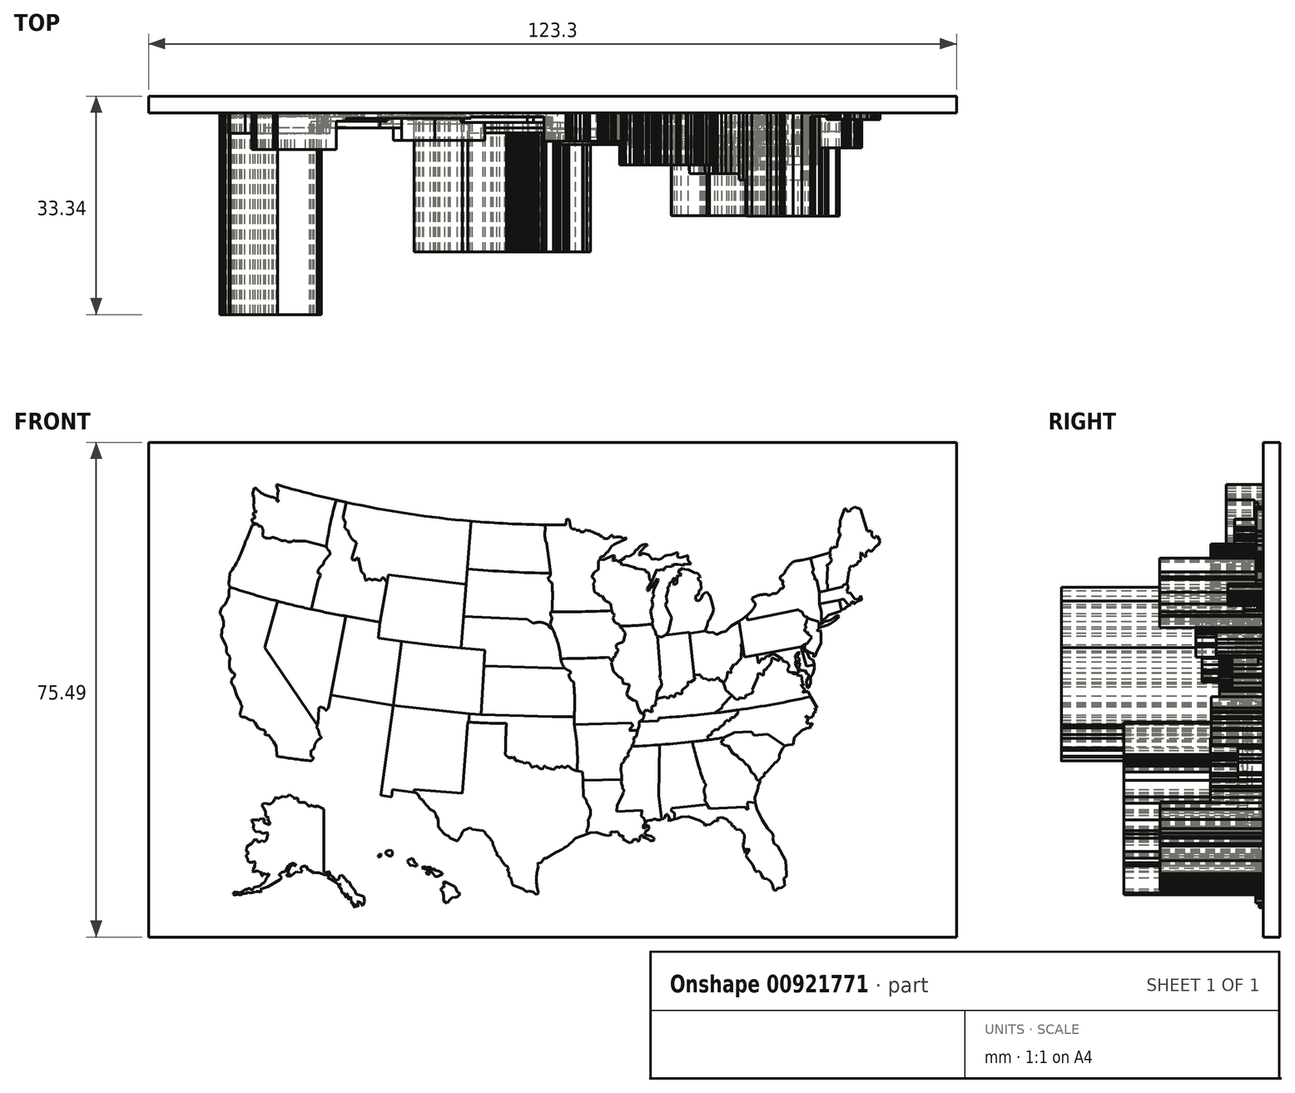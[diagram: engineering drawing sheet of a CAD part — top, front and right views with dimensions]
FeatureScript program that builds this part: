
annotation { "Feature Type Name" : "Feature", "Feature Type Description" : "" }
export const myFeature = defineFeature(function(context is Context, id is Id, definition is map)
    precondition{}
    {
        {
            var Q0;
            Q0=qCreatedBy(makeId("Front.planeOp"),FACE);
            var sketch = newSketch(context, id + "F0", { "sketchPlane" : qUnion([Q0])});
            skLineSegment(sketch, "E0.bottom", {"start": v(-61.56, 41.77) * mm, "end": v(61.74, 41.77) * mm});
            skLineSegment(sketch, "E0.top", {"start": v(-61.56, -33.72) * mm, "end": v(61.74, -33.72) * mm});
            skLineSegment(sketch, "E0.left", {"start": v(-61.56, 41.77) * mm, "end": v(-61.56, -33.72) * mm});
            skLineSegment(sketch, "E0.right", {"start": v(61.74, 41.77) * mm, "end": v(61.74, -33.72) * mm});
            skSolve(sketch);
        }
        {
            var Q0;
            Q0=qSketchRegion(id+"F0",true);
            extrude(context, id + "F1", {"entities" : qUnion([Q0]), "depth" : 2.54 * mm, "offsetDistance" : 25.4 * mm});
        }
        {
            var Q0;
            Q0=makeQuery(id+"F1.opExtrude","CAP_FACE",FACE,{"disambiguationData":[OSD([sQuery(id+"F0.wireOp",EDGE,"E0.bottom"),sQuery(id+"F0.wireOp",EDGE,"E0.top"),sQuery(id+"F0.wireOp",EDGE,"E0.left"),sQuery(id+"F0.wireOp",EDGE,"E0.right")])],"isStart":false});
            var sketch = newSketch(context, id + "F2", { "sketchPlane" : qUnion([Q0])});
            skLineSegment(sketch, "E1", {"start": v(-6.58, -23.8) * mm, "end": v(-6.79, -23.67) * mm});
            skLineSegment(sketch, "E2", {"start": v(-6.79, -23.67) * mm, "end": v(-6.62, -23.2) * mm});
            skLineSegment(sketch, "E3", {"start": v(-6.86, -22.87) * mm, "end": v(-6.62, -23.2) * mm});
            skLineSegment(sketch, "E4", {"start": v(-6.86, -22.87) * mm, "end": v(-7.18, -22.74) * mm});
            skArc(sketch, "E5", {"start": v(-7.96, -21.52) * mm, "mid": v(-7.6, -22.15) * mm, "end": v(-7.18, -22.74) * mm});
            skArc(sketch, "E6", {"start": v(-8.39, -21.24) * mm, "mid": v(-8.17, -21.38) * mm, "end": v(-7.96, -21.52) * mm});
            skArc(sketch, "E7", {"start": v(-8.39, -20.98) * mm, "mid": v(-8.39, -21.1) * mm, "end": v(-8.39, -21.24) * mm});
            skArc(sketch, "E8", {"start": v(-8.98, -19.66) * mm, "mid": v(-8.7, -20.33) * mm, "end": v(-8.39, -20.98) * mm});
            skArc(sketch, "E9", {"start": v(-9.07, -19.19) * mm, "mid": v(-9.17, -19.07) * mm, "end": v(-9.29, -18.98) * mm});
            skArc(sketch, "E10", {"start": v(-9.07, -19.19) * mm, "mid": v(-9.03, -19.42) * mm, "end": v(-8.98, -19.66) * mm});
            skLineSegment(sketch, "E11", {"start": v(-22.96, 11.38) * mm, "end": v(-24.2, 1.61) * mm});
            skLineSegment(sketch, "E12", {"start": v(-10.22, 10.07) * mm, "end": v(-10.37, 7.64) * mm});
            skLineSegment(sketch, "E13", {"start": v(-31.44, 15.25) * mm, "end": v(-26.22, 14.33) * mm});
            skLineSegment(sketch, "E14", {"start": v(-26.22, 14.33) * mm, "end": v(-26.5, 11.9) * mm});
            skLineSegment(sketch, "E15", {"start": v(-26.5, 11.9) * mm, "end": v(-22.96, 11.38) * mm});
            skLineSegment(sketch, "E16", {"start": v(-33.75, 3.22) * mm, "end": v(-31.44, 15.25) * mm});
            skArc(sketch, "E17", {"start": v(-49.13, 19.66) * mm, "mid": v(-40.36, 17.15) * mm, "end": v(-31.44, 15.25) * mm});
            skLineSegment(sketch, "E18", {"start": v(-43.82, 10.48) * mm, "end": v(-41.9, 17.54) * mm});
            skLineSegment(sketch, "E19", {"start": v(-43.82, 10.48) * mm, "end": v(-35.84, -1.39) * mm});
            skLineSegment(sketch, "E20", {"start": v(-26.22, 14.33) * mm, "end": v(-24.95, 21.56) * mm});
            skLineSegment(sketch, "E21", {"start": v(-13.08, 20.1) * mm, "end": v(-24.95, 21.56) * mm});
            skLineSegment(sketch, "E22", {"start": v(-13.67, -11.77) * mm, "end": v(-12.83, -0.9) * mm});
            skLineSegment(sketch, "E23", {"start": v(-12.83, -0.9) * mm, "end": v(-12.71, -0.9) * mm});
            skLineSegment(sketch, "E24", {"start": v(-12.71, -0.9) * mm, "end": v(-12.62, 0.37) * mm});
            skLineSegment(sketch, "E25", {"start": v(-26.15, -12.1) * mm, "end": v(-24.45, -12.34) * mm});
            skLineSegment(sketch, "E26", {"start": v(-24.45, -12.34) * mm, "end": v(-24.33, -11.2) * mm});
            skLineSegment(sketch, "E27", {"start": v(-24.33, -11.2) * mm, "end": v(-21.02, -11.66) * mm});
            skLineSegment(sketch, "E28", {"start": v(-21.02, -11.66) * mm, "end": v(-21.02, -11.2) * mm});
            skLineSegment(sketch, "E29", {"start": v(-21.02, -11.2) * mm, "end": v(-13.67, -11.77) * mm});
            skLineSegment(sketch, "E30", {"start": v(-37.29, -7.31) * mm, "end": v(-30.35, -11.42) * mm});
            skLineSegment(sketch, "E31", {"start": v(-30.35, -11.42) * mm, "end": v(-26.15, -12.1) * mm});
            skArc(sketch, "E32", {"start": v(-12.71, -0.9) * mm, "mid": v(-9.83, -1.07) * mm, "end": v(-6.95, -1.13) * mm});
            skArc(sketch, "E33", {"start": v(-6.95, -1.13) * mm, "mid": v(-7.05, -3.5) * mm, "end": v(-7.1, -5.86) * mm});
            skArc(sketch, "E34", {"start": v(-41.92, 35.31) * mm, "mid": v(-20.1, 30.62) * mm, "end": v(2.16, 29.2) * mm});
            skLineSegment(sketch, "E35", {"start": v(-13.08, 20.1) * mm, "end": v(-12.32, 29.75) * mm});
            skLineSegment(sketch, "E36", {"start": v(-13.46, 15.24) * mm, "end": v(-3.77, 14.75) * mm});
            skLineSegment(sketch, "E37", {"start": v(-10.37, 7.64) * mm, "end": v(2.04, 7.28) * mm});
            skArc(sketch, "E38", {"start": v(-0.2, 15.89) * mm, "mid": v(4.47, 15.94) * mm, "end": v(9.13, 16.1) * mm});
            skArc(sketch, "E39", {"start": v(1.33, 8.76) * mm, "mid": v(4.97, 8.83) * mm, "end": v(8.6, 8.97) * mm});
            skArc(sketch, "E40", {"start": v(10.38, 13.78) * mm, "mid": v(12.85, 13.82) * mm, "end": v(15.3, 14.07) * mm});
            skLineSegment(sketch, "E41", {"start": v(17.33, 12.38) * mm, "end": v(20.97, 12.8) * mm});
            skLineSegment(sketch, "E42", {"start": v(20.97, 12.8) * mm, "end": v(21.7, 6.25) * mm});
            skLineSegment(sketch, "E43", {"start": v(21, 12.63) * mm, "end": v(23.37, 13) * mm});
            skLineSegment(sketch, "E44", {"start": v(29.76, 15.36) * mm, "end": v(29.82, 14.67) * mm});
            skLineSegment(sketch, "E45", {"start": v(29.82, 14.67) * mm, "end": v(37.59, 16.24) * mm});
            skLineSegment(sketch, "E46", {"start": v(3.4, -0.12) * mm, "end": v(3.4, -1.32) * mm});
            skLineSegment(sketch, "E47", {"start": v(3.4, -1.32) * mm, "end": v(12.08, -1.02) * mm});
            skArc(sketch, "E48", {"start": v(3.4, -0.12) * mm, "mid": v(3.46, 2.54) * mm, "end": v(3.32, 5.2) * mm});
            skArc(sketch, "E49", {"start": v(-32.92, 32.97) * mm, "mid": v(-33.8, 29.44) * mm, "end": v(-34.4, 25.85) * mm});
            skArc(sketch, "E50", {"start": v(16.29, -0.29) * mm, "mid": v(27.94, 0.87) * mm, "end": v(39.47, 2.95) * mm});
            skLineSegment(sketch, "E51", {"start": v(13.29, -0.87) * mm, "end": v(16.25, -0.73) * mm});
            skLineSegment(sketch, "E52", {"start": v(16.25, -0.73) * mm, "end": v(16.29, -0.29) * mm});
            skArc(sketch, "E53", {"start": v(12.12, -4.62) * mm, "mid": v(19.15, -4.15) * mm, "end": v(26.15, -3.3) * mm});
            skLineSegment(sketch, "E54", {"start": v(4.75, -9.79) * mm, "end": v(10.62, -9.67) * mm});
            skLineSegment(sketch, "E55", {"start": v(-35.84, -1.39) * mm, "end": v(-35.69, -1.16) * mm});
            skLineSegment(sketch, "E56", {"start": v(-35.69, -1.16) * mm, "end": v(-35.58, 1.24) * mm});
            skArc(sketch, "E57", {"start": v(-35.22, 1.38) * mm, "mid": v(-35.42, 1.34) * mm, "end": v(-35.58, 1.24) * mm});
            skArc(sketch, "E58", {"start": v(-34.96, 1.24) * mm, "mid": v(-35.08, 1.33) * mm, "end": v(-35.22, 1.38) * mm});
            skArc(sketch, "E59", {"start": v(-34.77, 1.24) * mm, "mid": v(-34.86, 1.24) * mm, "end": v(-34.96, 1.24) * mm});
            skArc(sketch, "E60", {"start": v(-34.1, 1.24) * mm, "mid": v(-34.26, 1.1) * mm, "end": v(-34.37, 0.9) * mm});
            skArc(sketch, "E61", {"start": v(-34.61, 0.92) * mm, "mid": v(-34.67, 1.09) * mm, "end": v(-34.77, 1.24) * mm});
            skArc(sketch, "E62", {"start": v(-34.61, 0.92) * mm, "mid": v(-34.5, 0.9) * mm, "end": v(-34.37, 0.9) * mm});
            skLineSegment(sketch, "E63", {"start": v(-34.1, 1.24) * mm, "end": v(-33.75, 3.22) * mm});
            skArc(sketch, "E64", {"start": v(-42, -6.13) * mm, "mid": v(-39.51, -6.5) * mm, "end": v(-37, -6.82) * mm});
            skArc(sketch, "E65", {"start": v(-37, -6.82) * mm, "mid": v(-37.16, -7.06) * mm, "end": v(-37.29, -7.31) * mm});
            skLineSegment(sketch, "E66", {"start": v(-42.06, -4.67) * mm, "end": v(-42, -6.13) * mm});
            skLineSegment(sketch, "E67", {"start": v(-42.06, -4.67) * mm, "end": v(-42.49, -3.88) * mm});
            skLineSegment(sketch, "E68", {"start": v(-42.49, -3.88) * mm, "end": v(-42.72, -3.66) * mm});
            skLineSegment(sketch, "E69", {"start": v(-42.72, -3.66) * mm, "end": v(-43.18, -2.97) * mm});
            skLineSegment(sketch, "E70", {"start": v(-43.18, -2.97) * mm, "end": v(-43.84, -2.85) * mm});
            skLineSegment(sketch, "E71", {"start": v(-43.84, -2.85) * mm, "end": v(-43.84, -2.72) * mm});
            skLineSegment(sketch, "E72", {"start": v(-43.84, -2.72) * mm, "end": v(-43.74, -2.65) * mm});
            skLineSegment(sketch, "E73", {"start": v(-43.74, -2.65) * mm, "end": v(-43.78, -2.32) * mm});
            skLineSegment(sketch, "E74", {"start": v(-43.78, -2.32) * mm, "end": v(-43.93, -2.1) * mm});
            skLineSegment(sketch, "E75", {"start": v(-43.93, -2.1) * mm, "end": v(-44.47, -2) * mm});
            skLineSegment(sketch, "E76", {"start": v(-44.47, -2) * mm, "end": v(-44.88, -1.78) * mm});
            skLineSegment(sketch, "E77", {"start": v(-44.88, -1.78) * mm, "end": v(-45.3, -1.03) * mm});
            skLineSegment(sketch, "E78", {"start": v(-45.3, -1.03) * mm, "end": v(-45.63, -0.64) * mm});
            skLineSegment(sketch, "E79", {"start": v(-45.63, -0.64) * mm, "end": v(-46.03, -0.6) * mm});
            skLineSegment(sketch, "E80", {"start": v(-46.03, -0.6) * mm, "end": v(-46.9, -0.18) * mm});
            skLineSegment(sketch, "E81", {"start": v(-46.9, -0.18) * mm, "end": v(-47.32, -0.12) * mm});
            skLineSegment(sketch, "E82", {"start": v(-47.32, -0.12) * mm, "end": v(-47.62, 0.17) * mm});
            skLineSegment(sketch, "E83", {"start": v(-47.62, 0.17) * mm, "end": v(-47.32, 1.4) * mm});
            skLineSegment(sketch, "E84", {"start": v(-47.32, 1.4) * mm, "end": v(-47.32, 1.65) * mm});
            skLineSegment(sketch, "E85", {"start": v(-47.32, 1.65) * mm, "end": v(-47.5, 1.8) * mm});
            skLineSegment(sketch, "E86", {"start": v(-47.5, 1.8) * mm, "end": v(-47.5, 2.07) * mm});
            skLineSegment(sketch, "E87", {"start": v(-47.5, 2.07) * mm, "end": v(-48.07, 3.06) * mm});
            skLineSegment(sketch, "E88", {"start": v(-48.07, 3.06) * mm, "end": v(-48.53, 4.45) * mm});
            skLineSegment(sketch, "E89", {"start": v(-48.53, 4.45) * mm, "end": v(-48.84, 4.92) * mm});
            skLineSegment(sketch, "E90", {"start": v(-48.84, 4.92) * mm, "end": v(-48.94, 5.2) * mm});
            skLineSegment(sketch, "E91", {"start": v(-48.94, 5.2) * mm, "end": v(-48.88, 5.7) * mm});
            skArc(sketch, "E92", {"start": v(-48.88, 5.7) * mm, "mid": v(-48.47, 6.05) * mm, "end": v(-48.5, 6.58) * mm});
            skLineSegment(sketch, "E93", {"start": v(-48.5, 6.58) * mm, "end": v(-48.77, 6.64) * mm});
            skLineSegment(sketch, "E94", {"start": v(-48.77, 6.64) * mm, "end": v(-49.26, 7.32) * mm});
            skLineSegment(sketch, "E95", {"start": v(-49.26, 7.32) * mm, "end": v(-49.26, 8.3) * mm});
            skLineSegment(sketch, "E96", {"start": v(-49.26, 8.3) * mm, "end": v(-49.08, 9) * mm});
            skLineSegment(sketch, "E97", {"start": v(-49.08, 9) * mm, "end": v(-49.69, 9.7) * mm});
            skLineSegment(sketch, "E98", {"start": v(-49.69, 9.7) * mm, "end": v(-49.69, 9.96) * mm});
            skArc(sketch, "E99", {"start": v(-49.69, 9.96) * mm, "mid": v(-49.66, 10.43) * mm, "end": v(-49.81, 10.88) * mm});
            skLineSegment(sketch, "E100", {"start": v(-50.52, 12.25) * mm, "end": v(-49.81, 10.88) * mm});
            skLineSegment(sketch, "E101", {"start": v(-50.52, 12.25) * mm, "end": v(-50.4, 12.67) * mm});
            skLineSegment(sketch, "E102", {"start": v(-50.4, 12.67) * mm, "end": v(-50.35, 13.32) * mm});
            skLineSegment(sketch, "E103", {"start": v(-50.35, 13.32) * mm, "end": v(-50.15, 13.64) * mm});
            skLineSegment(sketch, "E104", {"start": v(-50.15, 13.64) * mm, "end": v(-50.12, 14.44) * mm});
            skLineSegment(sketch, "E105", {"start": v(-50.12, 14.44) * mm, "end": v(-50.4, 15.26) * mm});
            skLineSegment(sketch, "E106", {"start": v(-50.4, 15.26) * mm, "end": v(-50.7, 15.68) * mm});
            skLineSegment(sketch, "E107", {"start": v(-50.7, 15.68) * mm, "end": v(-50.46, 16.55) * mm});
            skLineSegment(sketch, "E108", {"start": v(-50.46, 16.55) * mm, "end": v(-50.27, 16.6) * mm});
            skLineSegment(sketch, "E109", {"start": v(-50.27, 16.6) * mm, "end": v(-50.23, 16.77) * mm});
            skLineSegment(sketch, "E110", {"start": v(-50.23, 16.77) * mm, "end": v(-49.9, 17.06) * mm});
            skLineSegment(sketch, "E111", {"start": v(-49.9, 17.06) * mm, "end": v(-49.32, 18.34) * mm});
            skLineSegment(sketch, "E112", {"start": v(-49.32, 18.34) * mm, "end": v(-49.32, 19.18) * mm});
            skLineSegment(sketch, "E113", {"start": v(-49.32, 19.18) * mm, "end": v(-49.13, 19.66) * mm});
            skArc(sketch, "E114", {"start": v(-35.53, -2.8) * mm, "mid": v(-35.62, -2.26) * mm, "end": v(-35.89, -1.79) * mm});
            skLineSegment(sketch, "E115", {"start": v(-35.84, -1.39) * mm, "end": v(-35.89, -1.79) * mm});
            skArc(sketch, "E116", {"start": v(-37, -6.82) * mm, "mid": v(-36.56, -6.69) * mm, "end": v(-36.45, -6.23) * mm});
            skLineSegment(sketch, "E117", {"start": v(-36.45, -6.23) * mm, "end": v(-36.81, -6.15) * mm});
            skLineSegment(sketch, "E118", {"start": v(-36.81, -6.15) * mm, "end": v(-36.77, -5.26) * mm});
            skArc(sketch, "E119", {"start": v(-36.77, -5.26) * mm, "mid": v(-36.48, -5.1) * mm, "end": v(-36.25, -4.85) * mm});
            skArc(sketch, "E120", {"start": v(-35.2, -3.37) * mm, "mid": v(-35.98, -3.93) * mm, "end": v(-36.25, -4.85) * mm});
            skArc(sketch, "E121", {"start": v(-35.2, -3.37) * mm, "mid": v(-35.32, -3.06) * mm, "end": v(-35.53, -2.8) * mm});
            skLineSegment(sketch, "E122", {"start": v(-36.71, 16.3) * mm, "end": v(-35.69, 20.66) * mm});
            skLineSegment(sketch, "E123", {"start": v(-35.69, 20.66) * mm, "end": v(-35.3, 21.49) * mm});
            skLineSegment(sketch, "E124", {"start": v(-35.3, 21.49) * mm, "end": v(-35.42, 21.74) * mm});
            skLineSegment(sketch, "E125", {"start": v(-35.42, 21.74) * mm, "end": v(-35.73, 21.82) * mm});
            skLineSegment(sketch, "E126", {"start": v(-34.4, 25.85) * mm, "end": v(-37.6, 26.7) * mm});
            skLineSegment(sketch, "E127", {"start": v(-37.6, 26.7) * mm, "end": v(-39.29, 26.7) * mm});
            skLineSegment(sketch, "E128", {"start": v(-39.29, 26.7) * mm, "end": v(-39.29, 26.82) * mm});
            skLineSegment(sketch, "E129", {"start": v(-39.29, 26.82) * mm, "end": v(-39.85, 26.6) * mm});
            skLineSegment(sketch, "E130", {"start": v(-39.85, 26.6) * mm, "end": v(-40.34, 26.6) * mm});
            skLineSegment(sketch, "E131", {"start": v(-40.34, 26.6) * mm, "end": v(-40.67, 26.84) * mm});
            skLineSegment(sketch, "E132", {"start": v(-40.67, 26.84) * mm, "end": v(-40.81, 26.76) * mm});
            skLineSegment(sketch, "E133", {"start": v(-40.81, 26.76) * mm, "end": v(-41.31, 26.76) * mm});
            skArc(sketch, "E134", {"start": v(-41.31, 26.76) * mm, "mid": v(-41.96, 27.09) * mm, "end": v(-42.67, 27.29) * mm});
            skArc(sketch, "E135", {"start": v(-44.22, 27.59) * mm, "mid": v(-43.5, 27.14) * mm, "end": v(-42.67, 27.29) * mm});
            skArc(sketch, "E136", {"start": v(-44.22, 27.59) * mm, "mid": v(-44.1, 28.32) * mm, "end": v(-44.4, 29) * mm});
            skLineSegment(sketch, "E137", {"start": v(-44.4, 29) * mm, "end": v(-44.82, 29) * mm});
            skLineSegment(sketch, "E138", {"start": v(-44.82, 29) * mm, "end": v(-44.82, 29.3) * mm});
            skLineSegment(sketch, "E139", {"start": v(-44.82, 29.3) * mm, "end": v(-45.08, 29.3) * mm});
            skLineSegment(sketch, "E140", {"start": v(-45.08, 29.3) * mm, "end": v(-45.37, 29.53) * mm});
            skLineSegment(sketch, "E141", {"start": v(-45.37, 29.53) * mm, "end": v(-45.56, 29.45) * mm});
            skLineSegment(sketch, "E142", {"start": v(-45.56, 29.45) * mm, "end": v(-45.81, 29.75) * mm});
            skLineSegment(sketch, "E143", {"start": v(-45.81, 29.75) * mm, "end": v(-45.78, 30.08) * mm});
            skLineSegment(sketch, "E144", {"start": v(-45.78, 30.08) * mm, "end": v(-45.5, 30.08) * mm});
            skLineSegment(sketch, "E145", {"start": v(-45.5, 30.08) * mm, "end": v(-45.31, 30.55) * mm});
            skLineSegment(sketch, "E146", {"start": v(-45.31, 30.55) * mm, "end": v(-45.58, 30.7) * mm});
            skLineSegment(sketch, "E147", {"start": v(-45.58, 30.7) * mm, "end": v(-45.55, 31.09) * mm});
            skLineSegment(sketch, "E148", {"start": v(-45.55, 31.09) * mm, "end": v(-45.04, 31.14) * mm});
            skLineSegment(sketch, "E149", {"start": v(-45.04, 31.14) * mm, "end": v(-45.4, 31.48) * mm});
            skLineSegment(sketch, "E150", {"start": v(-45.4, 31.48) * mm, "end": v(-45.54, 32.25) * mm});
            skLineSegment(sketch, "E151", {"start": v(-45.54, 32.25) * mm, "end": v(-45.47, 32.5) * mm});
            skLineSegment(sketch, "E152", {"start": v(-45.47, 32.5) * mm, "end": v(-45.47, 33.45) * mm});
            skLineSegment(sketch, "E153", {"start": v(-45.47, 33.45) * mm, "end": v(-45.66, 33.77) * mm});
            skLineSegment(sketch, "E154", {"start": v(-45.66, 33.77) * mm, "end": v(-45.66, 33.96) * mm});
            skLineSegment(sketch, "E155", {"start": v(-45.66, 33.96) * mm, "end": v(-45.45, 34.83) * mm});
            skLineSegment(sketch, "E156", {"start": v(-45.45, 34.83) * mm, "end": v(-45.2, 34.8) * mm});
            skArc(sketch, "E157", {"start": v(-45.2, 34.8) * mm, "mid": v(-43.98, 33.84) * mm, "end": v(-42.5, 33.4) * mm});
            skArc(sketch, "E158", {"start": v(-41.95, 32.72) * mm, "mid": v(-42.12, 33.15) * mm, "end": v(-42.5, 33.4) * mm});
            skArc(sketch, "E159", {"start": v(-41.83, 33.55) * mm, "mid": v(-41.91, 33.21) * mm, "end": v(-41.75, 32.9) * mm});
            skArc(sketch, "E160", {"start": v(-41.71, 34.33) * mm, "mid": v(-41.88, 33.96) * mm, "end": v(-41.83, 33.55) * mm});
            skLineSegment(sketch, "E161", {"start": v(-41.75, 32.9) * mm, "end": v(-41.75, 32.72) * mm});
            skLineSegment(sketch, "E162", {"start": v(-41.75, 32.72) * mm, "end": v(-41.95, 32.72) * mm});
            skLineSegment(sketch, "E163", {"start": v(-41.71, 34.33) * mm, "end": v(-42.05, 35.14) * mm});
            skLineSegment(sketch, "E164", {"start": v(-42.05, 35.14) * mm, "end": v(-42, 35.32) * mm});
            skLineSegment(sketch, "E165", {"start": v(-42, 35.32) * mm, "end": v(-41.92, 35.31) * mm});
            skArc(sketch, "E166", {"start": v(-34.98, 23.04) * mm, "mid": v(-35.52, 22.54) * mm, "end": v(-35.73, 21.82) * mm});
            skArc(sketch, "E167", {"start": v(-34.98, 23.04) * mm, "mid": v(-34.87, 23.25) * mm, "end": v(-34.84, 23.49) * mm});
            skArc(sketch, "E168", {"start": v(-33.85, 24.71) * mm, "mid": v(-34.37, 24.12) * mm, "end": v(-34.84, 23.49) * mm});
            skArc(sketch, "E169", {"start": v(-34.4, 25.85) * mm, "mid": v(-34.24, 25.45) * mm, "end": v(-33.9, 25.17) * mm});
            skLineSegment(sketch, "E170", {"start": v(-33.9, 25.17) * mm, "end": v(-33.85, 24.71) * mm});
            skArc(sketch, "E171", {"start": v(29.76, 15.36) * mm, "mid": v(30.49, 16.06) * mm, "end": v(31.05, 16.9) * mm});
            skArc(sketch, "E172", {"start": v(30.53, 18) * mm, "mid": v(30.63, 17.74) * mm, "end": v(30.73, 17.47) * mm});
            skArc(sketch, "E173", {"start": v(31.05, 16.9) * mm, "mid": v(30.98, 17.24) * mm, "end": v(30.73, 17.47) * mm});
            skArc(sketch, "E174", {"start": v(32.87, 18.54) * mm, "mid": v(31.66, 18.47) * mm, "end": v(30.53, 18) * mm});
            skArc(sketch, "E175", {"start": v(32.87, 18.54) * mm, "mid": v(33.13, 18.43) * mm, "end": v(33.4, 18.54) * mm});
            skArc(sketch, "E176", {"start": v(34.3, 18.7) * mm, "mid": v(33.83, 18.7) * mm, "end": v(33.4, 18.54) * mm});
            skArc(sketch, "E177", {"start": v(34.3, 18.7) * mm, "mid": v(34.63, 19.09) * mm, "end": v(34.94, 19.49) * mm});
            skArc(sketch, "E178", {"start": v(34.94, 19.49) * mm, "mid": v(35.35, 19.65) * mm, "end": v(35.2, 20.07) * mm});
            skArc(sketch, "E179", {"start": v(35.34, 20.66) * mm, "mid": v(35.23, 20.38) * mm, "end": v(35.2, 20.07) * mm});
            skArc(sketch, "E180", {"start": v(35.14, 21.47) * mm, "mid": v(34.83, 20.97) * mm, "end": v(35.34, 20.66) * mm});
            skArc(sketch, "E181", {"start": v(35.14, 21.47) * mm, "mid": v(35.32, 21.65) * mm, "end": v(35.49, 21.84) * mm});
            skArc(sketch, "E182", {"start": v(36.8, 23.54) * mm, "mid": v(36.05, 22.76) * mm, "end": v(35.49, 21.84) * mm});
            skArc(sketch, "E183", {"start": v(37.59, 16.24) * mm, "mid": v(37.87, 16.03) * mm, "end": v(38.21, 15.93) * mm});
            skArc(sketch, "E184", {"start": v(38.21, 15.93) * mm, "mid": v(38.36, 15.5) * mm, "end": v(38.65, 15.13) * mm});
            skArc(sketch, "E185", {"start": v(39.13, 14.92) * mm, "mid": v(38.93, 15.11) * mm, "end": v(38.65, 15.13) * mm});
            skLineSegment(sketch, "E186", {"start": v(39.13, 14.92) * mm, "end": v(40.77, 14.41) * mm});
            skLineSegment(sketch, "E187", {"start": v(40.77, 14.41) * mm, "end": v(40.77, 13.52) * mm});
            skArc(sketch, "E188", {"start": v(40.77, 13.52) * mm, "mid": v(42.45, 14.08) * mm, "end": v(43.84, 15.2) * mm});
            skLineSegment(sketch, "E189", {"start": v(43.84, 15.2) * mm, "end": v(43.42, 15.38) * mm});
            skArc(sketch, "E190", {"start": v(42.11, 14.53) * mm, "mid": v(42.84, 14.85) * mm, "end": v(43.42, 15.38) * mm});
            skArc(sketch, "E191", {"start": v(41.68, 14.53) * mm, "mid": v(41.9, 14.5) * mm, "end": v(42.11, 14.53) * mm});
            skLineSegment(sketch, "E192", {"start": v(41.68, 14.53) * mm, "end": v(41.18, 14.1) * mm});
            skLineSegment(sketch, "E193", {"start": v(41.18, 14.1) * mm, "end": v(40.99, 14.05) * mm});
            skLineSegment(sketch, "E194", {"start": v(40.99, 14.05) * mm, "end": v(40.99, 14.2) * mm});
            skLineSegment(sketch, "E195", {"start": v(40.99, 14.2) * mm, "end": v(41.18, 14.4) * mm});
            skLineSegment(sketch, "E196", {"start": v(41.18, 14.4) * mm, "end": v(41.18, 14.59) * mm});
            skLineSegment(sketch, "E197", {"start": v(41.18, 14.59) * mm, "end": v(40.98, 14.78) * mm});
            skLineSegment(sketch, "E198", {"start": v(40.98, 14.78) * mm, "end": v(41.1, 14.92) * mm});
            skLineSegment(sketch, "E199", {"start": v(41.1, 14.92) * mm, "end": v(41.1, 15.93) * mm});
            skLineSegment(sketch, "E200", {"start": v(41.1, 15.93) * mm, "end": v(40.82, 17.1) * mm});
            skLineSegment(sketch, "E201", {"start": v(40.82, 17.1) * mm, "end": v(40.82, 18.87) * mm});
            skLineSegment(sketch, "E202", {"start": v(40.82, 18.87) * mm, "end": v(40.42, 20.72) * mm});
            skArc(sketch, "E203", {"start": v(40.42, 20.72) * mm, "mid": v(40.27, 20.87) * mm, "end": v(40.08, 20.79) * mm});
            skArc(sketch, "E204", {"start": v(38.13, 23.76) * mm, "mid": v(37.46, 23.7) * mm, "end": v(36.8, 23.54) * mm});
            skLineSegment(sketch, "E205", {"start": v(38.13, 23.76) * mm, "end": v(39.46, 24.13) * mm});
            skLineSegment(sketch, "E206", {"start": v(39.46, 24.13) * mm, "end": v(39.88, 22.6) * mm});
            skArc(sketch, "E207", {"start": v(39.74, 21.98) * mm, "mid": v(39.89, 22.27) * mm, "end": v(39.88, 22.6) * mm});
            skLineSegment(sketch, "E208", {"start": v(39.74, 21.98) * mm, "end": v(40.12, 21.25) * mm});
            skLineSegment(sketch, "E209", {"start": v(40.12, 21.25) * mm, "end": v(40.08, 20.79) * mm});
            skLineSegment(sketch, "E210", {"start": v(-49.13, 19.66) * mm, "end": v(-49.38, 20.16) * mm});
            skLineSegment(sketch, "E211", {"start": v(-49.38, 20.16) * mm, "end": v(-49.22, 20.84) * mm});
            skLineSegment(sketch, "E212", {"start": v(-49.22, 20.84) * mm, "end": v(-49.15, 21.8) * mm});
            skArc(sketch, "E213", {"start": v(-49.15, 21.8) * mm, "mid": v(-47.77, 24.1) * mm, "end": v(-46.8, 26.59) * mm});
            skLineSegment(sketch, "E214", {"start": v(-45.08, 29.3) * mm, "end": v(-45.78, 29.15) * mm});
            skArc(sketch, "E215", {"start": v(-46.8, 26.59) * mm, "mid": v(-46.23, 27.84) * mm, "end": v(-45.78, 29.15) * mm});
            skLineSegment(sketch, "E216", {"start": v(-3.77, 14.75) * mm, "end": v(-2.83, 14.13) * mm});
            skArc(sketch, "E217", {"start": v(-0.54, 13.83) * mm, "mid": v(-1.65, 14.3) * mm, "end": v(-2.83, 14.13) * mm});
            skArc(sketch, "E218", {"start": v(-0.54, 13.83) * mm, "mid": v(-0.35, 13.5) * mm, "end": v(0.01, 13.4) * mm});
            skArc(sketch, "E219", {"start": v(1.33, 8.76) * mm, "mid": v(0.9, 11.14) * mm, "end": v(0.01, 13.4) * mm});
            skArc(sketch, "E220", {"start": v(1.33, 8.76) * mm, "mid": v(1.57, 7.96) * mm, "end": v(2.04, 7.28) * mm});
            skArc(sketch, "E221", {"start": v(2.04, 7.28) * mm, "mid": v(2.37, 7.03) * mm, "end": v(2.76, 6.9) * mm});
            skArc(sketch, "E222", {"start": v(2.6, 6.36) * mm, "mid": v(2.84, 6.58) * mm, "end": v(2.76, 6.9) * mm});
            skArc(sketch, "E223", {"start": v(2.6, 6.36) * mm, "mid": v(2.8, 5.67) * mm, "end": v(3.32, 5.2) * mm});
            skLineSegment(sketch, "E224", {"start": v(-31.41, 32.63) * mm, "end": v(-31.88, 30.28) * mm});
            skLineSegment(sketch, "E225", {"start": v(-31.88, 30.28) * mm, "end": v(-31.53, 29.54) * mm});
            skLineSegment(sketch, "E226", {"start": v(-31.53, 29.54) * mm, "end": v(-31.64, 28.82) * mm});
            skArc(sketch, "E227", {"start": v(-31.64, 28.82) * mm, "mid": v(-31.43, 28.53) * mm, "end": v(-31.12, 28.34) * mm});
            skArc(sketch, "E228", {"start": v(-31.12, 28.34) * mm, "mid": v(-30.7, 27.26) * mm, "end": v(-29.8, 26.51) * mm});
            skLineSegment(sketch, "E229", {"start": v(-30.57, 23.98) * mm, "end": v(-29.8, 26.51) * mm});
            skLineSegment(sketch, "E230", {"start": v(-30.24, 23.7) * mm, "end": v(-30.57, 23.98) * mm});
            skLineSegment(sketch, "E231", {"start": v(-28.57, 21.55) * mm, "end": v(-29.1, 22.08) * mm});
            skLineSegment(sketch, "E232", {"start": v(-29.1, 22.08) * mm, "end": v(-29.53, 24.14) * mm});
            skLineSegment(sketch, "E233", {"start": v(-29.53, 24.14) * mm, "end": v(-30.24, 23.7) * mm});
            skArc(sketch, "E234", {"start": v(-28.57, 21.55) * mm, "mid": v(-28.55, 21.07) * mm, "end": v(-28.35, 20.63) * mm});
            skArc(sketch, "E235", {"start": v(-27.48, 20.74) * mm, "mid": v(-27.95, 20.92) * mm, "end": v(-28.35, 20.63) * mm});
            skArc(sketch, "E236", {"start": v(-26.39, 20.63) * mm, "mid": v(-26.92, 20.86) * mm, "end": v(-27.48, 20.74) * mm});
            skArc(sketch, "E237", {"start": v(-26.39, 20.63) * mm, "mid": v(-26.1, 20.75) * mm, "end": v(-25.98, 21.04) * mm});
            skArc(sketch, "E238", {"start": v(-25.56, 21.03) * mm, "mid": v(-25.41, 20.68) * mm, "end": v(-25.15, 20.41) * mm});
            skArc(sketch, "E239", {"start": v(-25.56, 21.03) * mm, "mid": v(-25.77, 21.1) * mm, "end": v(-25.98, 21.04) * mm});
            skArc(sketch, "E240", {"start": v(3.84, -8.37) * mm, "mid": v(3.84, -4.83) * mm, "end": v(3.4, -1.32) * mm});
            skLineSegment(sketch, "E241", {"start": v(3.84, -8.37) * mm, "end": v(4.68, -8.52) * mm});
            skLineSegment(sketch, "E242", {"start": v(4.68, -8.52) * mm, "end": v(4.75, -9.79) * mm});
            skLineSegment(sketch, "E243", {"start": v(4.75, -9.79) * mm, "end": v(4.8, -12.33) * mm});
            skLineSegment(sketch, "E244", {"start": v(-6.58, -23.8) * mm, "end": v(-6.58, -24.24) * mm});
            skArc(sketch, "E245", {"start": v(-6.58, -24.24) * mm, "mid": v(-6.5, -24.51) * mm, "end": v(-6.25, -24.67) * mm});
            skArc(sketch, "E246", {"start": v(-6.25, -24.67) * mm, "mid": v(-6.14, -25.25) * mm, "end": v(-5.96, -25.81) * mm});
            skLineSegment(sketch, "E247", {"start": v(-2.03, -27) * mm, "end": v(-2.35, -27.24) * mm});
            skLineSegment(sketch, "E248", {"start": v(-2.35, -27.24) * mm, "end": v(-2.88, -26.82) * mm});
            skLineSegment(sketch, "E249", {"start": v(-2.88, -26.82) * mm, "end": v(-3.49, -26.72) * mm});
            skLineSegment(sketch, "E250", {"start": v(-3.49, -26.72) * mm, "end": v(-3.72, -26.79) * mm});
            skLineSegment(sketch, "E251", {"start": v(-3.72, -26.79) * mm, "end": v(-3.92, -26.8) * mm});
            skLineSegment(sketch, "E252", {"start": v(-3.92, -26.8) * mm, "end": v(-4.38, -26.37) * mm});
            skLineSegment(sketch, "E253", {"start": v(-4.38, -26.37) * mm, "end": v(-5.96, -25.81) * mm});
            skLineSegment(sketch, "E254", {"start": v(13.06, -2.2) * mm, "end": v(11.8, -2.2) * mm});
            skArc(sketch, "E255", {"start": v(12.28, -1.61) * mm, "mid": v(12, -1.86) * mm, "end": v(11.8, -2.2) * mm});
            skArc(sketch, "E256", {"start": v(12.28, -1.61) * mm, "mid": v(12.26, -1.29) * mm, "end": v(12.08, -1.02) * mm});
            skLineSegment(sketch, "E257", {"start": v(0.01, 13.4) * mm, "end": v(-0.29, 13.99) * mm});
            skLineSegment(sketch, "E258", {"start": v(-0.29, 13.99) * mm, "end": v(0.01, 15.11) * mm});
            skArc(sketch, "E259", {"start": v(-0.2, 15.89) * mm, "mid": v(-0.2, 15.47) * mm, "end": v(0.01, 15.11) * mm});
            skArc(sketch, "E260", {"start": v(-12.9, 22.47) * mm, "mid": v(-6.57, 22.02) * mm, "end": v(-0.24, 21.8) * mm});
            skArc(sketch, "E261", {"start": v(0.01, 15.89) * mm, "mid": v(0.08, 18.1) * mm, "end": v(0.04, 20.3) * mm});
            skArc(sketch, "E262", {"start": v(-0.58, 21.14) * mm, "mid": v(-0.28, 21.4) * mm, "end": v(-0.24, 21.8) * mm});
            skArc(sketch, "E263", {"start": v(-0.58, 21.14) * mm, "mid": v(-0.37, 20.65) * mm, "end": v(0.04, 20.3) * mm});
            skArc(sketch, "E264", {"start": v(-1.03, 28.4) * mm, "mid": v(-1.02, 28.82) * mm, "end": v(-1.2, 29.2) * mm});
            skArc(sketch, "E265", {"start": v(-1.03, 28.4) * mm, "mid": v(-1.06, 27.27) * mm, "end": v(-0.76, 26.18) * mm});
            skLineSegment(sketch, "E266", {"start": v(-0.76, 26.18) * mm, "end": v(-0.31, 22.92) * mm});
            skLineSegment(sketch, "E267", {"start": v(-0.31, 22.92) * mm, "end": v(-0.24, 21.8) * mm});
            skArc(sketch, "E268", {"start": v(5.3, -13.32) * mm, "mid": v(5.2, -12.75) * mm, "end": v(4.8, -12.33) * mm});
            skArc(sketch, "E269", {"start": v(5.5, -15.85) * mm, "mid": v(5.9, -14.55) * mm, "end": v(5.3, -13.32) * mm});
            skArc(sketch, "E270", {"start": v(5.3, -17.48) * mm, "mid": v(5.56, -16.68) * mm, "end": v(5.5, -15.85) * mm});
            skLineSegment(sketch, "E271", {"start": v(5.3, -17.48) * mm, "end": v(5.4, -17.97) * mm});
            skLineSegment(sketch, "E272", {"start": v(5.4, -17.97) * mm, "end": v(3.57, -18.63) * mm});
            skArc(sketch, "E273", {"start": v(0.84, -20.66) * mm, "mid": v(2.33, -19.81) * mm, "end": v(3.57, -18.63) * mm});
            skArc(sketch, "E274", {"start": v(0.84, -20.66) * mm, "mid": v(-0.02, -21.14) * mm, "end": v(-0.82, -21.71) * mm});
            skArc(sketch, "E275", {"start": v(-2.03, -22.86) * mm, "mid": v(-2.37, -24.93) * mm, "end": v(-2.03, -27) * mm});
            skLineSegment(sketch, "E276", {"start": v(-0.82, -21.71) * mm, "end": v(-1.19, -21.71) * mm});
            skLineSegment(sketch, "E277", {"start": v(-1.19, -21.71) * mm, "end": v(-1.65, -22.39) * mm});
            skLineSegment(sketch, "E278", {"start": v(-1.65, -22.39) * mm, "end": v(-2.1, -22.43) * mm});
            skLineSegment(sketch, "E279", {"start": v(-2.1, -22.43) * mm, "end": v(-2.22, -22.65) * mm});
            skLineSegment(sketch, "E280", {"start": v(-2.22, -22.65) * mm, "end": v(-2.03, -22.86) * mm});
            skLineSegment(sketch, "E281", {"start": v(-9.29, -18.98) * mm, "end": v(-9.29, -18.82) * mm});
            skLineSegment(sketch, "E282", {"start": v(-9.29, -18.82) * mm, "end": v(-10.2, -17.93) * mm});
            skLineSegment(sketch, "E283", {"start": v(-10.2, -17.93) * mm, "end": v(-10.2, -17.76) * mm});
            skLineSegment(sketch, "E284", {"start": v(-10.2, -17.76) * mm, "end": v(-10.52, -17.52) * mm});
            skLineSegment(sketch, "E285", {"start": v(-10.52, -17.52) * mm, "end": v(-12.13, -17.32) * mm});
            skLineSegment(sketch, "E286", {"start": v(-12.13, -17.32) * mm, "end": v(-12.48, -17.04) * mm});
            skLineSegment(sketch, "E287", {"start": v(-12.48, -17.04) * mm, "end": v(-13.4, -17.41) * mm});
            skLineSegment(sketch, "E288", {"start": v(-13.4, -17.41) * mm, "end": v(-13.74, -17.82) * mm});
            skLineSegment(sketch, "E289", {"start": v(-13.74, -17.82) * mm, "end": v(-13.77, -18.12) * mm});
            skLineSegment(sketch, "E290", {"start": v(-13.77, -18.12) * mm, "end": v(-14.47, -19.07) * mm});
            skLineSegment(sketch, "E291", {"start": v(-14.47, -19.07) * mm, "end": v(-15.5, -18.65) * mm});
            skLineSegment(sketch, "E292", {"start": v(-15.5, -18.65) * mm, "end": v(-15.75, -18.3) * mm});
            skLineSegment(sketch, "E293", {"start": v(-15.75, -18.3) * mm, "end": v(-16.33, -18.05) * mm});
            skLineSegment(sketch, "E294", {"start": v(-16.33, -18.05) * mm, "end": v(-17.1, -17.24) * mm});
            skLineSegment(sketch, "E295", {"start": v(-17.1, -17.24) * mm, "end": v(-17.35, -16.8) * mm});
            skLineSegment(sketch, "E296", {"start": v(-17.35, -16.8) * mm, "end": v(-17.37, -15.79) * mm});
            skLineSegment(sketch, "E297", {"start": v(-17.37, -15.79) * mm, "end": v(-17.71, -15.17) * mm});
            skLineSegment(sketch, "E298", {"start": v(-17.71, -15.17) * mm, "end": v(-17.78, -14.79) * mm});
            skLineSegment(sketch, "E299", {"start": v(-17.78, -14.79) * mm, "end": v(-18.07, -14.5) * mm});
            skLineSegment(sketch, "E300", {"start": v(-18.07, -14.5) * mm, "end": v(-18.6, -14.24) * mm});
            skLineSegment(sketch, "E301", {"start": v(-18.6, -14.24) * mm, "end": v(-19.57, -13.1) * mm});
            skLineSegment(sketch, "E302", {"start": v(-19.57, -13.1) * mm, "end": v(-19.7, -12.79) * mm});
            skLineSegment(sketch, "E303", {"start": v(-19.7, -12.79) * mm, "end": v(-20.17, -12.57) * mm});
            skLineSegment(sketch, "E304", {"start": v(-20.17, -12.57) * mm, "end": v(-20.35, -12.1) * mm});
            skLineSegment(sketch, "E305", {"start": v(-20.35, -12.1) * mm, "end": v(-20.72, -11.73) * mm});
            skLineSegment(sketch, "E306", {"start": v(-20.72, -11.73) * mm, "end": v(-21.02, -11.66) * mm});
            skArc(sketch, "E307", {"start": v(21.4, -3.92) * mm, "mid": v(22.16, -6.77) * mm, "end": v(23, -9.6) * mm});
            skLineSegment(sketch, "E308", {"start": v(16.4, -4.38) * mm, "end": v(16.3, -12.15) * mm});
            skLineSegment(sketch, "E309", {"start": v(16.3, -12.15) * mm, "end": v(16.74, -15.71) * mm});
            skLineSegment(sketch, "E310", {"start": v(16.74, -15.71) * mm, "end": v(17.12, -15.67) * mm});
            skLineSegment(sketch, "E311", {"start": v(17.12, -15.67) * mm, "end": v(17.42, -14.93) * mm});
            skLineSegment(sketch, "E312", {"start": v(17.42, -14.93) * mm, "end": v(17.64, -15.03) * mm});
            skLineSegment(sketch, "E313", {"start": v(17.64, -15.03) * mm, "end": v(18, -15.7) * mm});
            skLineSegment(sketch, "E314", {"start": v(18, -15.7) * mm, "end": v(17.67, -15.93) * mm});
            skLineSegment(sketch, "E315", {"start": v(17.67, -15.93) * mm, "end": v(17.92, -15.98) * mm});
            skLineSegment(sketch, "E316", {"start": v(17.92, -15.98) * mm, "end": v(18.7, -15.69) * mm});
            skLineSegment(sketch, "E317", {"start": v(18.7, -15.69) * mm, "end": v(19.12, -15.62) * mm});
            skLineSegment(sketch, "E318", {"start": v(19.12, -15.62) * mm, "end": v(19.74, -15.42) * mm});
            skLineSegment(sketch, "E319", {"start": v(19.74, -15.42) * mm, "end": v(20.83, -15.3) * mm});
            skLineSegment(sketch, "E320", {"start": v(20.83, -15.3) * mm, "end": v(22.65, -15.95) * mm});
            skLineSegment(sketch, "E321", {"start": v(22.65, -15.95) * mm, "end": v(22.84, -16.18) * mm});
            skLineSegment(sketch, "E322", {"start": v(22.84, -16.18) * mm, "end": v(22.97, -16.18) * mm});
            skLineSegment(sketch, "E323", {"start": v(22.97, -16.18) * mm, "end": v(23.2, -16.38) * mm});
            skLineSegment(sketch, "E324", {"start": v(23.2, -16.38) * mm, "end": v(23.32, -16.75) * mm});
            skLineSegment(sketch, "E325", {"start": v(23.32, -16.75) * mm, "end": v(23.59, -16.59) * mm});
            skLineSegment(sketch, "E326", {"start": v(23.59, -16.59) * mm, "end": v(24.18, -16.54) * mm});
            skLineSegment(sketch, "E327", {"start": v(24.18, -16.54) * mm, "end": v(24.9, -15.95) * mm});
            skLineSegment(sketch, "E328", {"start": v(24.9, -15.95) * mm, "end": v(25.29, -16) * mm});
            skLineSegment(sketch, "E329", {"start": v(25.29, -16) * mm, "end": v(25.26, -15.57) * mm});
            skLineSegment(sketch, "E330", {"start": v(25.26, -15.57) * mm, "end": v(25.98, -15.46) * mm});
            skLineSegment(sketch, "E331", {"start": v(25.98, -15.46) * mm, "end": v(26.74, -15.74) * mm});
            skLineSegment(sketch, "E332", {"start": v(26.74, -15.74) * mm, "end": v(27.04, -16.15) * mm});
            skLineSegment(sketch, "E333", {"start": v(27.04, -16.15) * mm, "end": v(27.35, -16.3) * mm});
            skLineSegment(sketch, "E334", {"start": v(27.35, -16.3) * mm, "end": v(27.48, -16.75) * mm});
            skLineSegment(sketch, "E335", {"start": v(27.48, -16.75) * mm, "end": v(27.83, -16.84) * mm});
            skLineSegment(sketch, "E336", {"start": v(27.83, -16.84) * mm, "end": v(28.06, -17.27) * mm});
            skLineSegment(sketch, "E337", {"start": v(28.06, -17.27) * mm, "end": v(28.8, -17.36) * mm});
            skLineSegment(sketch, "E338", {"start": v(24.01, -14.13) * mm, "end": v(29.58, -13.85) * mm});
            skLineSegment(sketch, "E339", {"start": v(18.26, -14.07) * mm, "end": v(23.65, -13.52) * mm});
            skLineSegment(sketch, "E340", {"start": v(23.65, -13.52) * mm, "end": v(24.01, -14.13) * mm});
            skLineSegment(sketch, "E341", {"start": v(18.26, -14.07) * mm, "end": v(18.22, -14.42) * mm});
            skLineSegment(sketch, "E342", {"start": v(18.22, -14.42) * mm, "end": v(18.69, -14.83) * mm});
            skLineSegment(sketch, "E343", {"start": v(18.69, -14.83) * mm, "end": v(18.7, -15.69) * mm});
            skArc(sketch, "E344", {"start": v(23.2, -10.17) * mm, "mid": v(23.18, -9.86) * mm, "end": v(23, -9.6) * mm});
            skArc(sketch, "E345", {"start": v(23.48, -10.56) * mm, "mid": v(23.4, -10.32) * mm, "end": v(23.2, -10.17) * mm});
            skArc(sketch, "E346", {"start": v(23.48, -10.56) * mm, "mid": v(23.23, -11.23) * mm, "end": v(23.33, -11.93) * mm});
            skArc(sketch, "E347", {"start": v(23.33, -12.94) * mm, "mid": v(23.39, -12.44) * mm, "end": v(23.33, -11.93) * mm});
            skArc(sketch, "E348", {"start": v(23.65, -13.52) * mm, "mid": v(23.55, -13.2) * mm, "end": v(23.33, -12.94) * mm});
            skLineSegment(sketch, "E349", {"start": v(13.79, -14.4) * mm, "end": v(9.9, -14.59) * mm});
            skLineSegment(sketch, "E350", {"start": v(9.9, -14.59) * mm, "end": v(9.95, -13.65) * mm});
            skLineSegment(sketch, "E351", {"start": v(9.95, -13.65) * mm, "end": v(10.92, -11.8) * mm});
            skLineSegment(sketch, "E352", {"start": v(13.79, -14.4) * mm, "end": v(13.65, -15.29) * mm});
            skLineSegment(sketch, "E353", {"start": v(13.65, -15.29) * mm, "end": v(14.05, -15.68) * mm});
            skLineSegment(sketch, "E354", {"start": v(14.05, -15.68) * mm, "end": v(14.29, -16.3) * mm});
            skLineSegment(sketch, "E355", {"start": v(14.29, -16.3) * mm, "end": v(14.72, -15.87) * mm});
            skArc(sketch, "E356", {"start": v(14.72, -15.87) * mm, "mid": v(15.01, -15.92) * mm, "end": v(15.3, -15.87) * mm});
            skArc(sketch, "E357", {"start": v(16.05, -15.87) * mm, "mid": v(15.68, -15.72) * mm, "end": v(15.3, -15.87) * mm});
            skLineSegment(sketch, "E358", {"start": v(16.74, -15.71) * mm, "end": v(16.62, -15.84) * mm});
            skLineSegment(sketch, "E359", {"start": v(16.62, -15.84) * mm, "end": v(16.05, -15.87) * mm});
            skArc(sketch, "E360", {"start": v(2.57, -7.66) * mm, "mid": v(3.14, -8.12) * mm, "end": v(3.84, -8.37) * mm});
            skArc(sketch, "E361", {"start": v(2.57, -7.66) * mm, "mid": v(2.33, -7.64) * mm, "end": v(2.17, -7.83) * mm});
            skArc(sketch, "E362", {"start": v(1.75, -7.81) * mm, "mid": v(1.47, -7.67) * mm, "end": v(1.22, -7.87) * mm});
            skLineSegment(sketch, "E363", {"start": v(2.17, -7.83) * mm, "end": v(1.75, -7.81) * mm});
            skLineSegment(sketch, "E364", {"start": v(1.22, -7.87) * mm, "end": v(1.01, -7.77) * mm});
            skLineSegment(sketch, "E365", {"start": v(1.01, -7.77) * mm, "end": v(0.54, -7.78) * mm});
            skLineSegment(sketch, "E366", {"start": v(0.54, -7.78) * mm, "end": v(0.47, -8) * mm});
            skLineSegment(sketch, "E367", {"start": v(0.47, -8) * mm, "end": v(0.22, -8.13) * mm});
            skLineSegment(sketch, "E368", {"start": v(0.22, -8.13) * mm, "end": v(-0.9, -7.81) * mm});
            skLineSegment(sketch, "E369", {"start": v(-0.9, -7.81) * mm, "end": v(-1.04, -7.61) * mm});
            skLineSegment(sketch, "E370", {"start": v(-1.04, -7.61) * mm, "end": v(-1.17, -7.62) * mm});
            skLineSegment(sketch, "E371", {"start": v(-1.17, -7.62) * mm, "end": v(-1.4, -8.05) * mm});
            skLineSegment(sketch, "E372", {"start": v(-1.4, -8.05) * mm, "end": v(-1.55, -8.11) * mm});
            skLineSegment(sketch, "E373", {"start": v(-1.55, -8.11) * mm, "end": v(-2.06, -7.92) * mm});
            skLineSegment(sketch, "E374", {"start": v(-2.06, -7.92) * mm, "end": v(-2.13, -7.67) * mm});
            skLineSegment(sketch, "E375", {"start": v(-2.13, -7.67) * mm, "end": v(-2.49, -7.65) * mm});
            skLineSegment(sketch, "E376", {"start": v(-2.49, -7.65) * mm, "end": v(-2.59, -7.58) * mm});
            skLineSegment(sketch, "E377", {"start": v(-2.59, -7.58) * mm, "end": v(-2.87, -7.84) * mm});
            skLineSegment(sketch, "E378", {"start": v(-2.87, -7.84) * mm, "end": v(-3.13, -7.76) * mm});
            skLineSegment(sketch, "E379", {"start": v(-3.13, -7.76) * mm, "end": v(-3.17, -7.52) * mm});
            skLineSegment(sketch, "E380", {"start": v(-3.17, -7.52) * mm, "end": v(-3.53, -7.12) * mm});
            skLineSegment(sketch, "E381", {"start": v(-3.53, -7.12) * mm, "end": v(-3.9, -7.06) * mm});
            skLineSegment(sketch, "E382", {"start": v(-3.9, -7.06) * mm, "end": v(-4.13, -7.25) * mm});
            skLineSegment(sketch, "E383", {"start": v(-4.13, -7.25) * mm, "end": v(-4.47, -7.01) * mm});
            skLineSegment(sketch, "E384", {"start": v(-4.47, -7.01) * mm, "end": v(-4.87, -6.98) * mm});
            skLineSegment(sketch, "E385", {"start": v(-4.87, -6.98) * mm, "end": v(-5.14, -6.85) * mm});
            skLineSegment(sketch, "E386", {"start": v(-5.14, -6.85) * mm, "end": v(-5.6, -6.82) * mm});
            skLineSegment(sketch, "E387", {"start": v(-5.6, -6.82) * mm, "end": v(-5.6, -6.38) * mm});
            skLineSegment(sketch, "E388", {"start": v(-5.6, -6.38) * mm, "end": v(-5.85, -6.27) * mm});
            skLineSegment(sketch, "E389", {"start": v(-5.85, -6.27) * mm, "end": v(-5.88, -6.4) * mm});
            skLineSegment(sketch, "E390", {"start": v(-5.88, -6.4) * mm, "end": v(-6.06, -6.42) * mm});
            skLineSegment(sketch, "E391", {"start": v(-6.06, -6.42) * mm, "end": v(-6.25, -6.2) * mm});
            skLineSegment(sketch, "E392", {"start": v(-6.25, -6.2) * mm, "end": v(-6.35, -6.4) * mm});
            skLineSegment(sketch, "E393", {"start": v(-6.35, -6.4) * mm, "end": v(-6.48, -6.42) * mm});
            skLineSegment(sketch, "E394", {"start": v(-6.48, -6.42) * mm, "end": v(-7.1, -5.86) * mm});
            skLineSegment(sketch, "E395", {"start": v(5.4, -17.97) * mm, "end": v(5.84, -17.82) * mm});
            skLineSegment(sketch, "E396", {"start": v(5.84, -17.82) * mm, "end": v(6.78, -17.76) * mm});
            skLineSegment(sketch, "E397", {"start": v(6.78, -17.76) * mm, "end": v(7.93, -18.15) * mm});
            skLineSegment(sketch, "E398", {"start": v(7.93, -18.15) * mm, "end": v(8.61, -18.27) * mm});
            skLineSegment(sketch, "E399", {"start": v(8.61, -18.27) * mm, "end": v(9.13, -18.04) * mm});
            skLineSegment(sketch, "E400", {"start": v(9.13, -18.04) * mm, "end": v(8.9, -17.9) * mm});
            skLineSegment(sketch, "E401", {"start": v(8.9, -17.9) * mm, "end": v(8.96, -17.72) * mm});
            skLineSegment(sketch, "E402", {"start": v(8.96, -17.72) * mm, "end": v(9.3, -17.6) * mm});
            skLineSegment(sketch, "E403", {"start": v(9.3, -17.6) * mm, "end": v(9.5, -17.75) * mm});
            skLineSegment(sketch, "E404", {"start": v(9.5, -17.75) * mm, "end": v(9.73, -17.63) * mm});
            skLineSegment(sketch, "E405", {"start": v(9.73, -17.63) * mm, "end": v(10.06, -17.7) * mm});
            skLineSegment(sketch, "E406", {"start": v(10.06, -17.7) * mm, "end": v(10.26, -18.04) * mm});
            skLineSegment(sketch, "E407", {"start": v(10.26, -18.04) * mm, "end": v(10.26, -18.26) * mm});
            skLineSegment(sketch, "E408", {"start": v(10.26, -18.26) * mm, "end": v(10.76, -18.27) * mm});
            skLineSegment(sketch, "E409", {"start": v(10.76, -18.27) * mm, "end": v(10.97, -18.44) * mm});
            skLineSegment(sketch, "E410", {"start": v(10.97, -18.44) * mm, "end": v(10.78, -18.74) * mm});
            skLineSegment(sketch, "E411", {"start": v(10.78, -18.74) * mm, "end": v(11.84, -19.33) * mm});
            skLineSegment(sketch, "E412", {"start": v(11.84, -19.33) * mm, "end": v(12.27, -19.17) * mm});
            skLineSegment(sketch, "E413", {"start": v(12.27, -19.17) * mm, "end": v(12.34, -18.9) * mm});
            skLineSegment(sketch, "E414", {"start": v(12.34, -18.9) * mm, "end": v(12.65, -18.85) * mm});
            skLineSegment(sketch, "E415", {"start": v(12.65, -18.85) * mm, "end": v(12.8, -18.67) * mm});
            skLineSegment(sketch, "E416", {"start": v(12.8, -18.67) * mm, "end": v(13, -18.8) * mm});
            skLineSegment(sketch, "E417", {"start": v(13, -18.8) * mm, "end": v(13.07, -19.1) * mm});
            skLineSegment(sketch, "E418", {"start": v(13.07, -19.1) * mm, "end": v(13.19, -19.16) * mm});
            skLineSegment(sketch, "E419", {"start": v(13.19, -19.16) * mm, "end": v(13.47, -18.77) * mm});
            skLineSegment(sketch, "E420", {"start": v(13.47, -18.77) * mm, "end": v(13.47, -18.7) * mm});
            skLineSegment(sketch, "E421", {"start": v(13.47, -18.7) * mm, "end": v(13.34, -18.66) * mm});
            skLineSegment(sketch, "E422", {"start": v(13.34, -18.66) * mm, "end": v(13.41, -18.54) * mm});
            skLineSegment(sketch, "E423", {"start": v(13.41, -18.54) * mm, "end": v(13.44, -18.3) * mm});
            skLineSegment(sketch, "E424", {"start": v(13.44, -18.3) * mm, "end": v(13.65, -18.27) * mm});
            skLineSegment(sketch, "E425", {"start": v(13.65, -18.27) * mm, "end": v(13.79, -18.11) * mm});
            skLineSegment(sketch, "E426", {"start": v(13.79, -18.11) * mm, "end": v(13.89, -18.2) * mm});
            skLineSegment(sketch, "E427", {"start": v(13.89, -18.2) * mm, "end": v(13.86, -18.5) * mm});
            skLineSegment(sketch, "E428", {"start": v(13.86, -18.5) * mm, "end": v(14.22, -18.57) * mm});
            skLineSegment(sketch, "E429", {"start": v(14.22, -18.57) * mm, "end": v(14.83, -18.85) * mm});
            skLineSegment(sketch, "E430", {"start": v(14.83, -18.85) * mm, "end": v(14.92, -18.99) * mm});
            skLineSegment(sketch, "E431", {"start": v(14.92, -18.99) * mm, "end": v(15.26, -19) * mm});
            skLineSegment(sketch, "E432", {"start": v(15.26, -19) * mm, "end": v(15.38, -19.09) * mm});
            skLineSegment(sketch, "E433", {"start": v(15.38, -19.09) * mm, "end": v(15.64, -18.77) * mm});
            skLineSegment(sketch, "E434", {"start": v(15.64, -18.77) * mm, "end": v(15.63, -18.63) * mm});
            skLineSegment(sketch, "E435", {"start": v(15.63, -18.63) * mm, "end": v(15.48, -18.6) * mm});
            skLineSegment(sketch, "E436", {"start": v(15.48, -18.6) * mm, "end": v(15.13, -18.3) * mm});
            skLineSegment(sketch, "E437", {"start": v(15.13, -18.3) * mm, "end": v(14.45, -18.18) * mm});
            skLineSegment(sketch, "E438", {"start": v(14.45, -18.18) * mm, "end": v(14.13, -17.98) * mm});
            skLineSegment(sketch, "E439", {"start": v(14.13, -17.98) * mm, "end": v(14.36, -17.6) * mm});
            skLineSegment(sketch, "E440", {"start": v(14.36, -17.6) * mm, "end": v(14.32, -17.45) * mm});
            skLineSegment(sketch, "E441", {"start": v(14.32, -17.45) * mm, "end": v(14.66, -17.45) * mm});
            skLineSegment(sketch, "E442", {"start": v(14.66, -17.45) * mm, "end": v(14.85, -17.17) * mm});
            skLineSegment(sketch, "E443", {"start": v(14.85, -17.17) * mm, "end": v(14.68, -16.63) * mm});
            skLineSegment(sketch, "E444", {"start": v(14.68, -16.63) * mm, "end": v(14.34, -16.79) * mm});
            skLineSegment(sketch, "E445", {"start": v(14.34, -16.79) * mm, "end": v(14.3, -17.13) * mm});
            skLineSegment(sketch, "E446", {"start": v(14.3, -17.13) * mm, "end": v(13.94, -17.07) * mm});
            skLineSegment(sketch, "E447", {"start": v(13.94, -17.07) * mm, "end": v(13.83, -16.86) * mm});
            skLineSegment(sketch, "E448", {"start": v(13.83, -16.86) * mm, "end": v(14.29, -16.3) * mm});
            skLineSegment(sketch, "E449", {"start": v(10.92, -11.8) * mm, "end": v(10.83, -11.56) * mm});
            skLineSegment(sketch, "E450", {"start": v(10.83, -11.56) * mm, "end": v(10.99, -11.53) * mm});
            skLineSegment(sketch, "E451", {"start": v(10.99, -11.53) * mm, "end": v(10.97, -11.22) * mm});
            skLineSegment(sketch, "E452", {"start": v(10.97, -11.22) * mm, "end": v(10.79, -11.05) * mm});
            skLineSegment(sketch, "E453", {"start": v(10.79, -11.05) * mm, "end": v(10.78, -10.74) * mm});
            skLineSegment(sketch, "E454", {"start": v(10.78, -10.74) * mm, "end": v(10.57, -10.21) * mm});
            skLineSegment(sketch, "E455", {"start": v(10.57, -10.21) * mm, "end": v(10.62, -9.67) * mm});
            skLineSegment(sketch, "E456", {"start": v(10.62, -9.67) * mm, "end": v(10.67, -9.04) * mm});
            skLineSegment(sketch, "E457", {"start": v(10.67, -9.04) * mm, "end": v(10.51, -8.26) * mm});
            skLineSegment(sketch, "E458", {"start": v(10.51, -8.26) * mm, "end": v(10.59, -7.34) * mm});
            skLineSegment(sketch, "E459", {"start": v(10.59, -7.34) * mm, "end": v(11, -7.03) * mm});
            skLineSegment(sketch, "E460", {"start": v(11, -7.03) * mm, "end": v(10.94, -6.83) * mm});
            skLineSegment(sketch, "E461", {"start": v(10.94, -6.83) * mm, "end": v(11.28, -6.28) * mm});
            skLineSegment(sketch, "E462", {"start": v(11.28, -6.28) * mm, "end": v(11.66, -6.15) * mm});
            skLineSegment(sketch, "E463", {"start": v(11.66, -6.15) * mm, "end": v(11.59, -5.66) * mm});
            skLineSegment(sketch, "E464", {"start": v(11.59, -5.66) * mm, "end": v(11.9, -5.08) * mm});
            skLineSegment(sketch, "E465", {"start": v(11.9, -5.08) * mm, "end": v(12.06, -5) * mm});
            skLineSegment(sketch, "E466", {"start": v(12.06, -5) * mm, "end": v(12.18, -4.83) * mm});
            skLineSegment(sketch, "E467", {"start": v(12.18, -4.83) * mm, "end": v(12.12, -4.62) * mm});
            skLineSegment(sketch, "E468", {"start": v(12.12, -4.62) * mm, "end": v(12.45, -4.23) * mm});
            skLineSegment(sketch, "E469", {"start": v(12.45, -4.23) * mm, "end": v(12.56, -3.73) * mm});
            skLineSegment(sketch, "E470", {"start": v(12.56, -3.73) * mm, "end": v(12.43, -3.35) * mm});
            skLineSegment(sketch, "E471", {"start": v(12.43, -3.35) * mm, "end": v(12.88, -3.15) * mm});
            skLineSegment(sketch, "E472", {"start": v(12.88, -3.15) * mm, "end": v(13.06, -2.2) * mm});
            skLineSegment(sketch, "E473", {"start": v(13.29, -0.87) * mm, "end": v(13.29, -1.54) * mm});
            skLineSegment(sketch, "E474", {"start": v(13.29, -1.54) * mm, "end": v(13.06, -2.2) * mm});
            skLineSegment(sketch, "E475", {"start": v(13.29, -0.87) * mm, "end": v(13.96, -0.41) * mm});
            skLineSegment(sketch, "E476", {"start": v(13.96, -0.41) * mm, "end": v(14, -0.01) * mm});
            skLineSegment(sketch, "E477", {"start": v(14, -0.01) * mm, "end": v(14.08, 0.17) * mm});
            skLineSegment(sketch, "E478", {"start": v(14.08, 0.17) * mm, "end": v(14.07, 0.33) * mm});
            skLineSegment(sketch, "E479", {"start": v(14.07, 0.33) * mm, "end": v(13.9, 0.38) * mm});
            skLineSegment(sketch, "E480", {"start": v(13.9, 0.38) * mm, "end": v(13.61, 0.4) * mm});
            skLineSegment(sketch, "E481", {"start": v(13.61, 0.4) * mm, "end": v(13.22, 1.04) * mm});
            skLineSegment(sketch, "E482", {"start": v(13.22, 1.04) * mm, "end": v(12.9, 2.32) * mm});
            skLineSegment(sketch, "E483", {"start": v(12.9, 2.32) * mm, "end": v(12.49, 2.36) * mm});
            skLineSegment(sketch, "E484", {"start": v(12.49, 2.36) * mm, "end": v(11.62, 2.99) * mm});
            skLineSegment(sketch, "E485", {"start": v(11.62, 2.99) * mm, "end": v(11.43, 3.39) * mm});
            skLineSegment(sketch, "E486", {"start": v(11.43, 3.39) * mm, "end": v(11.68, 4.17) * mm});
            skLineSegment(sketch, "E487", {"start": v(11.68, 4.17) * mm, "end": v(11.83, 4.78) * mm});
            skLineSegment(sketch, "E488", {"start": v(11.83, 4.78) * mm, "end": v(10.82, 5.01) * mm});
            skLineSegment(sketch, "E489", {"start": v(10.82, 5.01) * mm, "end": v(10.78, 5.68) * mm});
            skLineSegment(sketch, "E490", {"start": v(10.78, 5.68) * mm, "end": v(10.19, 6.02) * mm});
            skLineSegment(sketch, "E491", {"start": v(10.19, 6.02) * mm, "end": v(9.38, 6.84) * mm});
            skLineSegment(sketch, "E492", {"start": v(9.38, 6.84) * mm, "end": v(9.07, 8.17) * mm});
            skLineSegment(sketch, "E493", {"start": v(9.07, 8.17) * mm, "end": v(9.16, 8.38) * mm});
            skLineSegment(sketch, "E494", {"start": v(9.16, 8.38) * mm, "end": v(9.32, 8.57) * mm});
            skLineSegment(sketch, "E495", {"start": v(9.32, 8.57) * mm, "end": v(9.3, 8.94) * mm});
            skLineSegment(sketch, "E496", {"start": v(9.3, 8.94) * mm, "end": v(9.7, 9.14) * mm});
            skLineSegment(sketch, "E497", {"start": v(8.6, 8.97) * mm, "end": v(9.16, 8.38) * mm});
            skLineSegment(sketch, "E498", {"start": v(9.7, 9.14) * mm, "end": v(9.7, 9.56) * mm});
            skLineSegment(sketch, "E499", {"start": v(9.7, 9.56) * mm, "end": v(9.98, 9.73) * mm});
            skLineSegment(sketch, "E500", {"start": v(9.98, 9.73) * mm, "end": v(10.05, 10.21) * mm});
            skLineSegment(sketch, "E501", {"start": v(10.05, 10.21) * mm, "end": v(9.73, 10.47) * mm});
            skLineSegment(sketch, "E502", {"start": v(9.73, 10.47) * mm, "end": v(9.86, 10.95) * mm});
            skLineSegment(sketch, "E503", {"start": v(9.86, 10.95) * mm, "end": v(10.91, 11.37) * mm});
            skLineSegment(sketch, "E504", {"start": v(10.91, 11.37) * mm, "end": v(11.25, 12.66) * mm});
            skLineSegment(sketch, "E505", {"start": v(11.25, 12.66) * mm, "end": v(10.78, 13.17) * mm});
            skLineSegment(sketch, "E506", {"start": v(10.78, 13.17) * mm, "end": v(10.76, 13.35) * mm});
            skLineSegment(sketch, "E507", {"start": v(10.76, 13.35) * mm, "end": v(10.37, 13.57) * mm});
            skLineSegment(sketch, "E508", {"start": v(10.37, 13.57) * mm, "end": v(10.38, 13.78) * mm});
            skLineSegment(sketch, "E509", {"start": v(10.23, 14.01) * mm, "end": v(9.62, 14.23) * mm});
            skLineSegment(sketch, "E510", {"start": v(10.23, 14.01) * mm, "end": v(10.38, 13.78) * mm});
            skLineSegment(sketch, "E511", {"start": v(9.62, 14.23) * mm, "end": v(9.36, 14.68) * mm});
            skLineSegment(sketch, "E512", {"start": v(9.36, 14.68) * mm, "end": v(9.34, 15.02) * mm});
            skLineSegment(sketch, "E513", {"start": v(9.34, 15.02) * mm, "end": v(9.54, 15.38) * mm});
            skLineSegment(sketch, "E514", {"start": v(9.54, 15.38) * mm, "end": v(9.53, 15.54) * mm});
            skLineSegment(sketch, "E515", {"start": v(9.53, 15.54) * mm, "end": v(9.27, 15.73) * mm});
            skLineSegment(sketch, "E516", {"start": v(9.27, 15.73) * mm, "end": v(9.13, 16.1) * mm});
            skLineSegment(sketch, "E517", {"start": v(16.58, 6.46) * mm, "end": v(16.1, 12.23) * mm});
            skLineSegment(sketch, "E518", {"start": v(16.1, 12.23) * mm, "end": v(16.68, 12.04) * mm});
            skLineSegment(sketch, "E519", {"start": v(16.68, 12.04) * mm, "end": v(17.33, 12.38) * mm});
            skLineSegment(sketch, "E520", {"start": v(15.3, 14.07) * mm, "end": v(15.45, 13.44) * mm});
            skLineSegment(sketch, "E521", {"start": v(15.45, 13.44) * mm, "end": v(15.74, 13.03) * mm});
            skLineSegment(sketch, "E522", {"start": v(15.74, 13.03) * mm, "end": v(15.95, 12.33) * mm});
            skLineSegment(sketch, "E523", {"start": v(15.95, 12.33) * mm, "end": v(16.1, 12.23) * mm});
            skLineSegment(sketch, "E524", {"start": v(2.16, 29.2) * mm, "end": v(2.23, 30.1) * mm});
            skLineSegment(sketch, "E525", {"start": v(2.23, 30.1) * mm, "end": v(2.62, 30.02) * mm});
            skLineSegment(sketch, "E526", {"start": v(2.62, 30.02) * mm, "end": v(2.86, 28.78) * mm});
            skLineSegment(sketch, "E527", {"start": v(2.86, 28.78) * mm, "end": v(3.1, 28.52) * mm});
            skLineSegment(sketch, "E528", {"start": v(3.1, 28.52) * mm, "end": v(3.63, 28.53) * mm});
            skLineSegment(sketch, "E529", {"start": v(3.63, 28.53) * mm, "end": v(3.64, 28.38) * mm});
            skLineSegment(sketch, "E530", {"start": v(3.64, 28.38) * mm, "end": v(4.32, 28.33) * mm});
            skLineSegment(sketch, "E531", {"start": v(4.32, 28.33) * mm, "end": v(4.3, 28.08) * mm});
            skLineSegment(sketch, "E532", {"start": v(4.3, 28.08) * mm, "end": v(4.95, 28.1) * mm});
            skLineSegment(sketch, "E533", {"start": v(4.95, 28.1) * mm, "end": v(5.08, 28.34) * mm});
            skLineSegment(sketch, "E534", {"start": v(5.08, 28.34) * mm, "end": v(5.3, 28.43) * mm});
            skLineSegment(sketch, "E535", {"start": v(5.3, 28.43) * mm, "end": v(5.47, 28.32) * mm});
            skLineSegment(sketch, "E536", {"start": v(5.47, 28.32) * mm, "end": v(5.77, 28.32) * mm});
            skLineSegment(sketch, "E537", {"start": v(5.77, 28.32) * mm, "end": v(7.03, 27.7) * mm});
            skLineSegment(sketch, "E538", {"start": v(7.03, 27.7) * mm, "end": v(7.26, 27.75) * mm});
            skLineSegment(sketch, "E539", {"start": v(7.26, 27.75) * mm, "end": v(7.29, 27.58) * mm});
            skLineSegment(sketch, "E540", {"start": v(7.29, 27.58) * mm, "end": v(7.6, 27.43) * mm});
            skLineSegment(sketch, "E541", {"start": v(7.6, 27.43) * mm, "end": v(7.74, 27.42) * mm});
            skLineSegment(sketch, "E542", {"start": v(7.74, 27.42) * mm, "end": v(7.78, 27.23) * mm});
            skLineSegment(sketch, "E543", {"start": v(7.78, 27.23) * mm, "end": v(8.07, 27.1) * mm});
            skLineSegment(sketch, "E544", {"start": v(8.07, 27.1) * mm, "end": v(8.32, 27.07) * mm});
            skLineSegment(sketch, "E545", {"start": v(8.32, 27.07) * mm, "end": v(8.53, 27.11) * mm});
            skLineSegment(sketch, "E546", {"start": v(8.53, 27.11) * mm, "end": v(9.05, 27.57) * mm});
            skLineSegment(sketch, "E547", {"start": v(9.05, 27.57) * mm, "end": v(9.25, 27.58) * mm});
            skLineSegment(sketch, "E548", {"start": v(9.25, 27.58) * mm, "end": v(9.35, 27.3) * mm});
            skLineSegment(sketch, "E549", {"start": v(9.35, 27.3) * mm, "end": v(9.52, 27.23) * mm});
            skLineSegment(sketch, "E550", {"start": v(9.52, 27.23) * mm, "end": v(9.66, 27.35) * mm});
            skLineSegment(sketch, "E551", {"start": v(9.66, 27.35) * mm, "end": v(10.56, 27.36) * mm});
            skLineSegment(sketch, "E552", {"start": v(10.56, 27.36) * mm, "end": v(10.76, 27.07) * mm});
            skLineSegment(sketch, "E553", {"start": v(10.76, 27.07) * mm, "end": v(10.93, 27.06) * mm});
            skLineSegment(sketch, "E554", {"start": v(10.93, 27.06) * mm, "end": v(11.02, 27.15) * mm});
            skLineSegment(sketch, "E555", {"start": v(11.02, 27.15) * mm, "end": v(11.42, 27.19) * mm});
            skLineSegment(sketch, "E556", {"start": v(11.42, 27.19) * mm, "end": v(11.2, 26.95) * mm});
            skLineSegment(sketch, "E557", {"start": v(11.2, 26.95) * mm, "end": v(10.74, 26.77) * mm});
            skLineSegment(sketch, "E558", {"start": v(10.74, 26.77) * mm, "end": v(9.5, 26.2) * mm});
            skLineSegment(sketch, "E559", {"start": v(9.5, 26.2) * mm, "end": v(9.13, 25.94) * mm});
            skLineSegment(sketch, "E560", {"start": v(9.13, 25.94) * mm, "end": v(8.9, 25.6) * mm});
            skLineSegment(sketch, "E561", {"start": v(8.9, 25.6) * mm, "end": v(8.52, 25) * mm});
            skLineSegment(sketch, "E562", {"start": v(8.52, 25) * mm, "end": v(8.36, 24.97) * mm});
            skLineSegment(sketch, "E563", {"start": v(8.36, 24.97) * mm, "end": v(7.86, 24.36) * mm});
            skLineSegment(sketch, "E564", {"start": v(7.86, 24.36) * mm, "end": v(7.54, 24.37) * mm});
            skLineSegment(sketch, "E565", {"start": v(7.54, 24.37) * mm, "end": v(7.28, 24.06) * mm});
            skLineSegment(sketch, "E566", {"start": v(7.28, 24.06) * mm, "end": v(7.37, 23.92) * mm});
            skLineSegment(sketch, "E567", {"start": v(7.37, 23.92) * mm, "end": v(7.82, 23.88) * mm});
            skLineSegment(sketch, "E568", {"start": v(7.82, 23.88) * mm, "end": v(9.42, 24.57) * mm});
            skLineSegment(sketch, "E569", {"start": v(9.42, 24.57) * mm, "end": v(9.64, 24.4) * mm});
            skLineSegment(sketch, "E570", {"start": v(9.64, 24.4) * mm, "end": v(9.28, 23.82) * mm});
            skLineSegment(sketch, "E571", {"start": v(9.28, 23.82) * mm, "end": v(9.32, 23.63) * mm});
            skLineSegment(sketch, "E572", {"start": v(9.32, 23.63) * mm, "end": v(9.59, 23.77) * mm});
            skLineSegment(sketch, "E573", {"start": v(9.59, 23.77) * mm, "end": v(9.92, 23.77) * mm});
            skLineSegment(sketch, "E574", {"start": v(9.92, 23.77) * mm, "end": v(10.05, 23.54) * mm});
            skLineSegment(sketch, "E575", {"start": v(10.05, 23.54) * mm, "end": v(10.13, 23.54) * mm});
            skLineSegment(sketch, "E576", {"start": v(10.13, 23.54) * mm, "end": v(10.3, 23.74) * mm});
            skLineSegment(sketch, "E577", {"start": v(10.3, 23.74) * mm, "end": v(10.65, 23.88) * mm});
            skLineSegment(sketch, "E578", {"start": v(10.65, 23.88) * mm, "end": v(11.13, 24.16) * mm});
            skLineSegment(sketch, "E579", {"start": v(11.13, 24.16) * mm, "end": v(11.11, 24.24) * mm});
            skLineSegment(sketch, "E580", {"start": v(11.11, 24.24) * mm, "end": v(11.2, 24.36) * mm});
            skLineSegment(sketch, "E581", {"start": v(11.2, 24.36) * mm, "end": v(11.91, 24.45) * mm});
            skLineSegment(sketch, "E582", {"start": v(11.91, 24.45) * mm, "end": v(12.56, 24.87) * mm});
            skLineSegment(sketch, "E583", {"start": v(12.56, 24.87) * mm, "end": v(12.83, 25.37) * mm});
            skLineSegment(sketch, "E584", {"start": v(12.83, 25.37) * mm, "end": v(13.03, 25.42) * mm});
            skLineSegment(sketch, "E585", {"start": v(13.03, 25.42) * mm, "end": v(13.4, 25.9) * mm});
            skLineSegment(sketch, "E586", {"start": v(13.4, 25.9) * mm, "end": v(13.83, 26.16) * mm});
            skLineSegment(sketch, "E587", {"start": v(13.83, 26.16) * mm, "end": v(14.37, 26.23) * mm});
            skLineSegment(sketch, "E588", {"start": v(14.37, 26.23) * mm, "end": v(14.56, 26.12) * mm});
            skLineSegment(sketch, "E589", {"start": v(14.56, 26.12) * mm, "end": v(14.52, 25.98) * mm});
            skLineSegment(sketch, "E590", {"start": v(14.52, 25.98) * mm, "end": v(14.13, 25.9) * mm});
            skLineSegment(sketch, "E591", {"start": v(14.13, 25.9) * mm, "end": v(13.93, 25.53) * mm});
            skLineSegment(sketch, "E592", {"start": v(13.93, 25.53) * mm, "end": v(13.69, 25.4) * mm});
            skLineSegment(sketch, "E593", {"start": v(13.69, 25.4) * mm, "end": v(13.65, 25.23) * mm});
            skLineSegment(sketch, "E594", {"start": v(13.65, 25.23) * mm, "end": v(13.33, 24.78) * mm});
            skLineSegment(sketch, "E595", {"start": v(13.33, 24.78) * mm, "end": v(13.37, 24.52) * mm});
            skLineSegment(sketch, "E596", {"start": v(13.37, 24.52) * mm, "end": v(13.43, 24.46) * mm});
            skLineSegment(sketch, "E597", {"start": v(13.43, 24.46) * mm, "end": v(13.93, 24.93) * mm});
            skLineSegment(sketch, "E598", {"start": v(13.93, 24.93) * mm, "end": v(14.07, 24.78) * mm});
            skLineSegment(sketch, "E599", {"start": v(14.07, 24.78) * mm, "end": v(14.8, 24.6) * mm});
            skLineSegment(sketch, "E600", {"start": v(14.8, 24.6) * mm, "end": v(15.26, 23.94) * mm});
            skLineSegment(sketch, "E601", {"start": v(15.26, 23.94) * mm, "end": v(15.75, 23.95) * mm});
            skLineSegment(sketch, "E602", {"start": v(29.76, 15.36) * mm, "end": v(29.21, 14.87) * mm});
            skLineSegment(sketch, "E603", {"start": v(29.21, 14.87) * mm, "end": v(28.57, 14.43) * mm});
            skLineSegment(sketch, "E604", {"start": v(28.57, 14.43) * mm, "end": v(29.41, 8.98) * mm});
            skLineSegment(sketch, "E605", {"start": v(29.41, 8.98) * mm, "end": v(38, 10.58) * mm});
            skLineSegment(sketch, "E606", {"start": v(38, 10.58) * mm, "end": v(38.85, 7.6) * mm});
            skLineSegment(sketch, "E607", {"start": v(38.85, 7.6) * mm, "end": v(40.04, 7.82) * mm});
            skLineSegment(sketch, "E608", {"start": v(44.17, 16.2) * mm, "end": v(43.85, 17.71) * mm});
            skLineSegment(sketch, "E609", {"start": v(43.85, 17.71) * mm, "end": v(44.5, 17.9) * mm});
            skLineSegment(sketch, "E610", {"start": v(44.5, 17.9) * mm, "end": v(45.32, 16.86) * mm});
            skLineSegment(sketch, "E611", {"start": v(45.32, 16.86) * mm, "end": v(44.86, 16.58) * mm});
            skLineSegment(sketch, "E612", {"start": v(44.86, 16.58) * mm, "end": v(44.75, 16.41) * mm});
            skLineSegment(sketch, "E613", {"start": v(44.75, 16.41) * mm, "end": v(44.17, 16.2) * mm});
            skLineSegment(sketch, "E614", {"start": v(44.17, 16.2) * mm, "end": v(44.1, 16.06) * mm});
            skLineSegment(sketch, "E615", {"start": v(44.1, 16.06) * mm, "end": v(42.42, 15.45) * mm});
            skLineSegment(sketch, "E616", {"start": v(42.42, 15.45) * mm, "end": v(42.36, 15.51) * mm});
            skLineSegment(sketch, "E617", {"start": v(42.36, 15.51) * mm, "end": v(41.75, 14.94) * mm});
            skLineSegment(sketch, "E618", {"start": v(41.75, 14.94) * mm, "end": v(41.18, 14.59) * mm});
            skLineSegment(sketch, "E619", {"start": v(43.85, 17.71) * mm, "end": v(40.82, 17.1) * mm});
            skLineSegment(sketch, "E620", {"start": v(40.82, 18.87) * mm, "end": v(44.33, 19.7) * mm});
            skLineSegment(sketch, "E621", {"start": v(44.33, 19.7) * mm, "end": v(44.58, 20.05) * mm});
            skLineSegment(sketch, "E622", {"start": v(44.58, 20.05) * mm, "end": v(44.98, 20.2) * mm});
            skLineSegment(sketch, "E623", {"start": v(44.98, 20.2) * mm, "end": v(45.26, 19.77) * mm});
            skLineSegment(sketch, "E624", {"start": v(45.26, 19.77) * mm, "end": v(45.02, 19.04) * mm});
            skLineSegment(sketch, "E625", {"start": v(45.02, 19.04) * mm, "end": v(45.22, 18.74) * mm});
            skLineSegment(sketch, "E626", {"start": v(45.22, 18.74) * mm, "end": v(45.33, 18.83) * mm});
            skLineSegment(sketch, "E627", {"start": v(45.33, 18.83) * mm, "end": v(45.57, 18.77) * mm});
            skLineSegment(sketch, "E628", {"start": v(45.57, 18.77) * mm, "end": v(46.18, 17.87) * mm});
            skLineSegment(sketch, "E629", {"start": v(46.18, 17.87) * mm, "end": v(46.65, 17.82) * mm});
            skLineSegment(sketch, "E630", {"start": v(46.65, 17.82) * mm, "end": v(46.9, 17.95) * mm});
            skLineSegment(sketch, "E631", {"start": v(46.9, 17.95) * mm, "end": v(47.02, 18.08) * mm});
            skLineSegment(sketch, "E632", {"start": v(45.32, 16.86) * mm, "end": v(45.63, 17) * mm});
            skLineSegment(sketch, "E633", {"start": v(45.63, 17) * mm, "end": v(45.6, 17.26) * mm});
            skLineSegment(sketch, "E634", {"start": v(45.6, 17.26) * mm, "end": v(46, 17.54) * mm});
            skLineSegment(sketch, "E635", {"start": v(46, 17.54) * mm, "end": v(46.11, 17.06) * mm});
            skLineSegment(sketch, "E636", {"start": v(46.11, 17.06) * mm, "end": v(46.36, 17.34) * mm});
            skLineSegment(sketch, "E637", {"start": v(46.36, 17.34) * mm, "end": v(46.69, 17.54) * mm});
            skLineSegment(sketch, "E638", {"start": v(46.69, 17.54) * mm, "end": v(47.07, 17.68) * mm});
            skLineSegment(sketch, "E639", {"start": v(47.07, 17.68) * mm, "end": v(47.3, 17.75) * mm});
            skLineSegment(sketch, "E640", {"start": v(47.3, 17.75) * mm, "end": v(47.25, 18.16) * mm});
            skLineSegment(sketch, "E641", {"start": v(47.25, 18.16) * mm, "end": v(47.07, 18.4) * mm});
            skLineSegment(sketch, "E642", {"start": v(47.02, 18.08) * mm, "end": v(47.07, 18.4) * mm});
            skLineSegment(sketch, "E643", {"start": v(39.46, 24.13) * mm, "end": v(42.4, 24.95) * mm});
            skLineSegment(sketch, "E644", {"start": v(42.4, 24.95) * mm, "end": v(42.52, 24.67) * mm});
            skLineSegment(sketch, "E645", {"start": v(42.52, 24.67) * mm, "end": v(42.42, 24.26) * mm});
            skLineSegment(sketch, "E646", {"start": v(42.42, 24.26) * mm, "end": v(42.69, 23.94) * mm});
            skLineSegment(sketch, "E647", {"start": v(42.69, 23.94) * mm, "end": v(42.63, 23.86) * mm});
            skLineSegment(sketch, "E648", {"start": v(42.63, 23.86) * mm, "end": v(42.7, 23.7) * mm});
            skLineSegment(sketch, "E649", {"start": v(42.7, 23.7) * mm, "end": v(42.23, 23.18) * mm});
            skLineSegment(sketch, "E650", {"start": v(42.23, 23.18) * mm, "end": v(41.98, 23.07) * mm});
            skLineSegment(sketch, "E651", {"start": v(41.98, 23.07) * mm, "end": v(41.98, 22.87) * mm});
            skLineSegment(sketch, "E652", {"start": v(41.98, 22.87) * mm, "end": v(42.09, 22.75) * mm});
            skLineSegment(sketch, "E653", {"start": v(42.09, 22.75) * mm, "end": v(41.98, 20.18) * mm});
            skLineSegment(sketch, "E654", {"start": v(41.98, 20.18) * mm, "end": v(42.09, 20.14) * mm});
            skLineSegment(sketch, "E655", {"start": v(42.09, 20.14) * mm, "end": v(42.07, 19.61) * mm});
            skLineSegment(sketch, "E656", {"start": v(42.07, 19.61) * mm, "end": v(42.07, 19.38) * mm});
            skLineSegment(sketch, "E657", {"start": v(42.07, 19.38) * mm, "end": v(42.26, 19.2) * mm});
            skLineSegment(sketch, "E658", {"start": v(13.9, 0.38) * mm, "end": v(14.14, 0.73) * mm});
            skLineSegment(sketch, "E659", {"start": v(14.14, 0.73) * mm, "end": v(14.44, 0.92) * mm});
            skLineSegment(sketch, "E660", {"start": v(14.44, 0.92) * mm, "end": v(15.25, 0.63) * mm});
            skLineSegment(sketch, "E661", {"start": v(15.25, 0.63) * mm, "end": v(15.36, 0.8) * mm});
            skLineSegment(sketch, "E662", {"start": v(15.36, 0.8) * mm, "end": v(15.2, 1.05) * mm});
            skLineSegment(sketch, "E663", {"start": v(15.2, 1.05) * mm, "end": v(15.23, 1.43) * mm});
            skLineSegment(sketch, "E664", {"start": v(15.23, 1.43) * mm, "end": v(15.62, 1.62) * mm});
            skLineSegment(sketch, "E665", {"start": v(15.62, 1.62) * mm, "end": v(15.93, 1.78) * mm});
            skLineSegment(sketch, "E666", {"start": v(15.93, 1.78) * mm, "end": v(15.72, 2.14) * mm});
            skLineSegment(sketch, "E667", {"start": v(15.72, 2.14) * mm, "end": v(15.93, 2.35) * mm});
            skLineSegment(sketch, "E668", {"start": v(15.93, 2.35) * mm, "end": v(16, 2.63) * mm});
            skLineSegment(sketch, "E669", {"start": v(16, 2.63) * mm, "end": v(16.07, 3.6) * mm});
            skLineSegment(sketch, "E670", {"start": v(16.07, 3.6) * mm, "end": v(16.76, 4.67) * mm});
            skLineSegment(sketch, "E671", {"start": v(16.76, 4.67) * mm, "end": v(16.7, 5.42) * mm});
            skLineSegment(sketch, "E672", {"start": v(16.7, 5.42) * mm, "end": v(16.45, 5.8) * mm});
            skLineSegment(sketch, "E673", {"start": v(16.45, 5.8) * mm, "end": v(16.58, 6.46) * mm});
            skLineSegment(sketch, "E674", {"start": v(16, 2.63) * mm, "end": v(17.3, 2.95) * mm});
            skLineSegment(sketch, "E675", {"start": v(17.3, 2.95) * mm, "end": v(17.75, 2.61) * mm});
            skLineSegment(sketch, "E676", {"start": v(17.75, 2.61) * mm, "end": v(17.89, 2.98) * mm});
            skLineSegment(sketch, "E677", {"start": v(17.89, 2.98) * mm, "end": v(18.25, 3.16) * mm});
            skLineSegment(sketch, "E678", {"start": v(18.25, 3.16) * mm, "end": v(18.57, 2.88) * mm});
            skLineSegment(sketch, "E679", {"start": v(18.57, 2.88) * mm, "end": v(18.74, 2.9) * mm});
            skLineSegment(sketch, "E680", {"start": v(18.74, 2.9) * mm, "end": v(18.8, 3.33) * mm});
            skLineSegment(sketch, "E681", {"start": v(18.8, 3.33) * mm, "end": v(19.19, 3.58) * mm});
            skLineSegment(sketch, "E682", {"start": v(19.19, 3.58) * mm, "end": v(19.33, 3.4) * mm});
            skLineSegment(sketch, "E683", {"start": v(19.33, 3.4) * mm, "end": v(19.83, 3.38) * mm});
            skLineSegment(sketch, "E684", {"start": v(19.83, 3.38) * mm, "end": v(19.87, 3.95) * mm});
            skLineSegment(sketch, "E685", {"start": v(19.87, 3.95) * mm, "end": v(20.75, 4.7) * mm});
            skLineSegment(sketch, "E686", {"start": v(20.75, 4.7) * mm, "end": v(20.77, 5.23) * mm});
            skLineSegment(sketch, "E687", {"start": v(20.77, 5.23) * mm, "end": v(21.13, 5.21) * mm});
            skLineSegment(sketch, "E688", {"start": v(21.13, 5.21) * mm, "end": v(21.83, 5.62) * mm});
            skLineSegment(sketch, "E689", {"start": v(21.83, 5.62) * mm, "end": v(21.81, 5.85) * mm});
            skLineSegment(sketch, "E690", {"start": v(21.81, 5.85) * mm, "end": v(21.55, 6.05) * mm});
            skLineSegment(sketch, "E691", {"start": v(21.55, 6.05) * mm, "end": v(21.7, 6.25) * mm});
            skLineSegment(sketch, "E692", {"start": v(23.88, -3.62) * mm, "end": v(23.8, -3.01) * mm});
            skLineSegment(sketch, "E693", {"start": v(23.8, -3.01) * mm, "end": v(24.38, -2.84) * mm});
            skLineSegment(sketch, "E694", {"start": v(24.38, -2.84) * mm, "end": v(24.35, -2.5) * mm});
            skLineSegment(sketch, "E695", {"start": v(24.35, -2.5) * mm, "end": v(24.86, -2.08) * mm});
            skLineSegment(sketch, "E696", {"start": v(24.86, -2.08) * mm, "end": v(25.36, -2.05) * mm});
            skLineSegment(sketch, "E697", {"start": v(25.36, -2.05) * mm, "end": v(25.72, -1.6) * mm});
            skLineSegment(sketch, "E698", {"start": v(25.72, -1.6) * mm, "end": v(26.28, -1.33) * mm});
            skLineSegment(sketch, "E699", {"start": v(26.28, -1.33) * mm, "end": v(26.31, -1) * mm});
            skLineSegment(sketch, "E700", {"start": v(26.31, -1) * mm, "end": v(26.81, -0.54) * mm});
            skLineSegment(sketch, "E701", {"start": v(26.81, -0.54) * mm, "end": v(26.93, -0.71) * mm});
            skLineSegment(sketch, "E702", {"start": v(26.93, -0.71) * mm, "end": v(27.15, -0.74) * mm});
            skLineSegment(sketch, "E703", {"start": v(27.15, -0.74) * mm, "end": v(27.37, -0.24) * mm});
            skLineSegment(sketch, "E704", {"start": v(27.37, -0.24) * mm, "end": v(27.85, -0.24) * mm});
            skLineSegment(sketch, "E705", {"start": v(27.85, -0.24) * mm, "end": v(28.02, 0.15) * mm});
            skLineSegment(sketch, "E706", {"start": v(28.02, 0.15) * mm, "end": v(28.35, 0.38) * mm});
            skLineSegment(sketch, "E707", {"start": v(28.35, 0.38) * mm, "end": v(28.4, 0.93) * mm});
            skLineSegment(sketch, "E708", {"start": v(24.8, 0.46) * mm, "end": v(25.99, 1.28) * mm});
            skLineSegment(sketch, "E709", {"start": v(25.99, 1.28) * mm, "end": v(25.97, 1.56) * mm});
            skLineSegment(sketch, "E710", {"start": v(25.97, 1.56) * mm, "end": v(27.45, 3.14) * mm});
            skLineSegment(sketch, "E711", {"start": v(27.45, 3.14) * mm, "end": v(26.52, 3.97) * mm});
            skLineSegment(sketch, "E712", {"start": v(26.52, 3.97) * mm, "end": v(26.46, 4.24) * mm});
            skLineSegment(sketch, "E713", {"start": v(26.46, 4.24) * mm, "end": v(26.13, 5.17) * mm});
            skLineSegment(sketch, "E714", {"start": v(26.13, 5.17) * mm, "end": v(25.51, 5.55) * mm});
            skLineSegment(sketch, "E715", {"start": v(25.51, 5.55) * mm, "end": v(25.36, 5.92) * mm});
            skLineSegment(sketch, "E716", {"start": v(25.36, 5.92) * mm, "end": v(24.74, 5.43) * mm});
            skLineSegment(sketch, "E717", {"start": v(24.74, 5.43) * mm, "end": v(24.58, 5.59) * mm});
            skLineSegment(sketch, "E718", {"start": v(24.58, 5.59) * mm, "end": v(24.27, 5.65) * mm});
            skLineSegment(sketch, "E719", {"start": v(24.27, 5.65) * mm, "end": v(23.91, 5.43) * mm});
            skLineSegment(sketch, "E720", {"start": v(23.91, 5.43) * mm, "end": v(23.62, 5.7) * mm});
            skLineSegment(sketch, "E721", {"start": v(23.62, 5.7) * mm, "end": v(22.98, 5.73) * mm});
            skLineSegment(sketch, "E722", {"start": v(22.98, 5.73) * mm, "end": v(22.69, 6.22) * mm});
            skLineSegment(sketch, "E723", {"start": v(22.69, 6.22) * mm, "end": v(22.45, 6.34) * mm});
            skLineSegment(sketch, "E724", {"start": v(22.45, 6.34) * mm, "end": v(21.7, 6.25) * mm});
            skLineSegment(sketch, "E725", {"start": v(38, 10.58) * mm, "end": v(38.43, 10.88) * mm});
            skLineSegment(sketch, "E726", {"start": v(38.43, 10.88) * mm, "end": v(39, 11.1) * mm});
            skLineSegment(sketch, "E727", {"start": v(39, 11.1) * mm, "end": v(39.68, 12.03) * mm});
            skLineSegment(sketch, "E728", {"start": v(39.68, 12.03) * mm, "end": v(39.07, 12.56) * mm});
            skLineSegment(sketch, "E729", {"start": v(39.07, 12.56) * mm, "end": v(38.93, 12.87) * mm});
            skLineSegment(sketch, "E730", {"start": v(38.93, 12.87) * mm, "end": v(38.67, 12.86) * mm});
            skLineSegment(sketch, "E731", {"start": v(38.67, 12.86) * mm, "end": v(38.53, 13.32) * mm});
            skLineSegment(sketch, "E732", {"start": v(38.53, 13.32) * mm, "end": v(38.78, 13.42) * mm});
            skLineSegment(sketch, "E733", {"start": v(38.78, 13.42) * mm, "end": v(38.77, 13.69) * mm});
            skLineSegment(sketch, "E734", {"start": v(38.77, 13.69) * mm, "end": v(38.58, 13.82) * mm});
            skLineSegment(sketch, "E735", {"start": v(38.58, 13.82) * mm, "end": v(38.85, 14.3) * mm});
            skLineSegment(sketch, "E736", {"start": v(38.85, 14.3) * mm, "end": v(38.92, 14.7) * mm});
            skLineSegment(sketch, "E737", {"start": v(38.92, 14.7) * mm, "end": v(39.13, 14.92) * mm});
            skLineSegment(sketch, "E738", {"start": v(38.64, 10.96) * mm, "end": v(38.55, 10.38) * mm});
            skLineSegment(sketch, "E739", {"start": v(38.55, 10.38) * mm, "end": v(38.87, 10) * mm});
            skLineSegment(sketch, "E740", {"start": v(38.87, 10) * mm, "end": v(39.52, 9.66) * mm});
            skLineSegment(sketch, "E741", {"start": v(39.52, 9.66) * mm, "end": v(40, 9.59) * mm});
            skLineSegment(sketch, "E742", {"start": v(40, 9.59) * mm, "end": v(40, 9.38) * mm});
            skLineSegment(sketch, "E743", {"start": v(40, 9.38) * mm, "end": v(39.92, 9.32) * mm});
            skLineSegment(sketch, "E744", {"start": v(39.92, 9.32) * mm, "end": v(39.93, 9) * mm});
            skLineSegment(sketch, "E745", {"start": v(39.93, 9) * mm, "end": v(40.26, 9.24) * mm});
            skLineSegment(sketch, "E746", {"start": v(40.26, 9.24) * mm, "end": v(40.35, 9.73) * mm});
            skLineSegment(sketch, "E747", {"start": v(40.35, 9.73) * mm, "end": v(40.77, 10.44) * mm});
            skLineSegment(sketch, "E748", {"start": v(40.77, 10.44) * mm, "end": v(41.07, 11.18) * mm});
            skLineSegment(sketch, "E749", {"start": v(41.07, 11.18) * mm, "end": v(41.04, 11.74) * mm});
            skLineSegment(sketch, "E750", {"start": v(41.04, 11.74) * mm, "end": v(41.04, 12.81) * mm});
            skLineSegment(sketch, "E751", {"start": v(41.04, 12.81) * mm, "end": v(40.87, 13.1) * mm});
            skLineSegment(sketch, "E752", {"start": v(40.87, 13.1) * mm, "end": v(40.47, 12.97) * mm});
            skLineSegment(sketch, "E753", {"start": v(40.47, 12.97) * mm, "end": v(40.4, 13.08) * mm});
            skLineSegment(sketch, "E754", {"start": v(40.4, 13.08) * mm, "end": v(40.72, 13.34) * mm});
            skLineSegment(sketch, "E755", {"start": v(40.72, 13.34) * mm, "end": v(40.77, 13.52) * mm});
            skLineSegment(sketch, "E756", {"start": v(26.13, 5.17) * mm, "end": v(26.47, 5.3) * mm});
            skLineSegment(sketch, "E757", {"start": v(26.47, 5.3) * mm, "end": v(26.54, 5.67) * mm});
            skLineSegment(sketch, "E758", {"start": v(26.54, 5.67) * mm, "end": v(26.7, 5.72) * mm});
            skLineSegment(sketch, "E759", {"start": v(26.7, 5.72) * mm, "end": v(26.78, 6.72) * mm});
            skLineSegment(sketch, "E760", {"start": v(26.78, 6.72) * mm, "end": v(27, 6.77) * mm});
            skLineSegment(sketch, "E761", {"start": v(27, 6.77) * mm, "end": v(27.18, 6.52) * mm});
            skLineSegment(sketch, "E762", {"start": v(27.18, 6.52) * mm, "end": v(27.38, 6.62) * mm});
            skLineSegment(sketch, "E763", {"start": v(27.38, 6.62) * mm, "end": v(27.4, 6.76) * mm});
            skLineSegment(sketch, "E764", {"start": v(27.4, 6.76) * mm, "end": v(27.22, 7.04) * mm});
            skLineSegment(sketch, "E765", {"start": v(27.22, 7.04) * mm, "end": v(27.82, 7.92) * mm});
            skLineSegment(sketch, "E766", {"start": v(27.82, 7.92) * mm, "end": v(28, 7.83) * mm});
            skLineSegment(sketch, "E767", {"start": v(28, 7.83) * mm, "end": v(28.86, 8.77) * mm});
            skLineSegment(sketch, "E768", {"start": v(28.86, 8.77) * mm, "end": v(28.94, 10.52) * mm});
            skLineSegment(sketch, "E769", {"start": v(28.94, 10.52) * mm, "end": v(28.78, 10.94) * mm});
            skLineSegment(sketch, "E770", {"start": v(28.78, 10.94) * mm, "end": v(29.08, 11.11) * mm});
            skLineSegment(sketch, "E771", {"start": v(23.37, 13) * mm, "end": v(24, 12.75) * mm});
            skLineSegment(sketch, "E772", {"start": v(24, 12.75) * mm, "end": v(24.6, 12.78) * mm});
            skLineSegment(sketch, "E773", {"start": v(24.6, 12.78) * mm, "end": v(25.01, 12.46) * mm});
            skLineSegment(sketch, "E774", {"start": v(25.01, 12.46) * mm, "end": v(25.25, 12.5) * mm});
            skLineSegment(sketch, "E775", {"start": v(25.25, 12.5) * mm, "end": v(25.86, 12.79) * mm});
            skLineSegment(sketch, "E776", {"start": v(25.86, 12.79) * mm, "end": v(26.55, 12.9) * mm});
            skLineSegment(sketch, "E777", {"start": v(26.55, 12.9) * mm, "end": v(27.36, 13.73) * mm});
            skLineSegment(sketch, "E778", {"start": v(27.36, 13.73) * mm, "end": v(28.57, 14.43) * mm});
            skLineSegment(sketch, "E779", {"start": v(9.13, 16.1) * mm, "end": v(9, 16.92) * mm});
            skLineSegment(sketch, "E780", {"start": v(9, 16.92) * mm, "end": v(8.87, 17.22) * mm});
            skLineSegment(sketch, "E781", {"start": v(8.87, 17.22) * mm, "end": v(8.11, 17.61) * mm});
            skLineSegment(sketch, "E782", {"start": v(8.11, 17.61) * mm, "end": v(7.68, 18.31) * mm});
            skLineSegment(sketch, "E783", {"start": v(7.68, 18.31) * mm, "end": v(7.16, 18.36) * mm});
            skLineSegment(sketch, "E784", {"start": v(7.16, 18.36) * mm, "end": v(7.03, 18.74) * mm});
            skLineSegment(sketch, "E785", {"start": v(7.03, 18.74) * mm, "end": v(6.76, 18.73) * mm});
            skLineSegment(sketch, "E786", {"start": v(6.76, 18.73) * mm, "end": v(6.45, 19) * mm});
            skLineSegment(sketch, "E787", {"start": v(6.45, 19) * mm, "end": v(6.33, 20.26) * mm});
            skLineSegment(sketch, "E788", {"start": v(6.33, 20.26) * mm, "end": v(6.5, 20.5) * mm});
            skLineSegment(sketch, "E789", {"start": v(6.5, 20.5) * mm, "end": v(6.45, 20.94) * mm});
            skLineSegment(sketch, "E790", {"start": v(6.45, 20.94) * mm, "end": v(6.1, 21.15) * mm});
            skLineSegment(sketch, "E791", {"start": v(6.1, 21.15) * mm, "end": v(6.37, 21.87) * mm});
            skLineSegment(sketch, "E792", {"start": v(6.37, 21.87) * mm, "end": v(7.08, 22.38) * mm});
            skLineSegment(sketch, "E793", {"start": v(7.08, 22.38) * mm, "end": v(7.08, 23.68) * mm});
            skLineSegment(sketch, "E794", {"start": v(7.08, 23.68) * mm, "end": v(7.37, 23.92) * mm});
            skLineSegment(sketch, "E795", {"start": v(10.3, 23.74) * mm, "end": v(10.72, 23.09) * mm});
            skLineSegment(sketch, "E796", {"start": v(10.72, 23.09) * mm, "end": v(11.41, 23.02) * mm});
            skLineSegment(sketch, "E797", {"start": v(11.41, 23.02) * mm, "end": v(12.57, 22.72) * mm});
            skLineSegment(sketch, "E798", {"start": v(12.57, 22.72) * mm, "end": v(12.84, 22.54) * mm});
            skLineSegment(sketch, "E799", {"start": v(12.84, 22.54) * mm, "end": v(14.25, 22.3) * mm});
            skLineSegment(sketch, "E800", {"start": v(14.25, 22.3) * mm, "end": v(14.34, 22.02) * mm});
            skLineSegment(sketch, "E801", {"start": v(14.34, 22.02) * mm, "end": v(14.76, 21.9) * mm});
            skLineSegment(sketch, "E802", {"start": v(14.76, 21.9) * mm, "end": v(14.88, 20.82) * mm});
            skLineSegment(sketch, "E803", {"start": v(14.88, 20.82) * mm, "end": v(15.23, 20.5) * mm});
            skLineSegment(sketch, "E804", {"start": v(15.75, 23.95) * mm, "end": v(15.9, 24.05) * mm});
            skLineSegment(sketch, "E805", {"start": v(15.9, 24.05) * mm, "end": v(16.17, 23.83) * mm});
            skLineSegment(sketch, "E806", {"start": v(16.17, 23.83) * mm, "end": v(16.41, 23.98) * mm});
            skLineSegment(sketch, "E807", {"start": v(16.41, 23.98) * mm, "end": v(16.57, 23.91) * mm});
            skLineSegment(sketch, "E808", {"start": v(16.57, 23.91) * mm, "end": v(17.18, 24.45) * mm});
            skLineSegment(sketch, "E809", {"start": v(17.18, 24.45) * mm, "end": v(17.6, 24.56) * mm});
            skLineSegment(sketch, "E810", {"start": v(17.6, 24.56) * mm, "end": v(18.21, 24.6) * mm});
            skLineSegment(sketch, "E811", {"start": v(18.21, 24.6) * mm, "end": v(19, 24.93) * mm});
            skLineSegment(sketch, "E812", {"start": v(19, 24.93) * mm, "end": v(19.19, 24.9) * mm});
            skLineSegment(sketch, "E813", {"start": v(19.19, 24.9) * mm, "end": v(19.17, 24.32) * mm});
            skLineSegment(sketch, "E814", {"start": v(19.17, 24.32) * mm, "end": v(19.62, 24.18) * mm});
            skLineSegment(sketch, "E815", {"start": v(19.62, 24.18) * mm, "end": v(20.48, 24.43) * mm});
            skLineSegment(sketch, "E816", {"start": v(20.48, 24.43) * mm, "end": v(20.57, 24.55) * mm});
            skLineSegment(sketch, "E817", {"start": v(20.57, 24.55) * mm, "end": v(20.74, 24.48) * mm});
            skLineSegment(sketch, "E818", {"start": v(20.74, 24.48) * mm, "end": v(20.74, 23.76) * mm});
            skLineSegment(sketch, "E819", {"start": v(20.74, 23.76) * mm, "end": v(21.27, 23.21) * mm});
            skLineSegment(sketch, "E820", {"start": v(21.27, 23.21) * mm, "end": v(20.81, 23.22) * mm});
            skLineSegment(sketch, "E821", {"start": v(20.81, 23.22) * mm, "end": v(20.6, 23.16) * mm});
            skLineSegment(sketch, "E822", {"start": v(20.6, 23.16) * mm, "end": v(20.27, 23.2) * mm});
            skLineSegment(sketch, "E823", {"start": v(20.27, 23.2) * mm, "end": v(19.95, 23.01) * mm});
            skLineSegment(sketch, "E824", {"start": v(19.95, 23.01) * mm, "end": v(19.23, 23.13) * mm});
            skLineSegment(sketch, "E825", {"start": v(19.23, 23.13) * mm, "end": v(18.53, 23.13) * mm});
            skLineSegment(sketch, "E826", {"start": v(18.53, 23.13) * mm, "end": v(18.33, 22.85) * mm});
            skLineSegment(sketch, "E827", {"start": v(18.33, 22.85) * mm, "end": v(17.31, 22.74) * mm});
            skLineSegment(sketch, "E828", {"start": v(17.31, 22.74) * mm, "end": v(17.1, 22.31) * mm});
            skLineSegment(sketch, "E829", {"start": v(17.1, 22.31) * mm, "end": v(17, 22.26) * mm});
            skLineSegment(sketch, "E830", {"start": v(17, 22.26) * mm, "end": v(16.75, 22.41) * mm});
            skLineSegment(sketch, "E831", {"start": v(16.75, 22.41) * mm, "end": v(16.24, 22.18) * mm});
            skLineSegment(sketch, "E832", {"start": v(16.24, 22.18) * mm, "end": v(16.02, 22.36) * mm});
            skLineSegment(sketch, "E833", {"start": v(16.02, 22.36) * mm, "end": v(15.96, 22.35) * mm});
            skLineSegment(sketch, "E834", {"start": v(15.96, 22.35) * mm, "end": v(15.23, 20.5) * mm});
            skLineSegment(sketch, "E835", {"start": v(15.23, 20.5) * mm, "end": v(14.53, 19.36) * mm});
            skLineSegment(sketch, "E836", {"start": v(14.53, 19.36) * mm, "end": v(14.56, 19.13) * mm});
            skLineSegment(sketch, "E837", {"start": v(14.56, 19.13) * mm, "end": v(14.74, 19.07) * mm});
            skLineSegment(sketch, "E838", {"start": v(14.74, 19.07) * mm, "end": v(14.81, 19.34) * mm});
            skLineSegment(sketch, "E839", {"start": v(14.81, 19.34) * mm, "end": v(15.32, 19.77) * mm});
            skLineSegment(sketch, "E840", {"start": v(15.32, 19.77) * mm, "end": v(16.13, 20.99) * mm});
            skLineSegment(sketch, "E841", {"start": v(16.13, 20.99) * mm, "end": v(16.22, 20.7) * mm});
            skLineSegment(sketch, "E842", {"start": v(16.22, 20.7) * mm, "end": v(15.54, 19.3) * mm});
            skLineSegment(sketch, "E843", {"start": v(15.54, 19.3) * mm, "end": v(15.43, 18.64) * mm});
            skLineSegment(sketch, "E844", {"start": v(15.43, 18.64) * mm, "end": v(15.52, 18.54) * mm});
            skLineSegment(sketch, "E845", {"start": v(15.52, 18.54) * mm, "end": v(15.55, 18.28) * mm});
            skLineSegment(sketch, "E846", {"start": v(15.55, 18.28) * mm, "end": v(15.23, 17.83) * mm});
            skLineSegment(sketch, "E847", {"start": v(15.23, 17.83) * mm, "end": v(15.39, 16.95) * mm});
            skLineSegment(sketch, "E848", {"start": v(15.39, 16.95) * mm, "end": v(15.04, 15.99) * mm});
            skLineSegment(sketch, "E849", {"start": v(15.04, 15.99) * mm, "end": v(15.17, 15.6) * mm});
            skLineSegment(sketch, "E850", {"start": v(15.17, 15.6) * mm, "end": v(15.22, 15) * mm});
            skLineSegment(sketch, "E851", {"start": v(15.22, 15) * mm, "end": v(15.41, 14.57) * mm});
            skLineSegment(sketch, "E852", {"start": v(15.41, 14.57) * mm, "end": v(15.3, 14.07) * mm});
            skLineSegment(sketch, "E853", {"start": v(44.98, 20.2) * mm, "end": v(45.14, 20.76) * mm});
            skLineSegment(sketch, "E854", {"start": v(45.14, 20.76) * mm, "end": v(44.84, 20.88) * mm});
            skLineSegment(sketch, "E855", {"start": v(44.84, 20.88) * mm, "end": v(44.83, 21.22) * mm});
            skLineSegment(sketch, "E856", {"start": v(44.83, 21.22) * mm, "end": v(44.43, 21.32) * mm});
            skLineSegment(sketch, "E857", {"start": v(44.43, 21.32) * mm, "end": v(42.98, 25.8) * mm});
            skLineSegment(sketch, "E858", {"start": v(42.98, 25.8) * mm, "end": v(42.92, 25.54) * mm});
            skLineSegment(sketch, "E859", {"start": v(42.92, 25.54) * mm, "end": v(42.71, 25.71) * mm});
            skLineSegment(sketch, "E860", {"start": v(42.71, 25.71) * mm, "end": v(42.6, 25.67) * mm});
            skLineSegment(sketch, "E861", {"start": v(42.6, 25.67) * mm, "end": v(42.4, 24.95) * mm});
            skLineSegment(sketch, "E862", {"start": v(42.98, 25.8) * mm, "end": v(43.13, 25.84) * mm});
            skLineSegment(sketch, "E863", {"start": v(43.13, 25.84) * mm, "end": v(43.5, 25.78) * mm});
            skLineSegment(sketch, "E864", {"start": v(43.5, 25.78) * mm, "end": v(43.59, 26.73) * mm});
            skLineSegment(sketch, "E865", {"start": v(43.59, 26.73) * mm, "end": v(44.04, 27.76) * mm});
            skLineSegment(sketch, "E866", {"start": v(44.04, 27.76) * mm, "end": v(43.82, 28) * mm});
            skLineSegment(sketch, "E867", {"start": v(43.82, 28) * mm, "end": v(43.82, 28.64) * mm});
            skLineSegment(sketch, "E868", {"start": v(43.82, 28.64) * mm, "end": v(44, 28.97) * mm});
            skLineSegment(sketch, "E869", {"start": v(44, 28.97) * mm, "end": v(44, 29.83) * mm});
            skLineSegment(sketch, "E870", {"start": v(44, 29.83) * mm, "end": v(44.67, 31.66) * mm});
            skLineSegment(sketch, "E871", {"start": v(44.67, 31.66) * mm, "end": v(44.84, 31.67) * mm});
            skLineSegment(sketch, "E872", {"start": v(44.84, 31.67) * mm, "end": v(45.04, 31.26) * mm});
            skLineSegment(sketch, "E873", {"start": v(45.04, 31.26) * mm, "end": v(45.4, 31.2) * mm});
            skLineSegment(sketch, "E874", {"start": v(45.4, 31.2) * mm, "end": v(45.54, 31.33) * mm});
            skLineSegment(sketch, "E875", {"start": v(45.54, 31.33) * mm, "end": v(45.52, 31.5) * mm});
            skLineSegment(sketch, "E876", {"start": v(45.52, 31.5) * mm, "end": v(46.15, 31.93) * mm});
            skLineSegment(sketch, "E877", {"start": v(46.15, 31.93) * mm, "end": v(47.1, 31.58) * mm});
            skLineSegment(sketch, "E878", {"start": v(47.1, 31.58) * mm, "end": v(48.1, 28.24) * mm});
            skLineSegment(sketch, "E879", {"start": v(48.1, 28.24) * mm, "end": v(48.72, 28.25) * mm});
            skLineSegment(sketch, "E880", {"start": v(48.72, 28.25) * mm, "end": v(48.84, 28.12) * mm});
            skLineSegment(sketch, "E881", {"start": v(48.84, 28.12) * mm, "end": v(48.81, 27.54) * mm});
            skLineSegment(sketch, "E882", {"start": v(48.81, 27.54) * mm, "end": v(49.16, 27.24) * mm});
            skLineSegment(sketch, "E883", {"start": v(49.16, 27.24) * mm, "end": v(49.35, 27.23) * mm});
            skLineSegment(sketch, "E884", {"start": v(49.35, 27.23) * mm, "end": v(49.39, 27.42) * mm});
            skLineSegment(sketch, "E885", {"start": v(49.39, 27.42) * mm, "end": v(49.65, 27.45) * mm});
            skLineSegment(sketch, "E886", {"start": v(49.65, 27.45) * mm, "end": v(50.1, 26.8) * mm});
            skLineSegment(sketch, "E887", {"start": v(50.1, 26.8) * mm, "end": v(49.84, 26.09) * mm});
            skLineSegment(sketch, "E888", {"start": v(49.84, 26.09) * mm, "end": v(49.66, 26.09) * mm});
            skLineSegment(sketch, "E889", {"start": v(49.66, 26.09) * mm, "end": v(48.7, 25.05) * mm});
            skLineSegment(sketch, "E890", {"start": v(48.7, 25.05) * mm, "end": v(48.54, 25.16) * mm});
            skLineSegment(sketch, "E891", {"start": v(48.54, 25.16) * mm, "end": v(48.45, 25.33) * mm});
            skLineSegment(sketch, "E892", {"start": v(48.45, 25.33) * mm, "end": v(48.22, 25.32) * mm});
            skLineSegment(sketch, "E893", {"start": v(48.22, 25.32) * mm, "end": v(48.16, 25.15) * mm});
            skLineSegment(sketch, "E894", {"start": v(48.16, 25.15) * mm, "end": v(47.85, 24.82) * mm});
            skLineSegment(sketch, "E895", {"start": v(47.85, 24.82) * mm, "end": v(47.91, 24.64) * mm});
            skLineSegment(sketch, "E896", {"start": v(47.91, 24.64) * mm, "end": v(47.9, 24.3) * mm});
            skLineSegment(sketch, "E897", {"start": v(47.9, 24.3) * mm, "end": v(47.68, 24.33) * mm});
            skLineSegment(sketch, "E898", {"start": v(47.68, 24.33) * mm, "end": v(47.63, 24.58) * mm});
            skLineSegment(sketch, "E899", {"start": v(47.44, 24.59) * mm, "end": v(47.23, 24.93) * mm});
            skLineSegment(sketch, "E900", {"start": v(47.23, 24.93) * mm, "end": v(47.04, 24.84) * mm});
            skLineSegment(sketch, "E901", {"start": v(47.04, 24.84) * mm, "end": v(47.16, 24.64) * mm});
            skLineSegment(sketch, "E902", {"start": v(47.16, 24.64) * mm, "end": v(47.12, 24.21) * mm});
            skLineSegment(sketch, "E903", {"start": v(47.12, 24.21) * mm, "end": v(47.13, 23.88) * mm});
            skLineSegment(sketch, "E904", {"start": v(47.13, 23.88) * mm, "end": v(46.97, 23.59) * mm});
            skLineSegment(sketch, "E905", {"start": v(46.97, 23.59) * mm, "end": v(46.77, 23.57) * mm});
            skLineSegment(sketch, "E906", {"start": v(46.77, 23.57) * mm, "end": v(46.65, 23.54) * mm});
            skLineSegment(sketch, "E907", {"start": v(46.65, 23.54) * mm, "end": v(46.65, 23.23) * mm});
            skLineSegment(sketch, "E908", {"start": v(46.65, 23.23) * mm, "end": v(45.9, 22.83) * mm});
            skLineSegment(sketch, "E909", {"start": v(45.9, 22.83) * mm, "end": v(45.67, 22.94) * mm});
            skLineSegment(sketch, "E910", {"start": v(45.67, 22.94) * mm, "end": v(45.37, 22.58) * mm});
            skLineSegment(sketch, "E911", {"start": v(45.37, 22.58) * mm, "end": v(45.45, 22.2) * mm});
            skLineSegment(sketch, "E912", {"start": v(45.45, 22.2) * mm, "end": v(45.33, 22.11) * mm});
            skLineSegment(sketch, "E913", {"start": v(45.33, 22.11) * mm, "end": v(45.14, 20.76) * mm});
            skLineSegment(sketch, "E914", {"start": v(47.44, 24.59) * mm, "end": v(47.63, 24.58) * mm});
            skLineSegment(sketch, "E915", {"start": v(31.3, 9.34) * mm, "end": v(31.54, 8.06) * mm});
            skLineSegment(sketch, "E916", {"start": v(31.54, 8.06) * mm, "end": v(32.06, 8.77) * mm});
            skLineSegment(sketch, "E917", {"start": v(32.06, 8.77) * mm, "end": v(32.4, 8.7) * mm});
            skLineSegment(sketch, "E918", {"start": v(32.4, 8.7) * mm, "end": v(32.73, 9.17) * mm});
            skLineSegment(sketch, "E919", {"start": v(32.73, 9.17) * mm, "end": v(32.96, 9.09) * mm});
            skLineSegment(sketch, "E920", {"start": v(32.96, 9.09) * mm, "end": v(33.16, 9.15) * mm});
            skLineSegment(sketch, "E921", {"start": v(23.37, 13) * mm, "end": v(23.7, 13.86) * mm});
            skLineSegment(sketch, "E922", {"start": v(23.7, 13.86) * mm, "end": v(23.79, 14.47) * mm});
            skLineSegment(sketch, "E923", {"start": v(23.79, 14.47) * mm, "end": v(24.1, 14.77) * mm});
            skLineSegment(sketch, "E924", {"start": v(24.1, 14.77) * mm, "end": v(24.22, 15.18) * mm});
            skLineSegment(sketch, "E925", {"start": v(24.22, 15.18) * mm, "end": v(24.52, 15.6) * mm});
            skLineSegment(sketch, "E926", {"start": v(24.52, 15.6) * mm, "end": v(24.68, 16.23) * mm});
            skLineSegment(sketch, "E927", {"start": v(24.68, 16.23) * mm, "end": v(24.58, 16.82) * mm});
            skLineSegment(sketch, "E928", {"start": v(24.58, 16.82) * mm, "end": v(24.28, 17.75) * mm});
            skLineSegment(sketch, "E929", {"start": v(24.28, 17.75) * mm, "end": v(24.12, 18.4) * mm});
            skLineSegment(sketch, "E930", {"start": v(24.12, 18.4) * mm, "end": v(23.6, 18.94) * mm});
            skLineSegment(sketch, "E931", {"start": v(23.6, 18.94) * mm, "end": v(23.02, 18.6) * mm});
            skLineSegment(sketch, "E932", {"start": v(23.02, 18.6) * mm, "end": v(22.8, 17.95) * mm});
            skLineSegment(sketch, "E933", {"start": v(22.8, 17.95) * mm, "end": v(22.42, 17.57) * mm});
            skLineSegment(sketch, "E934", {"start": v(22.42, 17.57) * mm, "end": v(21.89, 17.77) * mm});
            skLineSegment(sketch, "E935", {"start": v(21.89, 17.77) * mm, "end": v(21.99, 18.42) * mm});
            skLineSegment(sketch, "E936", {"start": v(21.99, 18.42) * mm, "end": v(22.4, 18.54) * mm});
            skLineSegment(sketch, "E937", {"start": v(22.4, 18.54) * mm, "end": v(22.48, 19.21) * mm});
            skLineSegment(sketch, "E938", {"start": v(22.48, 19.21) * mm, "end": v(22.78, 19.35) * mm});
            skLineSegment(sketch, "E939", {"start": v(22.78, 19.35) * mm, "end": v(22.74, 20.46) * mm});
            skLineSegment(sketch, "E940", {"start": v(22.74, 20.46) * mm, "end": v(22.34, 20.83) * mm});
            skLineSegment(sketch, "E941", {"start": v(22.34, 20.83) * mm, "end": v(22.3, 21.01) * mm});
            skLineSegment(sketch, "E942", {"start": v(22.3, 21.01) * mm, "end": v(22.4, 21.19) * mm});
            skLineSegment(sketch, "E943", {"start": v(22.4, 21.19) * mm, "end": v(22.58, 21.15) * mm});
            skLineSegment(sketch, "E944", {"start": v(22.58, 21.15) * mm, "end": v(22.62, 21.29) * mm});
            skLineSegment(sketch, "E945", {"start": v(22.62, 21.29) * mm, "end": v(22.2, 21.84) * mm});
            skLineSegment(sketch, "E946", {"start": v(22.2, 21.84) * mm, "end": v(21.75, 21.88) * mm});
            skLineSegment(sketch, "E947", {"start": v(21.75, 21.88) * mm, "end": v(20.88, 22.35) * mm});
            skLineSegment(sketch, "E948", {"start": v(20.88, 22.35) * mm, "end": v(20.53, 22.4) * mm});
            skLineSegment(sketch, "E949", {"start": v(20.53, 22.4) * mm, "end": v(20.37, 22.3) * mm});
            skLineSegment(sketch, "E950", {"start": v(20.37, 22.3) * mm, "end": v(20.01, 22.6) * mm});
            skLineSegment(sketch, "E951", {"start": v(20.01, 22.6) * mm, "end": v(19.32, 22.22) * mm});
            skLineSegment(sketch, "E952", {"start": v(19.32, 22.22) * mm, "end": v(19.36, 21.8) * mm});
            skLineSegment(sketch, "E953", {"start": v(19.36, 21.8) * mm, "end": v(19.62, 21.74) * mm});
            skLineSegment(sketch, "E954", {"start": v(19.62, 21.74) * mm, "end": v(19.77, 21.56) * mm});
            skLineSegment(sketch, "E955", {"start": v(19.77, 21.56) * mm, "end": v(19.52, 21.45) * mm});
            skLineSegment(sketch, "E956", {"start": v(19.52, 21.45) * mm, "end": v(19.3, 21.49) * mm});
            skLineSegment(sketch, "E957", {"start": v(19.3, 21.49) * mm, "end": v(19.06, 21.2) * mm});
            skLineSegment(sketch, "E958", {"start": v(19.06, 21.2) * mm, "end": v(19.12, 20.28) * mm});
            skLineSegment(sketch, "E959", {"start": v(19.12, 20.28) * mm, "end": v(18.65, 19.96) * mm});
            skLineSegment(sketch, "E960", {"start": v(18.65, 19.96) * mm, "end": v(18.55, 20.46) * mm});
            skLineSegment(sketch, "E961", {"start": v(18.55, 20.46) * mm, "end": v(18.85, 20.97) * mm});
            skLineSegment(sketch, "E962", {"start": v(18.85, 20.97) * mm, "end": v(18.73, 21.1) * mm});
            skLineSegment(sketch, "E963", {"start": v(18.73, 21.1) * mm, "end": v(18.51, 21.01) * mm});
            skLineSegment(sketch, "E964", {"start": v(18.51, 21.01) * mm, "end": v(18.4, 20.62) * mm});
            skLineSegment(sketch, "E965", {"start": v(18.4, 20.62) * mm, "end": v(17.92, 20.24) * mm});
            skLineSegment(sketch, "E966", {"start": v(17.92, 20.24) * mm, "end": v(17.94, 20.08) * mm});
            skLineSegment(sketch, "E967", {"start": v(17.94, 20.08) * mm, "end": v(17.92, 19.75) * mm});
            skLineSegment(sketch, "E968", {"start": v(17.92, 19.75) * mm, "end": v(17.64, 19.73) * mm});
            skLineSegment(sketch, "E969", {"start": v(17.64, 19.73) * mm, "end": v(17.74, 19.27) * mm});
            skLineSegment(sketch, "E970", {"start": v(17.74, 19.27) * mm, "end": v(17.44, 18.26) * mm});
            skLineSegment(sketch, "E971", {"start": v(17.44, 18.26) * mm, "end": v(17.56, 17.5) * mm});
            skLineSegment(sketch, "E972", {"start": v(17.56, 17.5) * mm, "end": v(17.32, 16.92) * mm});
            skLineSegment(sketch, "E973", {"start": v(17.32, 16.92) * mm, "end": v(18.27, 15.02) * mm});
            skLineSegment(sketch, "E974", {"start": v(18.27, 15.02) * mm, "end": v(17.9, 13.34) * mm});
            skLineSegment(sketch, "E975", {"start": v(17.9, 13.34) * mm, "end": v(17.74, 12.87) * mm});
            skLineSegment(sketch, "E976", {"start": v(17.74, 12.87) * mm, "end": v(17.33, 12.38) * mm});
            skLineSegment(sketch, "E977", {"start": v(33.16, 9.15) * mm, "end": v(33.77, 9.59) * mm});
            skLineSegment(sketch, "E978", {"start": v(33.77, 9.59) * mm, "end": v(34.7, 9) * mm});
            skLineSegment(sketch, "E979", {"start": v(34.7, 9) * mm, "end": v(34.64, 8.42) * mm});
            skLineSegment(sketch, "E980", {"start": v(34.64, 8.42) * mm, "end": v(33.58, 8.9) * mm});
            skLineSegment(sketch, "E981", {"start": v(33.58, 8.9) * mm, "end": v(33.48, 8.25) * mm});
            skLineSegment(sketch, "E982", {"start": v(33.48, 8.25) * mm, "end": v(33.14, 7.63) * mm});
            skLineSegment(sketch, "E983", {"start": v(33.14, 7.63) * mm, "end": v(32.84, 7.4) * mm});
            skLineSegment(sketch, "E984", {"start": v(32.84, 7.4) * mm, "end": v(32.8, 7.15) * mm});
            skLineSegment(sketch, "E985", {"start": v(32.8, 7.15) * mm, "end": v(32.4, 7.06) * mm});
            skLineSegment(sketch, "E986", {"start": v(32.4, 7.06) * mm, "end": v(32.3, 6.18) * mm});
            skLineSegment(sketch, "E987", {"start": v(32.3, 6.18) * mm, "end": v(31.66, 6.49) * mm});
            skLineSegment(sketch, "E988", {"start": v(31.66, 6.49) * mm, "end": v(31.43, 6.48) * mm});
            skLineSegment(sketch, "E989", {"start": v(27.45, 3.14) * mm, "end": v(28.02, 2.6) * mm});
            skLineSegment(sketch, "E990", {"start": v(28.02, 2.6) * mm, "end": v(28.46, 2.5) * mm});
            skLineSegment(sketch, "E991", {"start": v(28.46, 2.5) * mm, "end": v(28.74, 2.87) * mm});
            skLineSegment(sketch, "E992", {"start": v(28.74, 2.87) * mm, "end": v(28.86, 2.68) * mm});
            skLineSegment(sketch, "E993", {"start": v(28.86, 2.68) * mm, "end": v(29.48, 2.77) * mm});
            skLineSegment(sketch, "E994", {"start": v(29.48, 2.77) * mm, "end": v(29.62, 3.3) * mm});
            skLineSegment(sketch, "E995", {"start": v(29.62, 3.3) * mm, "end": v(29.95, 3.24) * mm});
            skLineSegment(sketch, "E996", {"start": v(29.95, 3.24) * mm, "end": v(30.3, 3.46) * mm});
            skLineSegment(sketch, "E997", {"start": v(30.3, 3.46) * mm, "end": v(30.52, 3.43) * mm});
            skLineSegment(sketch, "E998", {"start": v(30.52, 3.43) * mm, "end": v(30.73, 3.9) * mm});
            skLineSegment(sketch, "E999", {"start": v(30.73, 3.9) * mm, "end": v(30.58, 4.07) * mm});
            skLineSegment(sketch, "E1000", {"start": v(30.58, 4.07) * mm, "end": v(31.44, 5.96) * mm});
            skLineSegment(sketch, "E1001", {"start": v(31.44, 5.96) * mm, "end": v(31.43, 6.48) * mm});
            skLineSegment(sketch, "E1002", {"start": v(38.55, 10.38) * mm, "end": v(38.43, 10.44) * mm});
            skLineSegment(sketch, "E1003", {"start": v(38.43, 10.44) * mm, "end": v(38.37, 10.27) * mm});
            skLineSegment(sketch, "E1004", {"start": v(38.37, 10.27) * mm, "end": v(38.66, 9.88) * mm});
            skLineSegment(sketch, "E1005", {"start": v(38.66, 9.88) * mm, "end": v(38.87, 9.81) * mm});
            skLineSegment(sketch, "E1006", {"start": v(38.87, 9.81) * mm, "end": v(39.3, 8.87) * mm});
            skLineSegment(sketch, "E1007", {"start": v(39.3, 8.87) * mm, "end": v(39.69, 8.59) * mm});
            skLineSegment(sketch, "E1008", {"start": v(39.69, 8.59) * mm, "end": v(39.82, 8.64) * mm});
            skLineSegment(sketch, "E1009", {"start": v(39.82, 8.64) * mm, "end": v(40.03, 7.9) * mm});
            skLineSegment(sketch, "E1010", {"start": v(40.03, 7.9) * mm, "end": v(40.04, 7.2) * mm});
            skLineSegment(sketch, "E1011", {"start": v(40.04, 7.2) * mm, "end": v(39.8, 6.36) * mm});
            skLineSegment(sketch, "E1012", {"start": v(39.8, 6.36) * mm, "end": v(39.48, 5.92) * mm});
            skLineSegment(sketch, "E1013", {"start": v(39.48, 5.92) * mm, "end": v(39.46, 5.04) * mm});
            skLineSegment(sketch, "E1014", {"start": v(39.46, 5.04) * mm, "end": v(39.18, 4.27) * mm});
            skLineSegment(sketch, "E1015", {"start": v(39.18, 4.27) * mm, "end": v(39.01, 4.27) * mm});
            skLineSegment(sketch, "E1016", {"start": v(39.01, 4.27) * mm, "end": v(38.88, 4.53) * mm});
            skLineSegment(sketch, "E1017", {"start": v(38.88, 4.53) * mm, "end": v(38.86, 5.39) * mm});
            skLineSegment(sketch, "E1018", {"start": v(38.86, 5.39) * mm, "end": v(39.15, 5.9) * mm});
            skLineSegment(sketch, "E1019", {"start": v(39.15, 5.9) * mm, "end": v(39.17, 6.42) * mm});
            skLineSegment(sketch, "E1020", {"start": v(39.17, 6.42) * mm, "end": v(38.97, 6.4) * mm});
            skLineSegment(sketch, "E1021", {"start": v(38.97, 6.4) * mm, "end": v(38.6, 7.05) * mm});
            skLineSegment(sketch, "E1022", {"start": v(38.6, 7.05) * mm, "end": v(38.51, 6.94) * mm});
            skLineSegment(sketch, "E1023", {"start": v(38.51, 6.94) * mm, "end": v(37.92, 6.95) * mm});
            skLineSegment(sketch, "E1024", {"start": v(37.92, 6.95) * mm, "end": v(37.73, 7.31) * mm});
            skLineSegment(sketch, "E1025", {"start": v(37.73, 7.31) * mm, "end": v(37.69, 7.7) * mm});
            skLineSegment(sketch, "E1026", {"start": v(37.69, 7.7) * mm, "end": v(37.92, 7.83) * mm});
            skLineSegment(sketch, "E1027", {"start": v(37.92, 7.83) * mm, "end": v(37.72, 8.11) * mm});
            skLineSegment(sketch, "E1028", {"start": v(37.72, 8.11) * mm, "end": v(37.58, 7.87) * mm});
            skLineSegment(sketch, "E1029", {"start": v(37.58, 7.87) * mm, "end": v(37.5, 8.2) * mm});
            skLineSegment(sketch, "E1030", {"start": v(37.5, 8.2) * mm, "end": v(37.77, 8.4) * mm});
            skLineSegment(sketch, "E1031", {"start": v(37.77, 8.4) * mm, "end": v(37.73, 8.95) * mm});
            skLineSegment(sketch, "E1032", {"start": v(37.73, 8.95) * mm, "end": v(37.5, 8.94) * mm});
            skLineSegment(sketch, "E1033", {"start": v(37.5, 8.94) * mm, "end": v(37.53, 9.33) * mm});
            skLineSegment(sketch, "E1034", {"start": v(37.53, 9.33) * mm, "end": v(37.84, 9.65) * mm});
            skLineSegment(sketch, "E1035", {"start": v(37.84, 9.65) * mm, "end": v(37.72, 9.82) * mm});
            skLineSegment(sketch, "E1036", {"start": v(37.72, 9.82) * mm, "end": v(37.32, 9.48) * mm});
            skLineSegment(sketch, "E1037", {"start": v(37.32, 9.48) * mm, "end": v(37.07, 8.98) * mm});
            skLineSegment(sketch, "E1038", {"start": v(37.07, 8.98) * mm, "end": v(37.3, 8.63) * mm});
            skLineSegment(sketch, "E1039", {"start": v(37.3, 8.63) * mm, "end": v(37.11, 8.07) * mm});
            skLineSegment(sketch, "E1040", {"start": v(37.11, 8.07) * mm, "end": v(37.37, 7.41) * mm});
            skLineSegment(sketch, "E1041", {"start": v(37.37, 7.41) * mm, "end": v(37.59, 7.22) * mm});
            skLineSegment(sketch, "E1042", {"start": v(37.59, 7.22) * mm, "end": v(37.56, 7.04) * mm});
            skLineSegment(sketch, "E1043", {"start": v(37.56, 7.04) * mm, "end": v(37.7, 6.59) * mm});
            skLineSegment(sketch, "E1044", {"start": v(37.7, 6.59) * mm, "end": v(37.1, 6.64) * mm});
            skLineSegment(sketch, "E1045", {"start": v(37.1, 6.64) * mm, "end": v(36.64, 6.67) * mm});
            skLineSegment(sketch, "E1046", {"start": v(36.64, 6.67) * mm, "end": v(36.04, 6.78) * mm});
            skLineSegment(sketch, "E1047", {"start": v(36.04, 6.78) * mm, "end": v(35.95, 7.22) * mm});
            skLineSegment(sketch, "E1048", {"start": v(35.95, 7.22) * mm, "end": v(36.16, 7.48) * mm});
            skLineSegment(sketch, "E1049", {"start": v(36.16, 7.48) * mm, "end": v(36.2, 7.83) * mm});
            skLineSegment(sketch, "E1050", {"start": v(36.2, 7.83) * mm, "end": v(35.86, 8.25) * mm});
            skLineSegment(sketch, "E1051", {"start": v(35.86, 8.25) * mm, "end": v(35.19, 8.42) * mm});
            skLineSegment(sketch, "E1052", {"start": v(35.19, 8.42) * mm, "end": v(35.21, 8.74) * mm});
            skLineSegment(sketch, "E1053", {"start": v(35.21, 8.74) * mm, "end": v(34.7, 9) * mm});
            skLineSegment(sketch, "E1054", {"start": v(36.64, 6.67) * mm, "end": v(36.82, 6.48) * mm});
            skLineSegment(sketch, "E1055", {"start": v(36.82, 6.48) * mm, "end": v(37.46, 6.43) * mm});
            skLineSegment(sketch, "E1056", {"start": v(37.46, 6.43) * mm, "end": v(37.66, 6.16) * mm});
            skLineSegment(sketch, "E1057", {"start": v(37.66, 6.16) * mm, "end": v(38.01, 6.17) * mm});
            skLineSegment(sketch, "E1058", {"start": v(38.01, 6.17) * mm, "end": v(38.16, 6) * mm});
            skLineSegment(sketch, "E1059", {"start": v(38.16, 6) * mm, "end": v(38.13, 5.48) * mm});
            skLineSegment(sketch, "E1060", {"start": v(38.13, 5.48) * mm, "end": v(38.23, 5.42) * mm});
            skLineSegment(sketch, "E1061", {"start": v(38.23, 5.42) * mm, "end": v(38.23, 5.14) * mm});
            skLineSegment(sketch, "E1062", {"start": v(38.23, 5.14) * mm, "end": v(38.42, 4.88) * mm});
            skLineSegment(sketch, "E1063", {"start": v(38.42, 4.88) * mm, "end": v(38.41, 4.7) * mm});
            skLineSegment(sketch, "E1064", {"start": v(38.41, 4.7) * mm, "end": v(38, 4.83) * mm});
            skLineSegment(sketch, "E1065", {"start": v(38, 4.83) * mm, "end": v(38, 4.73) * mm});
            skLineSegment(sketch, "E1066", {"start": v(38, 4.73) * mm, "end": v(38.22, 4.57) * mm});
            skLineSegment(sketch, "E1067", {"start": v(38.22, 4.57) * mm, "end": v(38.22, 4.44) * mm});
            skLineSegment(sketch, "E1068", {"start": v(38.22, 4.44) * mm, "end": v(38.53, 4.17) * mm});
            skLineSegment(sketch, "E1069", {"start": v(38.53, 4.17) * mm, "end": v(38.6, 3.82) * mm});
            skLineSegment(sketch, "E1070", {"start": v(38.6, 3.82) * mm, "end": v(38.3, 3.71) * mm});
            skLineSegment(sketch, "E1071", {"start": v(38.3, 3.71) * mm, "end": v(38.3, 3.6) * mm});
            skLineSegment(sketch, "E1072", {"start": v(38.3, 3.6) * mm, "end": v(39.12, 3.78) * mm});
            skLineSegment(sketch, "E1073", {"start": v(39.12, 3.78) * mm, "end": v(39.47, 2.95) * mm});
            skLineSegment(sketch, "E1074", {"start": v(39.47, 2.95) * mm, "end": v(40.52, 1.25) * mm});
            skLineSegment(sketch, "E1075", {"start": v(40.52, 1.25) * mm, "end": v(40.12, 1.25) * mm});
            skLineSegment(sketch, "E1076", {"start": v(26.15, -3.3) * mm, "end": v(27.83, -2.53) * mm});
            skLineSegment(sketch, "E1077", {"start": v(27.83, -2.53) * mm, "end": v(30.43, -2.37) * mm});
            skLineSegment(sketch, "E1078", {"start": v(30.43, -2.37) * mm, "end": v(30.72, -2.7) * mm});
            skLineSegment(sketch, "E1079", {"start": v(30.72, -2.7) * mm, "end": v(30.8, -2.96) * mm});
            skLineSegment(sketch, "E1080", {"start": v(30.8, -2.96) * mm, "end": v(32.94, -2.77) * mm});
            skLineSegment(sketch, "E1081", {"start": v(32.94, -2.77) * mm, "end": v(35.51, -4.54) * mm});
            skLineSegment(sketch, "E1082", {"start": v(35.51, -4.54) * mm, "end": v(36.07, -4.38) * mm});
            skLineSegment(sketch, "E1083", {"start": v(36.07, -4.38) * mm, "end": v(36.8, -4.32) * mm});
            skLineSegment(sketch, "E1084", {"start": v(36.8, -4.32) * mm, "end": v(36.98, -3.28) * mm});
            skLineSegment(sketch, "E1085", {"start": v(36.98, -3.28) * mm, "end": v(38.16, -2.16) * mm});
            skLineSegment(sketch, "E1086", {"start": v(38.16, -2.16) * mm, "end": v(39, -1.8) * mm});
            skLineSegment(sketch, "E1087", {"start": v(39, -1.8) * mm, "end": v(39.29, -1.89) * mm});
            skLineSegment(sketch, "E1088", {"start": v(39.29, -1.89) * mm, "end": v(39.8, -1.06) * mm});
            skLineSegment(sketch, "E1089", {"start": v(39.8, -1.06) * mm, "end": v(39.45, -1.27) * mm});
            skLineSegment(sketch, "E1090", {"start": v(39.45, -1.27) * mm, "end": v(39.31, -1.09) * mm});
            skLineSegment(sketch, "E1091", {"start": v(39.31, -1.09) * mm, "end": v(38.86, -1.11) * mm});
            skLineSegment(sketch, "E1092", {"start": v(38.86, -1.11) * mm, "end": v(39.12, -0.4) * mm});
            skLineSegment(sketch, "E1093", {"start": v(39.12, -0.4) * mm, "end": v(38.83, -0.28) * mm});
            skLineSegment(sketch, "E1094", {"start": v(38.83, -0.28) * mm, "end": v(38.7, 0.01) * mm});
            skLineSegment(sketch, "E1095", {"start": v(38.7, 0.01) * mm, "end": v(39.26, -0.26) * mm});
            skLineSegment(sketch, "E1096", {"start": v(39.26, -0.26) * mm, "end": v(39.8, -0.1) * mm});
            skLineSegment(sketch, "E1097", {"start": v(39.8, -0.1) * mm, "end": v(40, 0.57) * mm});
            skLineSegment(sketch, "E1098", {"start": v(40, 0.57) * mm, "end": v(40.28, 0.7) * mm});
            skLineSegment(sketch, "E1099", {"start": v(40.28, 0.7) * mm, "end": v(40.12, 1.25) * mm});
            skLineSegment(sketch, "E1100", {"start": v(26.15, -3.3) * mm, "end": v(26.26, -3.54) * mm});
            skLineSegment(sketch, "E1101", {"start": v(26.26, -3.54) * mm, "end": v(25.94, -3.73) * mm});
            skLineSegment(sketch, "E1102", {"start": v(25.94, -3.73) * mm, "end": v(25.85, -4.13) * mm});
            skLineSegment(sketch, "E1103", {"start": v(25.85, -4.13) * mm, "end": v(26.52, -4.53) * mm});
            skLineSegment(sketch, "E1104", {"start": v(26.52, -4.53) * mm, "end": v(26.82, -4.47) * mm});
            skLineSegment(sketch, "E1105", {"start": v(26.82, -4.47) * mm, "end": v(27.6, -5.68) * mm});
            skLineSegment(sketch, "E1106", {"start": v(27.6, -5.68) * mm, "end": v(28.36, -6.12) * mm});
            skLineSegment(sketch, "E1107", {"start": v(28.36, -6.12) * mm, "end": v(28.5, -6.42) * mm});
            skLineSegment(sketch, "E1108", {"start": v(28.5, -6.42) * mm, "end": v(29.1, -6.74) * mm});
            skLineSegment(sketch, "E1109", {"start": v(29.1, -6.74) * mm, "end": v(29.57, -7.32) * mm});
            skLineSegment(sketch, "E1110", {"start": v(29.57, -7.32) * mm, "end": v(30.02, -7.55) * mm});
            skLineSegment(sketch, "E1111", {"start": v(30.02, -7.55) * mm, "end": v(30.5, -8.75) * mm});
            skLineSegment(sketch, "E1112", {"start": v(30.5, -8.75) * mm, "end": v(30.72, -8.75) * mm});
            skLineSegment(sketch, "E1113", {"start": v(30.72, -8.75) * mm, "end": v(31.08, -9.2) * mm});
            skLineSegment(sketch, "E1114", {"start": v(31.08, -9.2) * mm, "end": v(31.19, -9.65) * mm});
            skLineSegment(sketch, "E1115", {"start": v(31.19, -9.65) * mm, "end": v(31.8, -9.9) * mm});
            skLineSegment(sketch, "E1116", {"start": v(31.8, -9.9) * mm, "end": v(31.73, -9.68) * mm});
            skLineSegment(sketch, "E1117", {"start": v(31.73, -9.68) * mm, "end": v(32.5, -9) * mm});
            skLineSegment(sketch, "E1118", {"start": v(32.5, -9) * mm, "end": v(32.34, -8.64) * mm});
            skLineSegment(sketch, "E1119", {"start": v(32.34, -8.64) * mm, "end": v(32.75, -8.62) * mm});
            skLineSegment(sketch, "E1120", {"start": v(32.75, -8.62) * mm, "end": v(34.08, -7.1) * mm});
            skLineSegment(sketch, "E1121", {"start": v(34.08, -7.1) * mm, "end": v(34.28, -7.02) * mm});
            skLineSegment(sketch, "E1122", {"start": v(34.28, -7.02) * mm, "end": v(34.7, -6.53) * mm});
            skLineSegment(sketch, "E1123", {"start": v(34.7, -6.53) * mm, "end": v(34.73, -5.86) * mm});
            skLineSegment(sketch, "E1124", {"start": v(34.73, -5.86) * mm, "end": v(35.23, -4.94) * mm});
            skLineSegment(sketch, "E1125", {"start": v(35.23, -4.94) * mm, "end": v(35.51, -4.54) * mm});
            skLineSegment(sketch, "E1126", {"start": v(31.8, -9.9) * mm, "end": v(31.44, -10.7) * mm});
            skLineSegment(sketch, "E1127", {"start": v(31.44, -10.7) * mm, "end": v(31.47, -10.88) * mm});
            skLineSegment(sketch, "E1128", {"start": v(31.47, -10.88) * mm, "end": v(31.32, -11.38) * mm});
            skLineSegment(sketch, "E1129", {"start": v(31.32, -11.38) * mm, "end": v(30.99, -12.4) * mm});
            skLineSegment(sketch, "E1130", {"start": v(30.99, -12.4) * mm, "end": v(31.05, -13.22) * mm});
            skLineSegment(sketch, "E1131", {"start": v(31.05, -13.22) * mm, "end": v(29.97, -13.13) * mm});
            skLineSegment(sketch, "E1132", {"start": v(29.97, -13.13) * mm, "end": v(29.8, -13.32) * mm});
            skLineSegment(sketch, "E1133", {"start": v(29.8, -13.32) * mm, "end": v(29.88, -13.72) * mm});
            skLineSegment(sketch, "E1134", {"start": v(29.88, -13.72) * mm, "end": v(29.92, -14.22) * mm});
            skLineSegment(sketch, "E1135", {"start": v(29.92, -14.22) * mm, "end": v(29.61, -14.2) * mm});
            skLineSegment(sketch, "E1136", {"start": v(29.61, -14.2) * mm, "end": v(29.57, -13.82) * mm});
            skLineSegment(sketch, "E1137", {"start": v(28.8, -17.36) * mm, "end": v(29.37, -18.15) * mm});
            skLineSegment(sketch, "E1138", {"start": v(29.37, -18.15) * mm, "end": v(29.34, -19.33) * mm});
            skLineSegment(sketch, "E1139", {"start": v(29.34, -19.33) * mm, "end": v(29.11, -19.64) * mm});
            skLineSegment(sketch, "E1140", {"start": v(29.11, -19.64) * mm, "end": v(29.54, -20.91) * mm});
            skLineSegment(sketch, "E1141", {"start": v(29.54, -20.91) * mm, "end": v(29.73, -20.58) * mm});
            skLineSegment(sketch, "E1142", {"start": v(29.73, -20.58) * mm, "end": v(29.4, -20.3) * mm});
            skLineSegment(sketch, "E1143", {"start": v(29.4, -20.3) * mm, "end": v(30.19, -20.32) * mm});
            skLineSegment(sketch, "E1144", {"start": v(30.19, -20.32) * mm, "end": v(29.56, -21.28) * mm});
            skLineSegment(sketch, "E1145", {"start": v(29.56, -21.28) * mm, "end": v(30.21, -22.1) * mm});
            skLineSegment(sketch, "E1146", {"start": v(30.21, -22.1) * mm, "end": v(30.67, -22.72) * mm});
            skLineSegment(sketch, "E1147", {"start": v(30.67, -22.72) * mm, "end": v(31.03, -23.65) * mm});
            skLineSegment(sketch, "E1148", {"start": v(31.03, -23.65) * mm, "end": v(31.26, -23.8) * mm});
            skLineSegment(sketch, "E1149", {"start": v(31.26, -23.8) * mm, "end": v(31.48, -23.6) * mm});
            skLineSegment(sketch, "E1150", {"start": v(31.48, -23.6) * mm, "end": v(31.88, -23.9) * mm});
            skLineSegment(sketch, "E1151", {"start": v(31.88, -23.9) * mm, "end": v(31.96, -24.27) * mm});
            skLineSegment(sketch, "E1152", {"start": v(31.96, -24.27) * mm, "end": v(32.3, -24.8) * mm});
            skLineSegment(sketch, "E1153", {"start": v(32.3, -24.8) * mm, "end": v(32.5, -24.78) * mm});
            skLineSegment(sketch, "E1154", {"start": v(32.5, -24.78) * mm, "end": v(32.87, -24.84) * mm});
            skLineSegment(sketch, "E1155", {"start": v(32.87, -24.84) * mm, "end": v(33.29, -25.18) * mm});
            skLineSegment(sketch, "E1156", {"start": v(33.29, -25.18) * mm, "end": v(33.63, -25.63) * mm});
            skLineSegment(sketch, "E1157", {"start": v(33.63, -25.63) * mm, "end": v(33.8, -26.45) * mm});
            skLineSegment(sketch, "E1158", {"start": v(33.8, -26.45) * mm, "end": v(34, -26.61) * mm});
            skLineSegment(sketch, "E1159", {"start": v(34, -26.61) * mm, "end": v(34.3, -26.5) * mm});
            skLineSegment(sketch, "E1160", {"start": v(34.3, -26.5) * mm, "end": v(34.48, -26.16) * mm});
            skLineSegment(sketch, "E1161", {"start": v(34.48, -26.16) * mm, "end": v(34.7, -26.22) * mm});
            skLineSegment(sketch, "E1162", {"start": v(34.7, -26.22) * mm, "end": v(35.07, -26.16) * mm});
            skLineSegment(sketch, "E1163", {"start": v(35.07, -26.16) * mm, "end": v(35.55, -25.82) * mm});
            skLineSegment(sketch, "E1164", {"start": v(35.55, -25.82) * mm, "end": v(35.46, -25.4) * mm});
            skLineSegment(sketch, "E1165", {"start": v(35.46, -25.4) * mm, "end": v(35.46, -25.15) * mm});
            skLineSegment(sketch, "E1166", {"start": v(35.46, -25.15) * mm, "end": v(35.38, -24.78) * mm});
            skLineSegment(sketch, "E1167", {"start": v(35.38, -24.78) * mm, "end": v(35.8, -24.47) * mm});
            skLineSegment(sketch, "E1168", {"start": v(35.8, -24.47) * mm, "end": v(35.8, -24.02) * mm});
            skLineSegment(sketch, "E1169", {"start": v(35.8, -24.02) * mm, "end": v(35.66, -22.07) * mm});
            skLineSegment(sketch, "E1170", {"start": v(35.66, -22.07) * mm, "end": v(34.45, -19.81) * mm});
            skLineSegment(sketch, "E1171", {"start": v(34.45, -19.81) * mm, "end": v(33.91, -19.45) * mm});
            skLineSegment(sketch, "E1172", {"start": v(33.91, -19.45) * mm, "end": v(33.69, -18.66) * mm});
            skLineSegment(sketch, "E1173", {"start": v(33.69, -18.66) * mm, "end": v(33.85, -18.37) * mm});
            skLineSegment(sketch, "E1174", {"start": v(33.85, -18.37) * mm, "end": v(33.66, -17.9) * mm});
            skLineSegment(sketch, "E1175", {"start": v(33.66, -17.9) * mm, "end": v(32.92, -17.19) * mm});
            skLineSegment(sketch, "E1176", {"start": v(32.92, -17.19) * mm, "end": v(32.02, -15.8) * mm});
            skLineSegment(sketch, "E1177", {"start": v(32.02, -15.8) * mm, "end": v(31.31, -14.17) * mm});
            skLineSegment(sketch, "E1178", {"start": v(31.31, -14.17) * mm, "end": v(31.05, -13.22) * mm});
            skLineSegment(sketch, "E1179", {"start": v(-34.84, -14.17) * mm, "end": v(-35.81, -13.68) * mm});
            skLineSegment(sketch, "E1180", {"start": v(-35.81, -13.68) * mm, "end": v(-36.16, -13.85) * mm});
            skLineSegment(sketch, "E1181", {"start": v(-36.16, -13.85) * mm, "end": v(-36.86, -13.55) * mm});
            skLineSegment(sketch, "E1182", {"start": v(-36.86, -13.55) * mm, "end": v(-36.95, -13.85) * mm});
            skLineSegment(sketch, "E1183", {"start": v(-36.95, -13.85) * mm, "end": v(-37.65, -13.2) * mm});
            skLineSegment(sketch, "E1184", {"start": v(-37.65, -13.2) * mm, "end": v(-38.48, -13.15) * mm});
            skLineSegment(sketch, "E1185", {"start": v(-38.48, -13.15) * mm, "end": v(-38.73, -13.03) * mm});
            skLineSegment(sketch, "E1186", {"start": v(-38.73, -13.03) * mm, "end": v(-38.74, -12.54) * mm});
            skLineSegment(sketch, "E1187", {"start": v(-38.74, -12.54) * mm, "end": v(-39.15, -12.5) * mm});
            skLineSegment(sketch, "E1188", {"start": v(-39.15, -12.5) * mm, "end": v(-39.3, -12.75) * mm});
            skLineSegment(sketch, "E1189", {"start": v(-39.3, -12.75) * mm, "end": v(-39.35, -12.45) * mm});
            skLineSegment(sketch, "E1190", {"start": v(-39.35, -12.45) * mm, "end": v(-40.07, -11.94) * mm});
            skLineSegment(sketch, "E1191", {"start": v(-40.07, -11.94) * mm, "end": v(-40.39, -12.28) * mm});
            skLineSegment(sketch, "E1192", {"start": v(-40.39, -12.28) * mm, "end": v(-40.86, -12.32) * mm});
            skLineSegment(sketch, "E1193", {"start": v(-40.86, -12.32) * mm, "end": v(-41.06, -12.22) * mm});
            skLineSegment(sketch, "E1194", {"start": v(-41.06, -12.22) * mm, "end": v(-41.84, -12.57) * mm});
            skLineSegment(sketch, "E1195", {"start": v(-41.84, -12.57) * mm, "end": v(-42.1, -12.37) * mm});
            skLineSegment(sketch, "E1196", {"start": v(-42.1, -12.37) * mm, "end": v(-42.4, -12.7) * mm});
            skLineSegment(sketch, "E1197", {"start": v(-42.4, -12.7) * mm, "end": v(-42.5, -13.03) * mm});
            skLineSegment(sketch, "E1198", {"start": v(-42.5, -13.03) * mm, "end": v(-42.95, -13.4) * mm});
            skLineSegment(sketch, "E1199", {"start": v(-42.95, -13.4) * mm, "end": v(-43.4, -13.4) * mm});
            skLineSegment(sketch, "E1200", {"start": v(-43.4, -13.4) * mm, "end": v(-43.48, -13.4) * mm});
            skLineSegment(sketch, "E1201", {"start": v(-43.48, -13.4) * mm, "end": v(-43.94, -13.3) * mm});
            skLineSegment(sketch, "E1202", {"start": v(-43.94, -13.3) * mm, "end": v(-44.27, -13.56) * mm});
            skLineSegment(sketch, "E1203", {"start": v(-44.27, -13.56) * mm, "end": v(-43.68, -14.58) * mm});
            skLineSegment(sketch, "E1204", {"start": v(-43.68, -14.58) * mm, "end": v(-43.68, -15.28) * mm});
            skLineSegment(sketch, "E1205", {"start": v(-43.68, -15.28) * mm, "end": v(-43.18, -15.5) * mm});
            skLineSegment(sketch, "E1206", {"start": v(-43.18, -15.5) * mm, "end": v(-43.36, -15.62) * mm});
            skLineSegment(sketch, "E1207", {"start": v(-43.36, -15.62) * mm, "end": v(-43, -16.45) * mm});
            skLineSegment(sketch, "E1208", {"start": v(-43, -16.45) * mm, "end": v(-43.2, -16.6) * mm});
            skLineSegment(sketch, "E1209", {"start": v(-43.2, -16.6) * mm, "end": v(-44.03, -16.24) * mm});
            skLineSegment(sketch, "E1210", {"start": v(-44.03, -16.24) * mm, "end": v(-43.83, -15.8) * mm});
            skLineSegment(sketch, "E1211", {"start": v(-43.83, -15.8) * mm, "end": v(-44.05, -15.63) * mm});
            skLineSegment(sketch, "E1212", {"start": v(-44.05, -15.63) * mm, "end": v(-44.66, -15.7) * mm});
            skLineSegment(sketch, "E1213", {"start": v(-44.66, -15.7) * mm, "end": v(-44.66, -15.9) * mm});
            skLineSegment(sketch, "E1214", {"start": v(-44.66, -15.9) * mm, "end": v(-44.78, -15.9) * mm});
            skLineSegment(sketch, "E1215", {"start": v(-44.78, -15.9) * mm, "end": v(-44.87, -15.81) * mm});
            skLineSegment(sketch, "E1216", {"start": v(-44.87, -15.81) * mm, "end": v(-45.78, -15.83) * mm});
            skLineSegment(sketch, "E1217", {"start": v(-45.78, -15.83) * mm, "end": v(-45.87, -16.01) * mm});
            skLineSegment(sketch, "E1218", {"start": v(-45.87, -16.01) * mm, "end": v(-45.5, -16.5) * mm});
            skLineSegment(sketch, "E1219", {"start": v(-45.5, -16.5) * mm, "end": v(-45.6, -17.19) * mm});
            skLineSegment(sketch, "E1220", {"start": v(-45.6, -17.19) * mm, "end": v(-45.17, -17.67) * mm});
            skLineSegment(sketch, "E1221", {"start": v(-45.17, -17.67) * mm, "end": v(-44.69, -17.64) * mm});
            skLineSegment(sketch, "E1222", {"start": v(-44.69, -17.64) * mm, "end": v(-44.1, -17.9) * mm});
            skLineSegment(sketch, "E1223", {"start": v(-44.1, -17.9) * mm, "end": v(-43.44, -17.75) * mm});
            skLineSegment(sketch, "E1224", {"start": v(-43.44, -17.75) * mm, "end": v(-43.31, -17.95) * mm});
            skLineSegment(sketch, "E1225", {"start": v(-43.31, -17.95) * mm, "end": v(-43.57, -18.9) * mm});
            skLineSegment(sketch, "E1226", {"start": v(-34.84, -14.17) * mm, "end": v(-34.84, -23.66) * mm});
            skLineSegment(sketch, "E1227", {"start": v(-34.84, -23.66) * mm, "end": v(-34.7, -23.92) * mm});
            skLineSegment(sketch, "E1228", {"start": v(-34.7, -23.92) * mm, "end": v(-34.43, -23.86) * mm});
            skLineSegment(sketch, "E1229", {"start": v(-34.43, -23.86) * mm, "end": v(-34.3, -23.86) * mm});
            skLineSegment(sketch, "E1230", {"start": v(-34.3, -23.86) * mm, "end": v(-34.1, -23.72) * mm});
            skLineSegment(sketch, "E1231", {"start": v(-34.1, -23.72) * mm, "end": v(-33.93, -23.77) * mm});
            skLineSegment(sketch, "E1232", {"start": v(-33.93, -23.77) * mm, "end": v(-33.9, -24.08) * mm});
            skLineSegment(sketch, "E1233", {"start": v(-33.9, -24.08) * mm, "end": v(-33.2, -24.73) * mm});
            skLineSegment(sketch, "E1234", {"start": v(-33.2, -24.73) * mm, "end": v(-33.04, -25.12) * mm});
            skLineSegment(sketch, "E1235", {"start": v(-33.04, -25.12) * mm, "end": v(-32.5, -24.86) * mm});
            skLineSegment(sketch, "E1236", {"start": v(-32.5, -24.86) * mm, "end": v(-32.48, -24.44) * mm});
            skLineSegment(sketch, "E1237", {"start": v(-32.48, -24.44) * mm, "end": v(-32.21, -24.3) * mm});
            skLineSegment(sketch, "E1238", {"start": v(-31.86, -24.4) * mm, "end": v(-31.72, -24.8) * mm});
            skLineSegment(sketch, "E1239", {"start": v(-31.72, -24.8) * mm, "end": v(-31.45, -24.8) * mm});
            skLineSegment(sketch, "E1240", {"start": v(-31.45, -24.8) * mm, "end": v(-31.4, -25.23) * mm});
            skLineSegment(sketch, "E1241", {"start": v(-32.21, -24.3) * mm, "end": v(-31.86, -24.4) * mm});
            skLineSegment(sketch, "E1242", {"start": v(-31.4, -25.23) * mm, "end": v(-31, -25.23) * mm});
            skLineSegment(sketch, "E1243", {"start": v(-31, -25.23) * mm, "end": v(-30.56, -26.08) * mm});
            skLineSegment(sketch, "E1244", {"start": v(-30.56, -26.08) * mm, "end": v(-30.05, -26.65) * mm});
            skLineSegment(sketch, "E1245", {"start": v(-30.05, -26.65) * mm, "end": v(-29.9, -27.13) * mm});
            skLineSegment(sketch, "E1246", {"start": v(-29.9, -27.13) * mm, "end": v(-28.73, -27.5) * mm});
            skLineSegment(sketch, "E1247", {"start": v(-28.73, -27.5) * mm, "end": v(-28.6, -28.24) * mm});
            skLineSegment(sketch, "E1248", {"start": v(-28.6, -28.24) * mm, "end": v(-28.87, -28.93) * mm});
            skLineSegment(sketch, "E1249", {"start": v(-28.87, -28.93) * mm, "end": v(-29.01, -28.84) * mm});
            skLineSegment(sketch, "E1250", {"start": v(-29.01, -28.84) * mm, "end": v(-29.12, -28.56) * mm});
            skLineSegment(sketch, "E1251", {"start": v(-29.12, -28.56) * mm, "end": v(-29.62, -28.26) * mm});
            skLineSegment(sketch, "E1252", {"start": v(-29.62, -28.26) * mm, "end": v(-29.77, -28.32) * mm});
            skLineSegment(sketch, "E1253", {"start": v(-29.77, -28.32) * mm, "end": v(-29.61, -28.54) * mm});
            skLineSegment(sketch, "E1254", {"start": v(-29.61, -28.54) * mm, "end": v(-29.61, -29.11) * mm});
            skLineSegment(sketch, "E1255", {"start": v(-29.61, -29.11) * mm, "end": v(-29.9, -28.87) * mm});
            skLineSegment(sketch, "E1256", {"start": v(-29.9, -28.87) * mm, "end": v(-30.19, -28.66) * mm});
            skLineSegment(sketch, "E1257", {"start": v(-30.19, -28.66) * mm, "end": v(-29.96, -29.08) * mm});
            skLineSegment(sketch, "E1258", {"start": v(-29.96, -29.08) * mm, "end": v(-30.06, -29.2) * mm});
            skLineSegment(sketch, "E1259", {"start": v(-30.06, -29.2) * mm, "end": v(-30.5, -28.46) * mm});
            skLineSegment(sketch, "E1260", {"start": v(-30.5, -28.46) * mm, "end": v(-30.61, -28.57) * mm});
            skLineSegment(sketch, "E1261", {"start": v(-30.53, -28.2) * mm, "end": v(-30.68, -28.08) * mm});
            skLineSegment(sketch, "E1262", {"start": v(-30.68, -28.08) * mm, "end": v(-30.68, -27.52) * mm});
            skLineSegment(sketch, "E1263", {"start": v(-30.68, -27.52) * mm, "end": v(-30.88, -27.88) * mm});
            skLineSegment(sketch, "E1264", {"start": v(-30.88, -27.88) * mm, "end": v(-31.06, -28) * mm});
            skLineSegment(sketch, "E1265", {"start": v(-31.06, -28) * mm, "end": v(-31.18, -27.13) * mm});
            skLineSegment(sketch, "E1266", {"start": v(-31.18, -27.13) * mm, "end": v(-31.3, -27.06) * mm});
            skLineSegment(sketch, "E1267", {"start": v(-31.3, -27.06) * mm, "end": v(-31.3, -27.73) * mm});
            skLineSegment(sketch, "E1268", {"start": v(-31.3, -27.73) * mm, "end": v(-31.79, -27.02) * mm});
            skLineSegment(sketch, "E1269", {"start": v(-31.79, -27.02) * mm, "end": v(-32.1, -26.96) * mm});
            skLineSegment(sketch, "E1270", {"start": v(-32.1, -26.96) * mm, "end": v(-32.12, -26.56) * mm});
            skLineSegment(sketch, "E1271", {"start": v(-32.12, -26.56) * mm, "end": v(-32.28, -26.24) * mm});
            skLineSegment(sketch, "E1272", {"start": v(-32.28, -26.24) * mm, "end": v(-32.53, -26.06) * mm});
            skLineSegment(sketch, "E1273", {"start": v(-32.53, -26.06) * mm, "end": v(-32.53, -25.85) * mm});
            skLineSegment(sketch, "E1274", {"start": v(-32.53, -25.85) * mm, "end": v(-32.2, -25.7) * mm});
            skLineSegment(sketch, "E1275", {"start": v(-32.2, -25.7) * mm, "end": v(-32.32, -25.61) * mm});
            skLineSegment(sketch, "E1276", {"start": v(-32.32, -25.61) * mm, "end": v(-32.55, -25.75) * mm});
            skLineSegment(sketch, "E1277", {"start": v(-32.55, -25.75) * mm, "end": v(-33.03, -25.4) * mm});
            skLineSegment(sketch, "E1278", {"start": v(-33.03, -25.4) * mm, "end": v(-33.16, -25.22) * mm});
            skLineSegment(sketch, "E1279", {"start": v(-33.16, -25.22) * mm, "end": v(-34.24, -24.6) * mm});
            skLineSegment(sketch, "E1280", {"start": v(-34.24, -24.6) * mm, "end": v(-34.06, -24.28) * mm});
            skLineSegment(sketch, "E1281", {"start": v(-34.06, -24.28) * mm, "end": v(-34.05, -23.96) * mm});
            skLineSegment(sketch, "E1282", {"start": v(-34.05, -23.96) * mm, "end": v(-34.52, -24.3) * mm});
            skLineSegment(sketch, "E1283", {"start": v(-34.52, -24.3) * mm, "end": v(-35.6, -23.92) * mm});
            skLineSegment(sketch, "E1284", {"start": v(-35.6, -23.92) * mm, "end": v(-36.22, -23.9) * mm});
            skLineSegment(sketch, "E1285", {"start": v(-36.22, -23.9) * mm, "end": v(-36.3, -23.98) * mm});
            skLineSegment(sketch, "E1286", {"start": v(-36.3, -23.98) * mm, "end": v(-36.96, -23.55) * mm});
            skLineSegment(sketch, "E1287", {"start": v(-36.96, -23.55) * mm, "end": v(-37.17, -23.53) * mm});
            skLineSegment(sketch, "E1288", {"start": v(-37.17, -23.53) * mm, "end": v(-37.52, -22.9) * mm});
            skLineSegment(sketch, "E1289", {"start": v(-37.52, -22.9) * mm, "end": v(-37.85, -22.89) * mm});
            skLineSegment(sketch, "E1290", {"start": v(-37.85, -22.89) * mm, "end": v(-38.34, -23.07) * mm});
            skLineSegment(sketch, "E1291", {"start": v(-38.34, -23.07) * mm, "end": v(-38.33, -23.48) * mm});
            skLineSegment(sketch, "E1292", {"start": v(-38.33, -23.48) * mm, "end": v(-38.16, -23.5) * mm});
            skLineSegment(sketch, "E1293", {"start": v(-38.16, -23.5) * mm, "end": v(-38.21, -23.74) * mm});
            skLineSegment(sketch, "E1294", {"start": v(-38.21, -23.74) * mm, "end": v(-38.39, -23.92) * mm});
            skLineSegment(sketch, "E1295", {"start": v(-38.39, -23.92) * mm, "end": v(-38.55, -23.78) * mm});
            skLineSegment(sketch, "E1296", {"start": v(-38.55, -23.78) * mm, "end": v(-38.7, -23.91) * mm});
            skLineSegment(sketch, "E1297", {"start": v(-38.7, -23.91) * mm, "end": v(-38.97, -23.7) * mm});
            skLineSegment(sketch, "E1298", {"start": v(-38.97, -23.7) * mm, "end": v(-39.33, -23.95) * mm});
            skLineSegment(sketch, "E1299", {"start": v(-39.33, -23.95) * mm, "end": v(-39.86, -24.4) * mm});
            skLineSegment(sketch, "E1300", {"start": v(-39.86, -24.4) * mm, "end": v(-40.47, -24.4) * mm});
            skLineSegment(sketch, "E1301", {"start": v(-40.47, -24.4) * mm, "end": v(-40.5, -24.18) * mm});
            skLineSegment(sketch, "E1302", {"start": v(-40.5, -24.18) * mm, "end": v(-40.1, -24.12) * mm});
            skLineSegment(sketch, "E1303", {"start": v(-40.1, -24.12) * mm, "end": v(-40.07, -23.94) * mm});
            skLineSegment(sketch, "E1304", {"start": v(-40.07, -23.94) * mm, "end": v(-40.38, -23.87) * mm});
            skLineSegment(sketch, "E1305", {"start": v(-40.38, -23.87) * mm, "end": v(-39.83, -22.83) * mm});
            skLineSegment(sketch, "E1306", {"start": v(-39.83, -22.83) * mm, "end": v(-39.5, -22.66) * mm});
            skLineSegment(sketch, "E1307", {"start": v(-39.5, -22.66) * mm, "end": v(-39.35, -22.8) * mm});
            skLineSegment(sketch, "E1308", {"start": v(-39.35, -22.8) * mm, "end": v(-39.04, -22.81) * mm});
            skLineSegment(sketch, "E1309", {"start": v(-39.04, -22.81) * mm, "end": v(-39.2, -22.5) * mm});
            skLineSegment(sketch, "E1310", {"start": v(-39.2, -22.5) * mm, "end": v(-39.57, -22.41) * mm});
            skLineSegment(sketch, "E1311", {"start": v(-39.57, -22.41) * mm, "end": v(-40.2, -22.74) * mm});
            skLineSegment(sketch, "E1312", {"start": v(-40.2, -22.74) * mm, "end": v(-40.73, -23.68) * mm});
            skLineSegment(sketch, "E1313", {"start": v(-40.73, -23.68) * mm, "end": v(-41.25, -23.86) * mm});
            skLineSegment(sketch, "E1314", {"start": v(-41.25, -23.86) * mm, "end": v(-41.6, -24.17) * mm});
            skLineSegment(sketch, "E1315", {"start": v(-41.6, -24.17) * mm, "end": v(-41.58, -24.3) * mm});
            skLineSegment(sketch, "E1316", {"start": v(-41.58, -24.3) * mm, "end": v(-41.4, -24.43) * mm});
            skLineSegment(sketch, "E1317", {"start": v(-41.4, -24.43) * mm, "end": v(-41.26, -24.66) * mm});
            skLineSegment(sketch, "E1318", {"start": v(-41.26, -24.66) * mm, "end": v(-41.54, -24.97) * mm});
            skLineSegment(sketch, "E1319", {"start": v(-41.54, -24.97) * mm, "end": v(-43.38, -26.06) * mm});
            skLineSegment(sketch, "E1320", {"start": v(-43.38, -26.06) * mm, "end": v(-44.5, -26.43) * mm});
            skLineSegment(sketch, "E1321", {"start": v(-44.5, -26.43) * mm, "end": v(-44.35, -26.6) * mm});
            skLineSegment(sketch, "E1322", {"start": v(-44.35, -26.6) * mm, "end": v(-44.56, -26.87) * mm});
            skLineSegment(sketch, "E1323", {"start": v(-44.56, -26.87) * mm, "end": v(-44.85, -26.78) * mm});
            skLineSegment(sketch, "E1324", {"start": v(-44.85, -26.78) * mm, "end": v(-45.14, -26.77) * mm});
            skLineSegment(sketch, "E1325", {"start": v(-45.14, -26.77) * mm, "end": v(-45.26, -26.94) * mm});
            skLineSegment(sketch, "E1326", {"start": v(-45.26, -26.94) * mm, "end": v(-45.34, -26.8) * mm});
            skLineSegment(sketch, "E1327", {"start": v(-45.34, -26.8) * mm, "end": v(-46.02, -27.02) * mm});
            skLineSegment(sketch, "E1328", {"start": v(-46.02, -27.02) * mm, "end": v(-46.45, -26.86) * mm});
            skLineSegment(sketch, "E1329", {"start": v(-46.45, -26.86) * mm, "end": v(-46.73, -27.08) * mm});
            skLineSegment(sketch, "E1330", {"start": v(-46.73, -27.08) * mm, "end": v(-47.11, -27.07) * mm});
            skLineSegment(sketch, "E1331", {"start": v(-47.11, -27.07) * mm, "end": v(-47.49, -27.31) * mm});
            skLineSegment(sketch, "E1332", {"start": v(-47.49, -27.31) * mm, "end": v(-48.04, -27.19) * mm});
            skLineSegment(sketch, "E1333", {"start": v(-48.04, -27.19) * mm, "end": v(-48.4, -27.33) * mm});
            skLineSegment(sketch, "E1334", {"start": v(-48.4, -27.33) * mm, "end": v(-48.63, -27.2) * mm});
            skLineSegment(sketch, "E1335", {"start": v(-48.63, -27.2) * mm, "end": v(-48.6, -26.96) * mm});
            skLineSegment(sketch, "E1336", {"start": v(-48.6, -26.96) * mm, "end": v(-48.34, -26.83) * mm});
            skLineSegment(sketch, "E1337", {"start": v(-48.34, -26.83) * mm, "end": v(-47.63, -26.92) * mm});
            skLineSegment(sketch, "E1338", {"start": v(-47.63, -26.92) * mm, "end": v(-47.32, -26.82) * mm});
            skLineSegment(sketch, "E1339", {"start": v(-47.32, -26.82) * mm, "end": v(-47.18, -26.75) * mm});
            skLineSegment(sketch, "E1340", {"start": v(-47.18, -26.75) * mm, "end": v(-46.82, -26.45) * mm});
            skLineSegment(sketch, "E1341", {"start": v(-46.82, -26.45) * mm, "end": v(-46.6, -26.41) * mm});
            skLineSegment(sketch, "E1342", {"start": v(-46.6, -26.41) * mm, "end": v(-46.3, -26.31) * mm});
            skLineSegment(sketch, "E1343", {"start": v(-46.3, -26.31) * mm, "end": v(-46.08, -26.34) * mm});
            skLineSegment(sketch, "E1344", {"start": v(-46.08, -26.34) * mm, "end": v(-45.95, -26.5) * mm});
            skLineSegment(sketch, "E1345", {"start": v(-45.95, -26.5) * mm, "end": v(-45.72, -26.49) * mm});
            skLineSegment(sketch, "E1346", {"start": v(-45.72, -26.49) * mm, "end": v(-45.42, -26.13) * mm});
            skLineSegment(sketch, "E1347", {"start": v(-45.42, -26.13) * mm, "end": v(-44.63, -25.96) * mm});
            skLineSegment(sketch, "E1348", {"start": v(-44.63, -25.96) * mm, "end": v(-44.52, -26) * mm});
            skLineSegment(sketch, "E1349", {"start": v(-44.52, -26) * mm, "end": v(-44.37, -25.6) * mm});
            skLineSegment(sketch, "E1350", {"start": v(-44.37, -25.6) * mm, "end": v(-43.88, -25.42) * mm});
            skLineSegment(sketch, "E1351", {"start": v(-43.88, -25.42) * mm, "end": v(-43.47, -24.55) * mm});
            skLineSegment(sketch, "E1352", {"start": v(-43.47, -24.55) * mm, "end": v(-43.22, -24.37) * mm});
            skLineSegment(sketch, "E1353", {"start": v(-43.22, -24.37) * mm, "end": v(-43.17, -24.03) * mm});
            skLineSegment(sketch, "E1354", {"start": v(-43.17, -24.03) * mm, "end": v(-43.62, -24.25) * mm});
            skLineSegment(sketch, "E1355", {"start": v(-43.62, -24.25) * mm, "end": v(-43.83, -24.04) * mm});
            skLineSegment(sketch, "E1356", {"start": v(-43.83, -24.04) * mm, "end": v(-43.97, -24) * mm});
            skLineSegment(sketch, "E1357", {"start": v(-43.97, -24) * mm, "end": v(-44.15, -24.08) * mm});
            skLineSegment(sketch, "E1358", {"start": v(-44.15, -24.08) * mm, "end": v(-44.17, -24.38) * mm});
            skLineSegment(sketch, "E1359", {"start": v(-44.17, -24.38) * mm, "end": v(-44.28, -24.38) * mm});
            skLineSegment(sketch, "E1360", {"start": v(-44.28, -24.38) * mm, "end": v(-44.4, -23.72) * mm});
            skLineSegment(sketch, "E1361", {"start": v(-44.4, -23.72) * mm, "end": v(-44.55, -23.84) * mm});
            skLineSegment(sketch, "E1362", {"start": v(-44.55, -23.84) * mm, "end": v(-44.66, -23.86) * mm});
            skLineSegment(sketch, "E1363", {"start": v(-44.66, -23.86) * mm, "end": v(-44.7, -23.64) * mm});
            skLineSegment(sketch, "E1364", {"start": v(-44.7, -23.64) * mm, "end": v(-45.17, -23.66) * mm});
            skLineSegment(sketch, "E1365", {"start": v(-45.17, -23.66) * mm, "end": v(-45.45, -23.78) * mm});
            skLineSegment(sketch, "E1366", {"start": v(-45.45, -23.78) * mm, "end": v(-45.74, -23.74) * mm});
            skLineSegment(sketch, "E1367", {"start": v(-45.74, -23.74) * mm, "end": v(-45.52, -23.48) * mm});
            skLineSegment(sketch, "E1368", {"start": v(-45.52, -23.48) * mm, "end": v(-45.55, -23.05) * mm});
            skLineSegment(sketch, "E1369", {"start": v(-45.55, -23.05) * mm, "end": v(-45.2, -22.98) * mm});
            skLineSegment(sketch, "E1370", {"start": v(-45.2, -22.98) * mm, "end": v(-45.34, -22.81) * mm});
            skLineSegment(sketch, "E1371", {"start": v(-45.34, -22.81) * mm, "end": v(-45.28, -22.3) * mm});
            skLineSegment(sketch, "E1372", {"start": v(-45.28, -22.3) * mm, "end": v(-45.48, -22.13) * mm});
            skLineSegment(sketch, "E1373", {"start": v(-45.48, -22.13) * mm, "end": v(-45.58, -22.32) * mm});
            skLineSegment(sketch, "E1374", {"start": v(-45.58, -22.32) * mm, "end": v(-46.2, -22.3) * mm});
            skLineSegment(sketch, "E1375", {"start": v(-46.2, -22.3) * mm, "end": v(-46.37, -22.16) * mm});
            skLineSegment(sketch, "E1376", {"start": v(-46.37, -22.16) * mm, "end": v(-46.44, -21.79) * mm});
            skLineSegment(sketch, "E1377", {"start": v(-46.44, -21.79) * mm, "end": v(-46.62, -21.4) * mm});
            skLineSegment(sketch, "E1378", {"start": v(-46.62, -21.4) * mm, "end": v(-46.66, -21.2) * mm});
            skLineSegment(sketch, "E1379", {"start": v(-46.66, -21.2) * mm, "end": v(-46.43, -21.14) * mm});
            skLineSegment(sketch, "E1380", {"start": v(-46.43, -21.14) * mm, "end": v(-46.44, -20.93) * mm});
            skLineSegment(sketch, "E1381", {"start": v(-46.44, -20.93) * mm, "end": v(-46.27, -20.82) * mm});
            skLineSegment(sketch, "E1382", {"start": v(-46.27, -20.82) * mm, "end": v(-46.37, -20.76) * mm});
            skLineSegment(sketch, "E1383", {"start": v(-46.37, -20.76) * mm, "end": v(-46.5, -20.79) * mm});
            skLineSegment(sketch, "E1384", {"start": v(-46.5, -20.79) * mm, "end": v(-46.64, -20.5) * mm});
            skLineSegment(sketch, "E1385", {"start": v(-46.64, -20.5) * mm, "end": v(-46.57, -19.9) * mm});
            skLineSegment(sketch, "E1386", {"start": v(-46.57, -19.9) * mm, "end": v(-45.77, -19.4) * mm});
            skLineSegment(sketch, "E1387", {"start": v(-45.77, -19.4) * mm, "end": v(-45.55, -19) * mm});
            skLineSegment(sketch, "E1388", {"start": v(-45.55, -19) * mm, "end": v(-45.26, -18.84) * mm});
            skLineSegment(sketch, "E1389", {"start": v(-45.26, -18.84) * mm, "end": v(-45, -18.9) * mm});
            skLineSegment(sketch, "E1390", {"start": v(-45, -18.9) * mm, "end": v(-44.92, -19.24) * mm});
            skLineSegment(sketch, "E1391", {"start": v(-44.92, -19.24) * mm, "end": v(-44.6, -19.18) * mm});
            skLineSegment(sketch, "E1392", {"start": v(-44.6, -19.18) * mm, "end": v(-44.27, -18.98) * mm});
            skLineSegment(sketch, "E1393", {"start": v(-44.27, -18.98) * mm, "end": v(-44, -19.12) * mm});
            skLineSegment(sketch, "E1394", {"start": v(-44, -19.12) * mm, "end": v(-43.84, -19.12) * mm});
            skLineSegment(sketch, "E1395", {"start": v(-43.84, -19.12) * mm, "end": v(-43.57, -18.9) * mm});
            skLineSegment(sketch, "E1396", {"start": v(-26.02, -21.18) * mm, "end": v(-26.22, -21.48) * mm});
            skLineSegment(sketch, "E1397", {"start": v(-26.22, -21.48) * mm, "end": v(-26.55, -21.5) * mm});
            skLineSegment(sketch, "E1398", {"start": v(-26.55, -21.5) * mm, "end": v(-26.36, -21.12) * mm});
            skLineSegment(sketch, "E1399", {"start": v(-26.36, -21.12) * mm, "end": v(-26.11, -21.07) * mm});
            skLineSegment(sketch, "E1400", {"start": v(-26.11, -21.07) * mm, "end": v(-26.02, -21.18) * mm});
            skLineSegment(sketch, "E1401", {"start": v(-24.78, -21.37) * mm, "end": v(-25.39, -21.07) * mm});
            skLineSegment(sketch, "E1402", {"start": v(-25.39, -21.07) * mm, "end": v(-25.35, -20.65) * mm});
            skLineSegment(sketch, "E1403", {"start": v(-25.35, -20.65) * mm, "end": v(-24.86, -20.46) * mm});
            skLineSegment(sketch, "E1404", {"start": v(-24.86, -20.46) * mm, "end": v(-24.4, -20.53) * mm});
            skLineSegment(sketch, "E1405", {"start": v(-24.4, -20.53) * mm, "end": v(-24.37, -20.92) * mm});
            skLineSegment(sketch, "E1406", {"start": v(-24.37, -20.92) * mm, "end": v(-24.46, -21.34) * mm});
            skLineSegment(sketch, "E1407", {"start": v(-24.46, -21.34) * mm, "end": v(-24.78, -21.37) * mm});
            skLineSegment(sketch, "E1408", {"start": v(-20.55, -22.66) * mm, "end": v(-20.86, -22.51) * mm});
            skLineSegment(sketch, "E1409", {"start": v(-20.86, -22.51) * mm, "end": v(-21.29, -21.68) * mm});
            skLineSegment(sketch, "E1410", {"start": v(-21.29, -21.68) * mm, "end": v(-21.98, -22) * mm});
            skLineSegment(sketch, "E1411", {"start": v(-21.98, -22) * mm, "end": v(-22.04, -22.2) * mm});
            skLineSegment(sketch, "E1412", {"start": v(-22.04, -22.2) * mm, "end": v(-21.62, -22.82) * mm});
            skLineSegment(sketch, "E1413", {"start": v(-21.62, -22.82) * mm, "end": v(-21.2, -22.73) * mm});
            skLineSegment(sketch, "E1414", {"start": v(-21.2, -22.73) * mm, "end": v(-21.06, -22.87) * mm});
            skLineSegment(sketch, "E1415", {"start": v(-21.06, -22.87) * mm, "end": v(-20.64, -22.86) * mm});
            skLineSegment(sketch, "E1416", {"start": v(-20.64, -22.86) * mm, "end": v(-20.55, -22.66) * mm});
            skLineSegment(sketch, "E1417", {"start": v(-19.66, -22.97) * mm, "end": v(-19.8, -23.18) * mm});
            skLineSegment(sketch, "E1418", {"start": v(-19.8, -23.18) * mm, "end": v(-19.36, -23.34) * mm});
            skLineSegment(sketch, "E1419", {"start": v(-19.36, -23.34) * mm, "end": v(-18.7, -23.42) * mm});
            skLineSegment(sketch, "E1420", {"start": v(-18.7, -23.42) * mm, "end": v(-18.41, -23.25) * mm});
            skLineSegment(sketch, "E1421", {"start": v(-18.41, -23.25) * mm, "end": v(-18.41, -23.07) * mm});
            skLineSegment(sketch, "E1422", {"start": v(-18.41, -23.07) * mm, "end": v(-19.1, -23.06) * mm});
            skLineSegment(sketch, "E1423", {"start": v(-19.1, -23.06) * mm, "end": v(-19.16, -23.15) * mm});
            skLineSegment(sketch, "E1424", {"start": v(-19.16, -23.15) * mm, "end": v(-19.4, -23) * mm});
            skLineSegment(sketch, "E1425", {"start": v(-19.4, -23) * mm, "end": v(-19.66, -22.97) * mm});
            skLineSegment(sketch, "E1426", {"start": v(-18.75, -23.65) * mm, "end": v(-18.63, -23.8) * mm});
            skLineSegment(sketch, "E1427", {"start": v(-18.63, -23.8) * mm, "end": v(-18.62, -24.02) * mm});
            skLineSegment(sketch, "E1428", {"start": v(-18.62, -24.02) * mm, "end": v(-19.02, -24.2) * mm});
            skLineSegment(sketch, "E1429", {"start": v(-19.02, -24.2) * mm, "end": v(-19.22, -23.7) * mm});
            skLineSegment(sketch, "E1430", {"start": v(-19.22, -23.7) * mm, "end": v(-18.75, -23.65) * mm});
            skLineSegment(sketch, "E1431", {"start": v(-18.45, -23.62) * mm, "end": v(-18.17, -23.28) * mm});
            skLineSegment(sketch, "E1432", {"start": v(-18.17, -23.28) * mm, "end": v(-17.68, -23.56) * mm});
            skLineSegment(sketch, "E1433", {"start": v(-17.68, -23.56) * mm, "end": v(-17.27, -23.67) * mm});
            skLineSegment(sketch, "E1434", {"start": v(-17.27, -23.67) * mm, "end": v(-16.7, -23.98) * mm});
            skLineSegment(sketch, "E1435", {"start": v(-16.7, -23.98) * mm, "end": v(-16.7, -24.18) * mm});
            skLineSegment(sketch, "E1436", {"start": v(-16.7, -24.18) * mm, "end": v(-17.6, -24.53) * mm});
            skLineSegment(sketch, "E1437", {"start": v(-17.6, -24.53) * mm, "end": v(-17.86, -24.38) * mm});
            skLineSegment(sketch, "E1438", {"start": v(-17.86, -24.38) * mm, "end": v(-18.45, -23.62) * mm});
            skLineSegment(sketch, "E1439", {"start": v(-15.06, -27.62) * mm, "end": v(-14.96, -27.7) * mm});
            skLineSegment(sketch, "E1440", {"start": v(-14.96, -27.7) * mm, "end": v(-14.46, -27.58) * mm});
            skLineSegment(sketch, "E1441", {"start": v(-14.46, -27.58) * mm, "end": v(-13.96, -27.13) * mm});
            skLineSegment(sketch, "E1442", {"start": v(-13.96, -27.13) * mm, "end": v(-14.48, -26.77) * mm});
            skLineSegment(sketch, "E1443", {"start": v(-14.48, -26.77) * mm, "end": v(-14.77, -26.07) * mm});
            skLineSegment(sketch, "E1444", {"start": v(-14.77, -26.07) * mm, "end": v(-16.4, -25.25) * mm});
            skLineSegment(sketch, "E1445", {"start": v(-16.4, -25.25) * mm, "end": v(-16.6, -25.35) * mm});
            skLineSegment(sketch, "E1446", {"start": v(-16.6, -25.35) * mm, "end": v(-16.38, -25.78) * mm});
            skLineSegment(sketch, "E1447", {"start": v(-16.38, -25.78) * mm, "end": v(-16.6, -26.16) * mm});
            skLineSegment(sketch, "E1448", {"start": v(-16.6, -26.16) * mm, "end": v(-16.87, -26.25) * mm});
            skLineSegment(sketch, "E1449", {"start": v(-16.87, -26.25) * mm, "end": v(-16.95, -26.59) * mm});
            skLineSegment(sketch, "E1450", {"start": v(-16.95, -26.59) * mm, "end": v(-16.68, -26.8) * mm});
            skLineSegment(sketch, "E1451", {"start": v(-16.68, -26.8) * mm, "end": v(-16.5, -27.47) * mm});
            skLineSegment(sketch, "E1452", {"start": v(-16.5, -27.47) * mm, "end": v(-16.55, -28.2) * mm});
            skLineSegment(sketch, "E1453", {"start": v(-16.55, -28.2) * mm, "end": v(-16.04, -28.55) * mm});
            skLineSegment(sketch, "E1454", {"start": v(-16.04, -28.55) * mm, "end": v(-15.4, -27.83) * mm});
            skLineSegment(sketch, "E1455", {"start": v(-15.4, -27.83) * mm, "end": v(-15.06, -27.62) * mm});
            skLineSegment(sketch, "E1456", {"start": v(26.15, -3.3) * mm, "end": v(26.15, -3.3) * mm});
            skLineSegment(sketch, "E1457", {"start": v(-10.83, 0.24) * mm, "end": v(-10.37, 7.64) * mm});
            skLineSegment(sketch, "E1458", {"start": v(-12.62, 0.37) * mm, "end": v(-10.83, 0.24) * mm});
            skLineSegment(sketch, "E1459", {"start": v(-10.83, 0.24) * mm, "end": v(0.07, -0.1) * mm});
            skLineSegment(sketch, "E1460", {"start": v(0.07, -0.1) * mm, "end": v(3.4, -0.12) * mm});
            skLineSegment(sketch, "E1461", {"start": v(-22.96, 11.38) * mm, "end": v(-17.89, 10.74) * mm});
            skLineSegment(sketch, "E1462", {"start": v(-17.89, 10.74) * mm, "end": v(-13.86, 10.37) * mm});
            skLineSegment(sketch, "E1463", {"start": v(-13.86, 10.37) * mm, "end": v(-10.22, 10.07) * mm});
            skLineSegment(sketch, "E1464", {"start": v(-13.46, 15.24) * mm, "end": v(-13.86, 10.37) * mm});
            skLineSegment(sketch, "E1465", {"start": v(-13.46, 15.24) * mm, "end": v(-13.08, 20.1) * mm});
            skLineSegment(sketch, "E1466", {"start": v(-30.53, -28.2) * mm, "end": v(-30.61, -28.57) * mm});
            skLineSegment(sketch, "E1467", {"start": v(-24.2, 1.61) * mm, "end": v(-12.62, 0.37) * mm});
            skLineSegment(sketch, "E1468", {"start": v(-33.75, 3.22) * mm, "end": v(-24.2, 1.61) * mm});
            skLineSegment(sketch, "E1469", {"start": v(-24.2, 1.61) * mm, "end": v(-26.15, -12.1) * mm});
            skSolve(sketch);
        }
        {
            var Q0;
            Q0=makeQuery(id+"F2.imprint","IMPRINT",FACE,{"disambiguationData":[TD([[makeQuery(id+"F2.imprint","IMPRINT",EDGE,{"derivedFrom":sQuery(id+"F2.wireOp",EDGE,"E11")}),1.0]])]});
            extrude(context, id + "F3", {"entities" : qUnion([Q0]), "operationType" : NewBodyOperationType.ADD, "depth" : 4.23 * mm, "offsetDistance" : 25.4 * mm});
        }
        {
            var Q0;
            {var subQ0=sQuery(id+"F2.wireOp",EDGE,"E18");Q0=makeQuery(id+"F2.imprint","IMPRINT",FACE,{"disambiguationData":[TD([[makeQuery(id+"F2.imprint","IMPRINT",EDGE,{"derivedFrom":subQ0}),1.0]])]});}
            extrude(context, id + "F4", {"entities" : qUnion([Q0]), "operationType" : NewBodyOperationType.ADD, "depth" : 30.8 * mm, "offsetDistance" : 25.4 * mm});
        }
        {
            var Q0;
            Q0=makeQuery(id+"F2.imprint","IMPRINT",FACE,{"disambiguationData":[TD([[makeQuery(id+"F2.imprint","IMPRINT",EDGE,{"derivedFrom":sQuery(id+"F2.wireOp",EDGE,"E1")}),-1.0]])]});
            extrude(context, id + "F5", {"entities" : qUnion([Q0]), "operationType" : NewBodyOperationType.ADD, "depth" : 21.25 * mm, "offsetDistance" : 25.4 * mm});
        }
        {
            var Q0;
            Q0=makeQuery(id+"F2.imprint","IMPRINT",FACE,{"disambiguationData":[TD([[makeQuery(id+"F2.imprint","IMPRINT",EDGE,{"derivedFrom":sQuery(id+"F2.wireOp",EDGE,"E44")}),1.0]])]});
            extrude(context, id + "F6", {"entities" : qUnion([Q0]), "operationType" : NewBodyOperationType.ADD, "depth" : 15.79 * mm, "offsetDistance" : 25.4 * mm});
        }
        {
            var Q0;
            Q0=makeQuery(id+"F2.imprint","IMPRINT",FACE,{"disambiguationData":[TD([[makeQuery(id+"F2.imprint","IMPRINT",EDGE,{"derivedFrom":sQuery(id+"F2.wireOp",EDGE,"E317")}),1.0]])]});
            extrude(context, id + "F7", {"entities" : qUnion([Q0]), "operationType" : NewBodyOperationType.ADD, "depth" : 15.71 * mm, "offsetDistance" : 25.4 * mm});
        }
        {
            var Q0;
            Q0=makeQuery(id+"F2.imprint","IMPRINT",FACE,{"disambiguationData":[TD([[makeQuery(id+"F2.imprint","IMPRINT",EDGE,{"derivedFrom":sQuery(id+"F2.wireOp",EDGE,"E40")}),-1.0]])]});
            extrude(context, id + "F8", {"entities" : qUnion([Q0]), "operationType" : NewBodyOperationType.ADD, "depth" : 128821350 / 8029672510.6 * mm, "offsetDistance" : 25.4 * mm});
        }
        {
            var Q0;
            Q0=makeQuery(id+"F2.imprint","IMPRINT",FACE,{"disambiguationData":[TD([[makeQuery(id+"F2.imprint","IMPRINT",EDGE,{"derivedFrom":sQuery(id+"F2.wireOp",EDGE,"E44")}),-1.0]])]});
            extrude(context, id + "F9", {"entities" : qUnion([Q0]), "operationType" : NewBodyOperationType.ADD, "depth" : 10.26 * mm, "offsetDistance" : 25.4 * mm});
        }
        {
            var Q0;
            {var subQ0=sQuery(id+"F2.wireOp",EDGE,"E43");Q0=makeQuery(id+"F2.imprint","IMPRINT",FACE,{"disambiguationData":[TD([[makeQuery(id+"F2.imprint","IMPRINT",EDGE,{"derivedFrom":subQ0}),-1.0]])]});}
            extrude(context, id + "F10", {"entities" : qUnion([Q0]), "operationType" : NewBodyOperationType.ADD, "depth" : 9.3 * mm, "offsetDistance" : 25.4 * mm});
        }
        {
            var Q0;
            {var subQ4=sQuery(id+"F2.wireOp",EDGE,"E307");Q0=makeQuery(id+"F2.imprint","IMPRINT",FACE,{"disambiguationData":[TD([[makeQuery(id+"F2.imprint","IMPRINT",EDGE,{"derivedFrom":subQ4}),1.0]])]});}
            extrude(context, id + "F11", {"entities" : qUnion([Q0]), "operationType" : NewBodyOperationType.ADD, "depth" : 8.03 * mm, "offsetDistance" : 25.4 * mm});
        }
        {
            var Q0;
            {var subQ0=sQuery(id+"F2.wireOp",EDGE,"E41");Q0=makeQuery(id+"F2.imprint","IMPRINT",FACE,{"disambiguationData":[TD([[makeQuery(id+"F2.imprint","IMPRINT",EDGE,{"derivedFrom":subQ0}),1.0]])]});}
            var Q1;
            Q1=makeQuery(id+"F2.imprint","IMPRINT",FACE,{"disambiguationData":[TD([[makeQuery(id+"F2.imprint","IMPRINT",EDGE,{"derivedFrom":sQuery(id+"F2.wireOp",EDGE,"E577")}),-1.0]])]});
            extrude(context, id + "F12", {"entities" : qUnion([Q0, Q1]), "operationType" : NewBodyOperationType.ADD, "depth" : 7.95 * mm, "offsetDistance" : 25.4 * mm});
        }
        {
            var Q0;
            {var subQ4=sQuery(id+"F2.wireOp",EDGE,"E692");Q0=makeQuery(id+"F2.imprint","IMPRINT",FACE,{"disambiguationData":[TD([[makeQuery(id+"F2.imprint","IMPRINT",EDGE,{"derivedFrom":subQ4}),-1.0]])]});}
            extrude(context, id + "F13", {"entities" : qUnion([Q0]), "operationType" : NewBodyOperationType.ADD, "depth" : 7.9 * mm, "offsetDistance" : 25.4 * mm});
        }
        {
            var Q0;
            Q0=makeQuery(id+"F2.imprint","IMPRINT",FACE,{"disambiguationData":[TD([[makeQuery(id+"F2.imprint","IMPRINT",EDGE,{"derivedFrom":sQuery(id+"F2.wireOp",EDGE,"E186")}),-1.0]])]});
            extrude(context, id + "F14", {"entities" : qUnion([Q0]), "operationType" : NewBodyOperationType.ADD, "depth" : 7.15 * mm, "offsetDistance" : 25.4 * mm});
        }
        {
            var Q0;
            {var subQ0=sQuery(id+"F2.wireOp",EDGE,"E708");Q0=makeQuery(id+"F2.imprint","IMPRINT",FACE,{"disambiguationData":[TD([[makeQuery(id+"F2.imprint","IMPRINT",EDGE,{"derivedFrom":subQ0}),-1.0]])]});}
            extrude(context, id + "F15", {"entities" : qUnion([Q0]), "operationType" : NewBodyOperationType.ADD, "depth" : 6.64 * mm, "offsetDistance" : 25.4 * mm});
        }
        {
            var Q0;
            {var subQ0=sQuery(id+"F2.wireOp",EDGE,"E49");Q0=makeQuery(id+"F2.imprint","IMPRINT",FACE,{"disambiguationData":[TD([[makeQuery(id+"F2.imprint","IMPRINT",EDGE,{"derivedFrom":subQ0}),-1.0]])]});}
            extrude(context, id + "F16", {"entities" : qUnion([Q0]), "operationType" : NewBodyOperationType.ADD, "depth" : 5.6 * mm, "offsetDistance" : 25.4 * mm});
        }
        {
            var Q0;
            {var subQ3=sQuery(id+"F2.wireOp",EDGE,"E201");Q0=makeQuery(id+"F2.imprint","IMPRINT",FACE,{"disambiguationData":[TD([[makeQuery(id+"F2.imprint","IMPRINT",EDGE,{"derivedFrom":subQ3}),-1.0]])]});}
            extrude(context, id + "F17", {"entities" : qUnion([Q0]), "operationType" : NewBodyOperationType.ADD, "depth" : 5.38 * mm, "offsetDistance" : 25.4 * mm});
        }
        {
            var Q0;
            {var subQ3=sQuery(id+"F2.wireOp",EDGE,"E41");Q0=makeQuery(id+"F2.imprint","IMPRINT",FACE,{"disambiguationData":[TD([[makeQuery(id+"F2.imprint","IMPRINT",EDGE,{"derivedFrom":subQ3}),-1.0]])]});}
            extrude(context, id + "F18", {"entities" : qUnion([Q0]), "operationType" : NewBodyOperationType.ADD, "depth" : 5.28 * mm, "offsetDistance" : 25.4 * mm});
        }
        {
            var Q0;
            Q0=makeQuery(id+"F2.imprint","IMPRINT",FACE,{"disambiguationData":[TD([[makeQuery(id+"F2.imprint","IMPRINT",EDGE,{"derivedFrom":sQuery(id+"F2.wireOp",EDGE,"E51")}),-1.0]])]});
            extrude(context, id + "F19", {"entities" : qUnion([Q0]), "operationType" : NewBodyOperationType.ADD, "depth" : 5.22 * mm, "offsetDistance" : 25.4 * mm});
        }
        {
            var Q0;
            Q0=makeQuery(id+"F2.imprint","IMPRINT",FACE,{"disambiguationData":[TD([[makeQuery(id+"F2.imprint","IMPRINT",EDGE,{"derivedFrom":sQuery(id+"F2.wireOp",EDGE,"E39")}),-1.0]])]});
            extrude(context, id + "F20", {"entities" : qUnion([Q0]), "operationType" : NewBodyOperationType.ADD, "depth" : 4.86 * mm, "offsetDistance" : 25.4 * mm});
        }
        {
            var Q0;
            {var subQ5=sQuery(id+"F2.wireOp",EDGE,"E606");Q0=makeQuery(id+"F2.imprint","IMPRINT",FACE,{"disambiguationData":[TD([[makeQuery(id+"F2.imprint","IMPRINT",EDGE,{"derivedFrom":subQ5}),-1.0]])]});}
            extrude(context, id + "F21", {"entities" : qUnion([Q0]), "operationType" : NewBodyOperationType.ADD, "depth" : 4.76 * mm, "offsetDistance" : 25.4 * mm});
        }
        {
            var Q0;
            Q0=makeQuery(id+"F2.imprint","IMPRINT",FACE,{"disambiguationData":[TD([[makeQuery(id+"F2.imprint","IMPRINT",EDGE,{"derivedFrom":sQuery(id+"F2.wireOp",EDGE,"E40")}),1.0]])]});
            extrude(context, id + "F22", {"entities" : qUnion([Q0]), "operationType" : NewBodyOperationType.ADD, "depth" : 4.61 * mm, "offsetDistance" : 25.4 * mm});
        }
        {
            var Q0;
            {var subQ1=sQuery(id+"F2.wireOp",EDGE,"E261");Q0=makeQuery(id+"F2.imprint","IMPRINT",FACE,{"disambiguationData":[TD([[makeQuery(id+"F2.imprint","IMPRINT",EDGE,{"derivedFrom":subQ1}),-1.0]])]});}
            extrude(context, id + "F23", {"entities" : qUnion([Q0]), "operationType" : NewBodyOperationType.ADD, "depth" : 4.36 * mm, "offsetDistance" : 25.4 * mm});
        }
        {
            var Q0;
            {var subQ0=sQuery(id+"F2.wireOp",EDGE,"E307");Q0=makeQuery(id+"F2.imprint","IMPRINT",FACE,{"disambiguationData":[TD([[makeQuery(id+"F2.imprint","IMPRINT",EDGE,{"derivedFrom":subQ0}),-1.0]])]});}
            extrude(context, id + "F24", {"entities" : qUnion([Q0]), "operationType" : NewBodyOperationType.ADD, "depth" : 3.88 * mm, "offsetDistance" : 25.4 * mm});
        }
        {
            var Q0;
            Q0=makeQuery(id+"F2.imprint","IMPRINT",FACE,{"disambiguationData":[TD([[makeQuery(id+"F2.imprint","IMPRINT",EDGE,{"derivedFrom":sQuery(id+"F2.wireOp",EDGE,"E1076")}),-1.0]])]});
            extrude(context, id + "F25", {"entities" : qUnion([Q0]), "operationType" : NewBodyOperationType.ADD, "depth" : 3.84 * mm, "offsetDistance" : 25.4 * mm});
        }
        {
            var Q0;
            Q0=makeQuery(id+"F2.imprint","IMPRINT",FACE,{"disambiguationData":[TD([[makeQuery(id+"F2.imprint","IMPRINT",EDGE,{"derivedFrom":sQuery(id+"F2.wireOp",EDGE,"E54")}),-1.0]])]});
            extrude(context, id + "F26", {"entities" : qUnion([Q0]), "operationType" : NewBodyOperationType.ADD, "depth" : 3.72 * mm, "offsetDistance" : 25.4 * mm});
        }
        {
            var Q0;
            Q0=makeQuery(id+"F2.imprint","IMPRINT",FACE,{"disambiguationData":[TD([[makeQuery(id+"F2.imprint","IMPRINT",EDGE,{"derivedFrom":sQuery(id+"F2.wireOp",EDGE,"E51")}),1.0]])]});
            extrude(context, id + "F27", {"entities" : qUnion([Q0]), "operationType" : NewBodyOperationType.ADD, "depth" : 3.53 * mm, "offsetDistance" : 25.4 * mm});
        }
        {
            var Q0;
            {var subQ2=sQuery(id+"F2.wireOp",EDGE,"E122");Q0=makeQuery(id+"F2.imprint","IMPRINT",FACE,{"disambiguationData":[TD([[makeQuery(id+"F2.imprint","IMPRINT",EDGE,{"derivedFrom":subQ2}),1.0]])]});}
            extrude(context, id + "F28", {"entities" : qUnion([Q0]), "operationType" : NewBodyOperationType.ADD, "depth" : 3.16 * mm, "offsetDistance" : 25.4 * mm});
        }
        {
            var Q0;
            Q0=makeQuery(id+"F2.imprint","IMPRINT",FACE,{"disambiguationData":[TD([[makeQuery(id+"F2.imprint","IMPRINT",EDGE,{"derivedFrom":sQuery(id+"F2.wireOp",EDGE,"E24")}),-1.0]])]});
            extrude(context, id + "F29", {"entities" : qUnion([Q0]), "operationType" : NewBodyOperationType.ADD, "depth" : 3.1 * mm, "offsetDistance" : 25.4 * mm});
        }
        {
            var Q0;
            Q0=makeQuery(id+"F2.imprint","IMPRINT",FACE,{"disambiguationData":[TD([[makeQuery(id+"F2.imprint","IMPRINT",EDGE,{"derivedFrom":sQuery(id+"F2.wireOp",EDGE,"E197")}),-1.0]])]});
            extrude(context, id + "F30", {"entities" : qUnion([Q0]), "operationType" : NewBodyOperationType.ADD, "depth" : 2.9 * mm, "offsetDistance" : 25.4 * mm});
        }
        {
            var Q0;
            Q0=makeQuery(id+"F2.imprint","IMPRINT",FACE,{"disambiguationData":[TD([[makeQuery(id+"F2.imprint","IMPRINT",EDGE,{"derivedFrom":sQuery(id+"F2.wireOp",EDGE,"E39")}),1.0]])]});
            extrude(context, id + "F31", {"entities" : qUnion([Q0]), "operationType" : NewBodyOperationType.ADD, "depth" : 2.48 * mm, "offsetDistance" : 25.4 * mm});
        }
        {
            var Q0;
            {var subQ0=sQuery(id+"F2.wireOp",EDGE,"E308");Q0=makeQuery(id+"F2.imprint","IMPRINT",FACE,{"disambiguationData":[TD([[makeQuery(id+"F2.imprint","IMPRINT",EDGE,{"derivedFrom":subQ0}),-1.0]])]});}
            extrude(context, id + "F32", {"entities" : qUnion([Q0]), "operationType" : NewBodyOperationType.ADD, "depth" : 2.4 * mm, "offsetDistance" : 25.4 * mm});
        }
        {
            var Q0;
            Q0=makeQuery(id+"F2.imprint","IMPRINT",FACE,{"disambiguationData":[TD([[makeQuery(id+"F2.imprint","IMPRINT",EDGE,{"derivedFrom":sQuery(id+"F2.wireOp",EDGE,"E47")}),-1.0]])]});
            extrude(context, id + "F33", {"entities" : qUnion([Q0]), "operationType" : NewBodyOperationType.ADD, "depth" : 2.38 * mm, "offsetDistance" : 25.4 * mm});
        }
        {
            var Q0;
            Q0=makeQuery(id+"F2.imprint","IMPRINT",FACE,{"disambiguationData":[TD([[makeQuery(id+"F2.imprint","IMPRINT",EDGE,{"derivedFrom":sQuery(id+"F2.wireOp",EDGE,"E11")}),-1.0]])]});
            extrude(context, id + "F34", {"entities" : qUnion([Q0]), "operationType" : NewBodyOperationType.ADD, "depth" : 2.33 * mm, "offsetDistance" : 25.4 * mm});
        }
        {
            var Q0;
            Q0=makeQuery(id+"F2.imprint","IMPRINT",FACE,{"disambiguationData":[TD([[makeQuery(id+"F2.imprint","IMPRINT",EDGE,{"derivedFrom":sQuery(id+"F2.wireOp",EDGE,"E37")}),-1.0]])]});
            extrude(context, id + "F35", {"entities" : qUnion([Q0]), "operationType" : NewBodyOperationType.ADD, "depth" : 2.33 * mm, "offsetDistance" : 25.4 * mm});
        }
        {
            var Q0;
            {var subQ0=sQuery(id+"F2.wireOp",EDGE,"E16");Q0=makeQuery(id+"F2.imprint","IMPRINT",FACE,{"disambiguationData":[TD([[makeQuery(id+"F2.imprint","IMPRINT",EDGE,{"derivedFrom":subQ0}),1.0]])]});}
            extrude(context, id + "F36", {"entities" : qUnion([Q0]), "operationType" : NewBodyOperationType.ADD, "depth" : 2.24 * mm, "offsetDistance" : 25.4 * mm});
        }
        {
            var Q0;
            Q0=makeQuery(id+"F2.imprint","IMPRINT",FACE,{"disambiguationData":[TD([[makeQuery(id+"F2.imprint","IMPRINT",EDGE,{"derivedFrom":sQuery(id+"F2.wireOp",EDGE,"E12")}),1.0]])]});
            extrude(context, id + "F37", {"entities" : qUnion([Q0]), "operationType" : NewBodyOperationType.ADD, "depth" : 1.5 * mm, "offsetDistance" : 25.4 * mm});
        }
        {
            var Q0;
            Q0=makeQuery(id+"F2.imprint","IMPRINT",FACE,{"disambiguationData":[TD([[makeQuery(id+"F2.imprint","IMPRINT",EDGE,{"derivedFrom":sQuery(id+"F2.wireOp",EDGE,"E711")}),-1.0]])]});
            extrude(context, id + "F38", {"entities" : qUnion([Q0]), "operationType" : NewBodyOperationType.ADD, "depth" : 1.49 * mm, "offsetDistance" : 25.4 * mm});
        }
        {
            var Q0;
            {var subQ2=sQuery(id+"F2.wireOp",EDGE,"E13");Q0=makeQuery(id+"F2.imprint","IMPRINT",FACE,{"disambiguationData":[TD([[makeQuery(id+"F2.imprint","IMPRINT",EDGE,{"derivedFrom":subQ2}),1.0]])]});}
            extrude(context, id + "F39", {"entities" : qUnion([Q0]), "operationType" : NewBodyOperationType.ADD, "depth" : 1.3 * mm, "offsetDistance" : 25.4 * mm});
        }
        {
            var Q0;
            Q0=makeQuery(id+"F2.imprint","IMPRINT",FACE,{"disambiguationData":[TD([[makeQuery(id+"F2.imprint","IMPRINT",EDGE,{"derivedFrom":sQuery(id+"F2.wireOp",EDGE,"E1431")}),-1.0]])]});
            var Q1;
            Q1=makeQuery(id+"F2.imprint","IMPRINT",FACE,{"disambiguationData":[TD([[makeQuery(id+"F2.imprint","IMPRINT",EDGE,{"derivedFrom":sQuery(id+"F2.wireOp",EDGE,"E1439")}),1.0]])]});
            var Q2;
            Q2=makeQuery(id+"F2.imprint","IMPRINT",FACE,{"disambiguationData":[TD([[makeQuery(id+"F2.imprint","IMPRINT",EDGE,{"derivedFrom":sQuery(id+"F2.wireOp",EDGE,"E1408")}),1.0]])]});
            var Q3;
            Q3=makeQuery(id+"F2.imprint","IMPRINT",FACE,{"disambiguationData":[TD([[makeQuery(id+"F2.imprint","IMPRINT",EDGE,{"derivedFrom":sQuery(id+"F2.wireOp",EDGE,"E1401")}),-1.0]])]});
            var Q4;
            Q4=makeQuery(id+"F2.imprint","IMPRINT",FACE,{"disambiguationData":[TD([[makeQuery(id+"F2.imprint","IMPRINT",EDGE,{"derivedFrom":sQuery(id+"F2.wireOp",EDGE,"E1417")}),1.0]])]});
            var Q5;
            Q5=makeQuery(id+"F2.imprint","IMPRINT",FACE,{"disambiguationData":[TD([[makeQuery(id+"F2.imprint","IMPRINT",EDGE,{"derivedFrom":sQuery(id+"F2.wireOp",EDGE,"E1426")}),-1.0]])]});
            var Q6;
            Q6=makeQuery(id+"F2.imprint","IMPRINT",FACE,{"disambiguationData":[TD([[makeQuery(id+"F2.imprint","IMPRINT",EDGE,{"derivedFrom":sQuery(id+"F2.wireOp",EDGE,"E1396")}),-1.0]])]});
            extrude(context, id + "F40", {"entities" : qUnion([Q0, Q1, Q2, Q3, Q4, Q5, Q6]), "operationType" : NewBodyOperationType.ADD, "depth" : 1.13 * mm, "offsetDistance" : 25.4 * mm});
        }
        {
            var Q0;
            Q0=makeQuery(id+"F2.imprint","IMPRINT",FACE,{"disambiguationData":[TD([[makeQuery(id+"F2.imprint","IMPRINT",EDGE,{"derivedFrom":sQuery(id+"F2.wireOp",EDGE,"E854")}),-1.0]])]});
            extrude(context, id + "F41", {"entities" : qUnion([Q0]), "operationType" : NewBodyOperationType.ADD, "depth" : 1.07 * mm, "offsetDistance" : 25.4 * mm});
        }
        {
            var Q0;
            {var subQ1=sQuery(id+"F2.wireOp",EDGE,"E621");Q0=makeQuery(id+"F2.imprint","IMPRINT",FACE,{"disambiguationData":[TD([[makeQuery(id+"F2.imprint","IMPRINT",EDGE,{"derivedFrom":subQ1}),1.0]])]});}
            extrude(context, id + "F42", {"entities" : qUnion([Q0]), "operationType" : NewBodyOperationType.ADD, "depth" : 1.06 * mm, "offsetDistance" : 25.4 * mm});
        }
        {
            var Q0;
            Q0=makeQuery(id+"F2.imprint","IMPRINT",FACE,{"disambiguationData":[TD([[makeQuery(id+"F2.imprint","IMPRINT",EDGE,{"derivedFrom":sQuery(id+"F2.wireOp",EDGE,"E608")}),-1.0]])]});
            extrude(context, id + "F43", {"entities" : qUnion([Q0]), "operationType" : NewBodyOperationType.ADD, "depth" : 0.84 * mm, "offsetDistance" : 25.4 * mm});
        }
        {
            var Q0;
            {var subQ5=sQuery(id+"F2.wireOp",EDGE,"E21");Q0=makeQuery(id+"F2.imprint","IMPRINT",FACE,{"disambiguationData":[TD([[makeQuery(id+"F2.imprint","IMPRINT",EDGE,{"derivedFrom":subQ5}),-1.0]])]});}
            extrude(context, id + "F44", {"entities" : qUnion([Q0]), "operationType" : NewBodyOperationType.ADD, "depth" : 0.82 * mm, "offsetDistance" : 25.4 * mm});
        }
        {
            var Q0;
            {var subQ3=sQuery(id+"F2.wireOp",EDGE,"E606");Q0=makeQuery(id+"F2.imprint","IMPRINT",FACE,{"disambiguationData":[TD([[makeQuery(id+"F2.imprint","IMPRINT",EDGE,{"derivedFrom":subQ3}),1.0]])]});}
            extrude(context, id + "F45", {"entities" : qUnion([Q0]), "operationType" : NewBodyOperationType.ADD, "depth" : 0.74 * mm, "offsetDistance" : 25.4 * mm});
        }
        {
            var Q0;
            Q0=makeQuery(id+"F2.imprint","IMPRINT",FACE,{"disambiguationData":[TD([[makeQuery(id+"F2.imprint","IMPRINT",EDGE,{"derivedFrom":sQuery(id+"F2.wireOp",EDGE,"E36")}),1.0]])]});
            extrude(context, id + "F46", {"entities" : qUnion([Q0]), "operationType" : NewBodyOperationType.ADD, "depth" : 0.68 * mm, "offsetDistance" : 25.4 * mm});
        }
        {
            var Q0;
            Q0=makeQuery(id+"F2.imprint","IMPRINT",FACE,{"disambiguationData":[TD([[makeQuery(id+"F2.imprint","IMPRINT",EDGE,{"derivedFrom":sQuery(id+"F2.wireOp",EDGE,"E1179")}),1.0]])]});
            extrude(context, id + "F47", {"entities" : qUnion([Q0]), "operationType" : NewBodyOperationType.ADD, "depth" : 0.6 * mm, "offsetDistance" : 25.4 * mm});
        }
        {
            var Q0;
            {var subQ4=sQuery(id+"F2.wireOp",EDGE,"E260");Q0=makeQuery(id+"F2.imprint","IMPRINT",FACE,{"disambiguationData":[TD([[makeQuery(id+"F2.imprint","IMPRINT",EDGE,{"derivedFrom":subQ4}),1.0]])]});}
            extrude(context, id + "F48", {"entities" : qUnion([Q0]), "operationType" : NewBodyOperationType.ADD, "depth" : 0.58 * mm, "offsetDistance" : 25.4 * mm});
        }
        {
            var Q0;
            {var subQ1=sQuery(id+"F2.wireOp",EDGE,"E202");Q0=makeQuery(id+"F2.imprint","IMPRINT",FACE,{"disambiguationData":[TD([[makeQuery(id+"F2.imprint","IMPRINT",EDGE,{"derivedFrom":subQ1}),-1.0]])]});}
            extrude(context, id + "F49", {"entities" : qUnion([Q0]), "operationType" : NewBodyOperationType.ADD, "depth" : 0.5 * mm, "offsetDistance" : 25.4 * mm});
        }
        {
            var Q0;
            {var subQ3=sQuery(id+"F2.wireOp",EDGE,"E14");Q0=makeQuery(id+"F2.imprint","IMPRINT",FACE,{"disambiguationData":[TD([[makeQuery(id+"F2.imprint","IMPRINT",EDGE,{"derivedFrom":subQ3}),1.0]])]});}
            extrude(context, id + "F50", {"entities" : qUnion([Q0]), "operationType" : NewBodyOperationType.ADD, "depth" : 0.47 * mm, "offsetDistance" : 25.4 * mm});
        }
        {
            var Q0;
            Q0=makeQuery(id+"F2.imprint","IMPRINT",FACE,{"disambiguationData":[TD([[makeQuery(id+"F2.imprint","IMPRINT",EDGE,{"derivedFrom":sQuery(id+"F2.wireOp",EDGE,"E22")}),1.0]])]});
            extrude(context, id + "F51", {"entities" : qUnion([Q0]), "operationType" : NewBodyOperationType.ADD, "depth" : 1.68 * mm, "offsetDistance" : 25.4 * mm});
        }
    });
